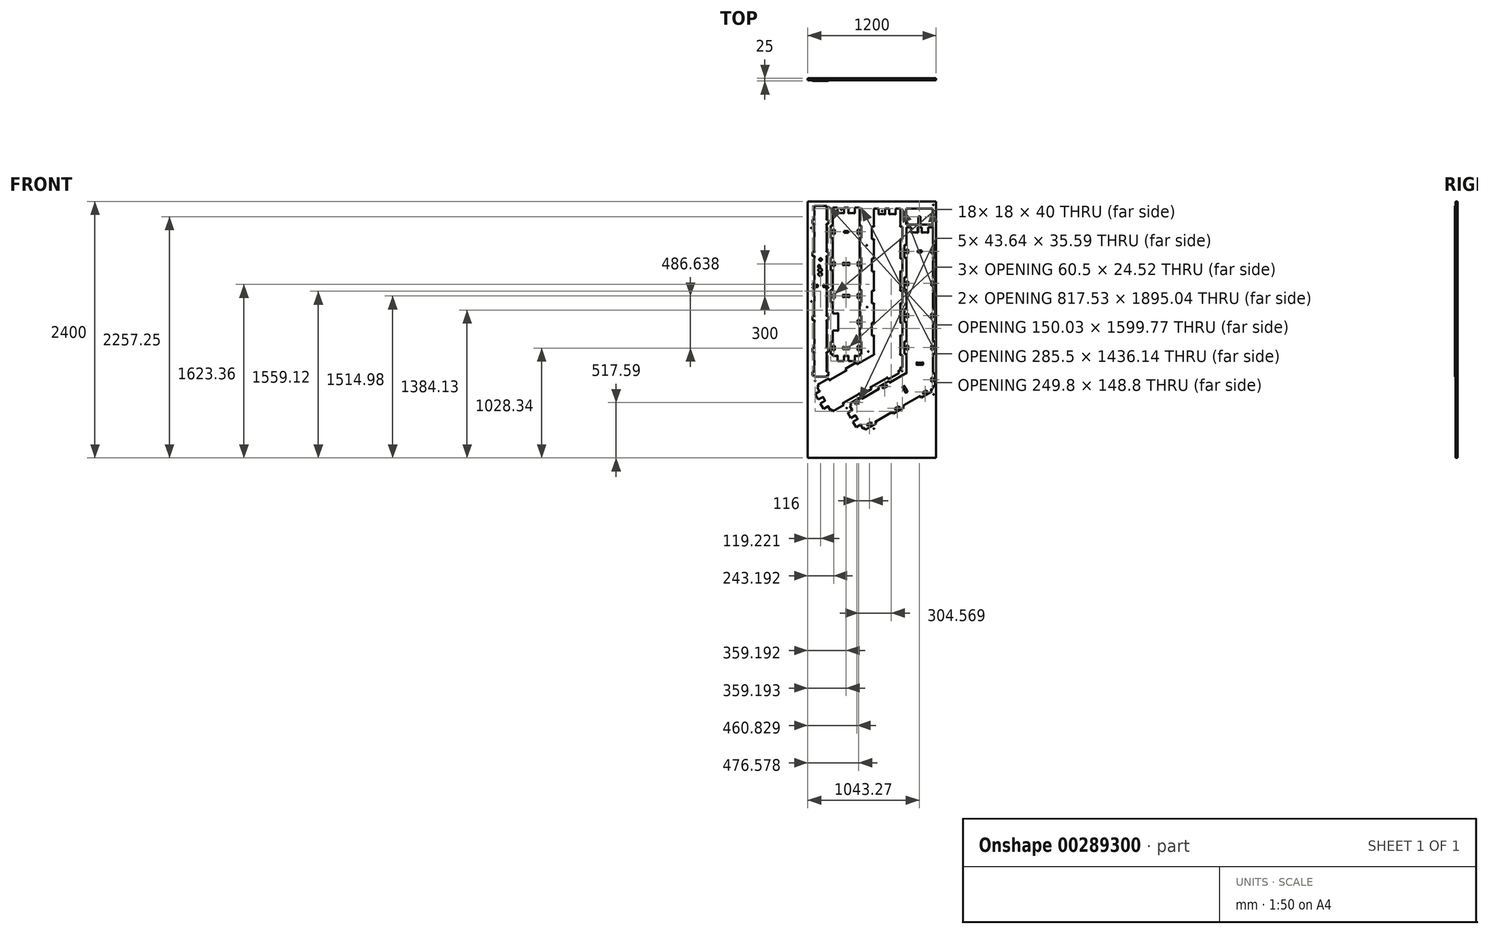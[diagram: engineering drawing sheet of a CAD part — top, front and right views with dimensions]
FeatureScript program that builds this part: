
annotation { "Feature Type Name" : "Feature", "Feature Type Description" : "" }
export const myFeature = defineFeature(function(context is Context, id is Id, definition is map)
    precondition{}
    {
        {
            var Q0;
            Q0=qCreatedBy(makeId("Front.planeOp"),FACE);
            var sketch = newSketch(context, id + "F0", { "sketchPlane" : qUnion([Q0])});
            skLineSegment(sketch, "E0", {"start": v(-600, -1200) * mm, "end": v(600, -1200) * mm});
            skLineSegment(sketch, "E1", {"start": v(600, -1200) * mm, "end": v(600, 1200) * mm});
            skLineSegment(sketch, "E2", {"start": v(600, 1200) * mm, "end": v(-600, 1200) * mm});
            skLineSegment(sketch, "E3", {"start": v(-600, 1200) * mm, "end": v(-600, -1200) * mm});
            skLineSegment(sketch, "E4", {"start": v(322.16, 191.97) * mm, "end": v(304.4, 191.97) * mm});
            skLineSegment(sketch, "E5", {"start": v(304.4, 191.97) * mm, "end": v(304.4, 72.47) * mm});
            skLineSegment(sketch, "E6", {"start": v(304.4, 72.47) * mm, "end": v(322.16, 72.47) * mm});
            skArc(sketch, "E7", {"start": v(322.16, 72.47) * mm, "mid": v(325.42, 69.33) * mm, "end": v(322.4, 65.95) * mm});
            skLineSegment(sketch, "E8", {"start": v(322.4, 65.95) * mm, "end": v(322.4, -101.5) * mm});
            skArc(sketch, "E9", {"start": v(322.4, -101.5) * mm, "mid": v(325.43, -104.89) * mm, "end": v(322.16, -108.03) * mm});
            skLineSegment(sketch, "E10", {"start": v(322.16, -108.03) * mm, "end": v(304.4, -108.03) * mm});
            skLineSegment(sketch, "E11", {"start": v(304.4, -108.03) * mm, "end": v(304.4, -227.53) * mm});
            skLineSegment(sketch, "E12", {"start": v(304.4, -227.53) * mm, "end": v(322.16, -227.53) * mm});
            skArc(sketch, "E13", {"start": v(322.16, -227.53) * mm, "mid": v(325.42, -230.67) * mm, "end": v(322.4, -234.05) * mm});
            skLineSegment(sketch, "E14", {"start": v(322.4, -234.05) * mm, "end": v(322.4, -405.6) * mm});
            skArc(sketch, "E15", {"start": v(322.4, -405.6) * mm, "mid": v(321.26, -409.95) * mm, "end": v(316.85, -409.02) * mm});
            skLineSegment(sketch, "E16", {"start": v(316.85, -409.02) * mm, "end": v(173.65, -491.7) * mm});
            skArc(sketch, "E17", {"start": v(173.65, -491.7) * mm, "mid": v(172.23, -496) * mm, "end": v(167.88, -494.74) * mm});
            skLineSegment(sketch, "E18", {"start": v(167.88, -494.74) * mm, "end": v(159, -479.37) * mm});
            skLineSegment(sketch, "E19", {"start": v(159, -479.37) * mm, "end": v(55.52, -539.12) * mm});
            skLineSegment(sketch, "E20", {"start": v(55.52, -539.12) * mm, "end": v(64.4, -554.5) * mm});
            skArc(sketch, "E21", {"start": v(64.4, -554.5) * mm, "mid": v(63.3, -558.88) * mm, "end": v(58.87, -557.97) * mm});
            skLineSegment(sketch, "E22", {"start": v(58.87, -557.97) * mm, "end": v(-86.15, -641.7) * mm});
            skArc(sketch, "E23", {"start": v(-86.15, -641.7) * mm, "mid": v(-87.57, -646) * mm, "end": v(-91.93, -644.74) * mm});
            skLineSegment(sketch, "E24", {"start": v(-91.93, -644.74) * mm, "end": v(-100.8, -629.37) * mm});
            skLineSegment(sketch, "E25", {"start": v(-100.8, -629.37) * mm, "end": v(-204.3, -689.12) * mm});
            skLineSegment(sketch, "E26", {"start": v(-204.3, -689.12) * mm, "end": v(-195.42, -704.5) * mm});
            skArc(sketch, "E27", {"start": v(-195.42, -704.5) * mm, "mid": v(-196.5, -708.88) * mm, "end": v(-200.94, -707.97) * mm});
            skLineSegment(sketch, "E28", {"start": v(-200.94, -707.97) * mm, "end": v(-206.82, -711.36) * mm});
            skLineSegment(sketch, "E29", {"start": v(-206.82, -711.36) * mm, "end": v(-187.57, -744.69) * mm});
            skArc(sketch, "E30", {"start": v(-187.57, -744.69) * mm, "mid": v(-183.27, -746.1) * mm, "end": v(-184.53, -750.46) * mm});
            skLineSegment(sketch, "E31", {"start": v(-184.53, -750.46) * mm, "end": v(-227.62, -775.33) * mm});
            skLineSegment(sketch, "E32", {"start": v(-227.62, -775.33) * mm, "end": v(-197.87, -826.86) * mm});
            skLineSegment(sketch, "E33", {"start": v(-197.87, -826.86) * mm, "end": v(-154.78, -801.99) * mm});
            skArc(sketch, "E34", {"start": v(-154.78, -801.99) * mm, "mid": v(-150.39, -803.08) * mm, "end": v(-151.3, -807.5) * mm});
            skLineSegment(sketch, "E35", {"start": v(-151.3, -807.5) * mm, "end": v(-137.58, -831.29) * mm});
            skArc(sketch, "E36", {"start": v(-137.58, -831.29) * mm, "mid": v(-133.27, -832.7) * mm, "end": v(-134.53, -837.06) * mm});
            skLineSegment(sketch, "E37", {"start": v(-134.53, -837.06) * mm, "end": v(-177.62, -861.93) * mm});
            skLineSegment(sketch, "E38", {"start": v(-177.62, -861.93) * mm, "end": v(-147.87, -913.46) * mm});
            skLineSegment(sketch, "E39", {"start": v(-147.87, -913.46) * mm, "end": v(-104.78, -888.59) * mm});
            skArc(sketch, "E40", {"start": v(-104.78, -888.59) * mm, "mid": v(-100.39, -889.68) * mm, "end": v(-101.3, -894.1) * mm});
            skLineSegment(sketch, "E41", {"start": v(-101.3, -894.1) * mm, "end": v(-82.06, -927.43) * mm});
            skLineSegment(sketch, "E42", {"start": v(-82.06, -927.43) * mm, "end": v(-76.19, -924.04) * mm});
            skArc(sketch, "E43", {"start": v(-76.19, -924.04) * mm, "mid": v(-74.77, -919.74) * mm, "end": v(-70.42, -921) * mm});
            skLineSegment(sketch, "E44", {"start": v(-70.42, -921) * mm, "end": v(-61.54, -936.37) * mm});
            skLineSegment(sketch, "E45", {"start": v(-61.54, -936.37) * mm, "end": v(41.95, -876.62) * mm});
            skLineSegment(sketch, "E46", {"start": v(41.95, -876.62) * mm, "end": v(33.07, -861.25) * mm});
            skArc(sketch, "E47", {"start": v(33.07, -861.25) * mm, "mid": v(34.16, -856.86) * mm, "end": v(38.6, -857.77) * mm});
            skLineSegment(sketch, "E48", {"start": v(38.6, -857.77) * mm, "end": v(183.62, -774.04) * mm});
            skArc(sketch, "E49", {"start": v(183.62, -774.04) * mm, "mid": v(185.04, -769.74) * mm, "end": v(189.4, -771) * mm});
            skLineSegment(sketch, "E50", {"start": v(189.4, -771) * mm, "end": v(198.27, -786.37) * mm});
            skLineSegment(sketch, "E51", {"start": v(198.27, -786.37) * mm, "end": v(301.76, -726.62) * mm});
            skLineSegment(sketch, "E52", {"start": v(301.76, -726.62) * mm, "end": v(292.88, -711.25) * mm});
            skArc(sketch, "E53", {"start": v(292.88, -711.25) * mm, "mid": v(293.97, -706.86) * mm, "end": v(298.4, -707.77) * mm});
            skLineSegment(sketch, "E54", {"start": v(298.4, -707.77) * mm, "end": v(443.43, -624.04) * mm});
            skArc(sketch, "E55", {"start": v(443.43, -624.04) * mm, "mid": v(444.85, -619.74) * mm, "end": v(449.2, -621) * mm});
            skLineSegment(sketch, "E56", {"start": v(449.2, -621) * mm, "end": v(458.07, -636.37) * mm});
            skLineSegment(sketch, "E57", {"start": v(458.07, -636.37) * mm, "end": v(561.56, -576.62) * mm});
            skLineSegment(sketch, "E58", {"start": v(561.56, -576.62) * mm, "end": v(552.69, -561.25) * mm});
            skArc(sketch, "E59", {"start": v(552.69, -561.25) * mm, "mid": v(553.78, -556.86) * mm, "end": v(558.21, -557.77) * mm});
            skLineSegment(sketch, "E60", {"start": v(558.21, -557.77) * mm, "end": v(571.91, -549.86) * mm});
            skLineSegment(sketch, "E61", {"start": v(571.91, -549.86) * mm, "end": v(571.91, -534.05) * mm});
            skArc(sketch, "E62", {"start": v(571.91, -534.05) * mm, "mid": v(568.9, -530.67) * mm, "end": v(572.16, -527.53) * mm});
            skLineSegment(sketch, "E63", {"start": v(572.16, -527.53) * mm, "end": v(589.91, -527.53) * mm});
            skLineSegment(sketch, "E64", {"start": v(589.91, -527.53) * mm, "end": v(589.91, -408.03) * mm});
            skLineSegment(sketch, "E65", {"start": v(589.91, -408.03) * mm, "end": v(572.16, -408.03) * mm});
            skArc(sketch, "E66", {"start": v(572.16, -408.03) * mm, "mid": v(568.9, -404.89) * mm, "end": v(571.91, -401.5) * mm});
            skLineSegment(sketch, "E67", {"start": v(571.91, -401.5) * mm, "end": v(571.91, -234.05) * mm});
            skArc(sketch, "E68", {"start": v(571.91, -234.05) * mm, "mid": v(568.9, -230.67) * mm, "end": v(572.16, -227.53) * mm});
            skLineSegment(sketch, "E69", {"start": v(572.16, -227.53) * mm, "end": v(589.91, -227.53) * mm});
            skLineSegment(sketch, "E70", {"start": v(589.91, -227.53) * mm, "end": v(589.91, -108.03) * mm});
            skLineSegment(sketch, "E71", {"start": v(589.91, -108.03) * mm, "end": v(572.16, -108.03) * mm});
            skArc(sketch, "E72", {"start": v(572.16, -108.03) * mm, "mid": v(568.9, -104.89) * mm, "end": v(571.91, -101.5) * mm});
            skLineSegment(sketch, "E73", {"start": v(571.91, -101.5) * mm, "end": v(571.91, 65.95) * mm});
            skArc(sketch, "E74", {"start": v(571.91, 65.95) * mm, "mid": v(568.9, 69.33) * mm, "end": v(572.16, 72.47) * mm});
            skLineSegment(sketch, "E75", {"start": v(572.16, 72.47) * mm, "end": v(589.91, 72.47) * mm});
            skLineSegment(sketch, "E76", {"start": v(589.91, 72.47) * mm, "end": v(589.91, 191.97) * mm});
            skLineSegment(sketch, "E77", {"start": v(589.91, 191.97) * mm, "end": v(572.16, 191.97) * mm});
            skArc(sketch, "E78", {"start": v(572.16, 191.97) * mm, "mid": v(568.9, 195.11) * mm, "end": v(571.91, 198.5) * mm});
            skLineSegment(sketch, "E79", {"start": v(571.91, 198.5) * mm, "end": v(571.91, 365.95) * mm});
            skArc(sketch, "E80", {"start": v(571.91, 365.95) * mm, "mid": v(568.9, 369.33) * mm, "end": v(572.16, 372.47) * mm});
            skLineSegment(sketch, "E81", {"start": v(572.16, 372.47) * mm, "end": v(589.91, 372.47) * mm});
            skLineSegment(sketch, "E82", {"start": v(589.91, 372.47) * mm, "end": v(589.91, 491.97) * mm});
            skLineSegment(sketch, "E83", {"start": v(589.91, 491.97) * mm, "end": v(572.16, 491.97) * mm});
            skArc(sketch, "E84", {"start": v(572.16, 491.97) * mm, "mid": v(568.9, 495.11) * mm, "end": v(571.91, 498.5) * mm});
            skLineSegment(sketch, "E85", {"start": v(571.91, 498.5) * mm, "end": v(571.91, 665.95) * mm});
            skArc(sketch, "E86", {"start": v(571.91, 665.95) * mm, "mid": v(568.9, 669.33) * mm, "end": v(572.16, 672.47) * mm});
            skLineSegment(sketch, "E87", {"start": v(572.16, 672.47) * mm, "end": v(589.91, 672.47) * mm});
            skLineSegment(sketch, "E88", {"start": v(589.91, 672.47) * mm, "end": v(589.91, 791.97) * mm});
            skLineSegment(sketch, "E89", {"start": v(589.91, 791.97) * mm, "end": v(572.16, 791.97) * mm});
            skArc(sketch, "E90", {"start": v(572.16, 791.97) * mm, "mid": v(568.9, 795.11) * mm, "end": v(571.91, 798.5) * mm});
            skLineSegment(sketch, "E91", {"start": v(571.91, 798.5) * mm, "end": v(571.91, 958.67) * mm});
            skLineSegment(sketch, "E92", {"start": v(571.91, 958.67) * mm, "end": v(527.41, 958.67) * mm});
            skLineSegment(sketch, "E93", {"start": v(527.41, 958.67) * mm, "end": v(527.41, 908.92) * mm});
            skArc(sketch, "E94", {"start": v(527.41, 908.92) * mm, "mid": v(524.27, 905.66) * mm, "end": v(520.9, 908.67) * mm});
            skLineSegment(sketch, "E95", {"start": v(520.9, 908.67) * mm, "end": v(473.43, 908.67) * mm});
            skArc(sketch, "E96", {"start": v(473.43, 908.67) * mm, "mid": v(470.05, 905.65) * mm, "end": v(466.91, 908.92) * mm});
            skLineSegment(sketch, "E97", {"start": v(466.91, 908.92) * mm, "end": v(466.91, 958.67) * mm});
            skLineSegment(sketch, "E98", {"start": v(466.91, 958.67) * mm, "end": v(427.41, 958.67) * mm});
            skLineSegment(sketch, "E99", {"start": v(427.41, 958.67) * mm, "end": v(427.41, 908.92) * mm});
            skArc(sketch, "E100", {"start": v(427.41, 908.92) * mm, "mid": v(424.27, 905.66) * mm, "end": v(420.9, 908.67) * mm});
            skLineSegment(sketch, "E101", {"start": v(420.9, 908.67) * mm, "end": v(373.43, 908.67) * mm});
            skArc(sketch, "E102", {"start": v(373.43, 908.67) * mm, "mid": v(370.05, 905.65) * mm, "end": v(366.9, 908.92) * mm});
            skLineSegment(sketch, "E103", {"start": v(366.9, 908.92) * mm, "end": v(366.9, 958.67) * mm});
            skLineSegment(sketch, "E104", {"start": v(366.9, 958.67) * mm, "end": v(322.4, 958.67) * mm});
            skLineSegment(sketch, "E105", {"start": v(322.4, 958.67) * mm, "end": v(322.4, 798.5) * mm});
            skArc(sketch, "E106", {"start": v(322.4, 798.5) * mm, "mid": v(325.43, 795.11) * mm, "end": v(322.16, 791.97) * mm});
            skLineSegment(sketch, "E107", {"start": v(322.16, 791.97) * mm, "end": v(304.4, 791.97) * mm});
            skLineSegment(sketch, "E108", {"start": v(304.4, 791.97) * mm, "end": v(304.4, 672.47) * mm});
            skLineSegment(sketch, "E109", {"start": v(304.4, 672.47) * mm, "end": v(322.16, 672.47) * mm});
            skArc(sketch, "E110", {"start": v(322.16, 672.47) * mm, "mid": v(325.42, 669.33) * mm, "end": v(322.4, 665.95) * mm});
            skLineSegment(sketch, "E111", {"start": v(322.4, 665.95) * mm, "end": v(322.4, 498.5) * mm});
            skArc(sketch, "E112", {"start": v(322.4, 498.5) * mm, "mid": v(325.43, 495.11) * mm, "end": v(322.16, 491.97) * mm});
            skLineSegment(sketch, "E113", {"start": v(322.16, 491.97) * mm, "end": v(304.4, 491.97) * mm});
            skLineSegment(sketch, "E114", {"start": v(304.4, 491.97) * mm, "end": v(304.4, 372.47) * mm});
            skLineSegment(sketch, "E115", {"start": v(304.4, 372.47) * mm, "end": v(322.16, 372.47) * mm});
            skArc(sketch, "E116", {"start": v(322.16, 372.47) * mm, "mid": v(325.42, 369.33) * mm, "end": v(322.4, 365.95) * mm});
            skLineSegment(sketch, "E117", {"start": v(322.4, 365.95) * mm, "end": v(322.4, 198.5) * mm});
            skArc(sketch, "E118", {"start": v(322.4, 198.5) * mm, "mid": v(325.43, 195.11) * mm, "end": v(322.16, 191.97) * mm});
            skArc(sketch, "E119", {"start": v(17.84, 71.47) * mm, "mid": v(20.86, 68.1) * mm, "end": v(17.6, 64.95) * mm});
            skLineSegment(sketch, "E120", {"start": v(17.6, 64.95) * mm, "end": v(-0.16, 64.95) * mm});
            skLineSegment(sketch, "E121", {"start": v(-0.16, 64.95) * mm, "end": v(-0.16, -54.55) * mm});
            skLineSegment(sketch, "E122", {"start": v(-0.16, -54.55) * mm, "end": v(17.6, -54.55) * mm});
            skArc(sketch, "E123", {"start": v(17.6, -54.55) * mm, "mid": v(20.85, -57.69) * mm, "end": v(17.84, -61.07) * mm});
            skLineSegment(sketch, "E124", {"start": v(17.84, -61.07) * mm, "end": v(17.84, -226.42) * mm});
            skArc(sketch, "E125", {"start": v(17.84, -226.42) * mm, "mid": v(20.86, -229.76) * mm, "end": v(17.66, -232.94) * mm});
            skLineSegment(sketch, "E126", {"start": v(17.66, -232.94) * mm, "end": v(-130.92, -318.72) * mm});
            skArc(sketch, "E127", {"start": v(-130.92, -318.72) * mm, "mid": v(-132.34, -323.02) * mm, "end": v(-136.69, -321.76) * mm});
            skLineSegment(sketch, "E128", {"start": v(-136.69, -321.76) * mm, "end": v(-145.56, -306.39) * mm});
            skLineSegment(sketch, "E129", {"start": v(-145.56, -306.39) * mm, "end": v(-249.05, -366.14) * mm});
            skLineSegment(sketch, "E130", {"start": v(-249.05, -366.14) * mm, "end": v(-240.18, -381.5) * mm});
            skArc(sketch, "E131", {"start": v(-240.18, -381.5) * mm, "mid": v(-241.27, -385.9) * mm, "end": v(-245.7, -384.99) * mm});
            skLineSegment(sketch, "E132", {"start": v(-245.7, -384.99) * mm, "end": v(-390.72, -468.72) * mm});
            skArc(sketch, "E133", {"start": v(-390.72, -468.72) * mm, "mid": v(-392.14, -473.02) * mm, "end": v(-396.5, -471.76) * mm});
            skLineSegment(sketch, "E134", {"start": v(-396.5, -471.76) * mm, "end": v(-405.37, -456.39) * mm});
            skLineSegment(sketch, "E135", {"start": v(-405.37, -456.39) * mm, "end": v(-508.86, -516.14) * mm});
            skLineSegment(sketch, "E136", {"start": v(-508.86, -516.14) * mm, "end": v(-499.99, -531.5) * mm});
            skArc(sketch, "E137", {"start": v(-499.99, -531.5) * mm, "mid": v(-501.08, -535.9) * mm, "end": v(-505.5, -534.99) * mm});
            skLineSegment(sketch, "E138", {"start": v(-505.5, -534.99) * mm, "end": v(-511.38, -538.38) * mm});
            skLineSegment(sketch, "E139", {"start": v(-511.38, -538.38) * mm, "end": v(-492.14, -571.7) * mm});
            skArc(sketch, "E140", {"start": v(-492.14, -571.7) * mm, "mid": v(-487.84, -573.12) * mm, "end": v(-489.1, -577.48) * mm});
            skLineSegment(sketch, "E141", {"start": v(-489.1, -577.48) * mm, "end": v(-532.19, -602.35) * mm});
            skLineSegment(sketch, "E142", {"start": v(-532.19, -602.35) * mm, "end": v(-502.44, -653.88) * mm});
            skLineSegment(sketch, "E143", {"start": v(-502.44, -653.88) * mm, "end": v(-459.35, -629) * mm});
            skArc(sketch, "E144", {"start": v(-459.35, -629) * mm, "mid": v(-454.96, -630.1) * mm, "end": v(-455.87, -634.53) * mm});
            skLineSegment(sketch, "E145", {"start": v(-455.87, -634.53) * mm, "end": v(-442.14, -658.3) * mm});
            skArc(sketch, "E146", {"start": v(-442.14, -658.3) * mm, "mid": v(-437.84, -659.72) * mm, "end": v(-439.1, -664.08) * mm});
            skLineSegment(sketch, "E147", {"start": v(-439.1, -664.08) * mm, "end": v(-482.19, -688.95) * mm});
            skLineSegment(sketch, "E148", {"start": v(-482.19, -688.95) * mm, "end": v(-452.44, -740.48) * mm});
            skLineSegment(sketch, "E149", {"start": v(-452.44, -740.48) * mm, "end": v(-409.35, -715.6) * mm});
            skArc(sketch, "E150", {"start": v(-409.35, -715.6) * mm, "mid": v(-404.96, -716.7) * mm, "end": v(-405.87, -721.13) * mm});
            skLineSegment(sketch, "E151", {"start": v(-405.87, -721.13) * mm, "end": v(-386.63, -754.45) * mm});
            skLineSegment(sketch, "E152", {"start": v(-386.63, -754.45) * mm, "end": v(-380.76, -751.06) * mm});
            skArc(sketch, "E153", {"start": v(-380.76, -751.06) * mm, "mid": v(-379.34, -746.76) * mm, "end": v(-374.99, -748.02) * mm});
            skLineSegment(sketch, "E154", {"start": v(-374.99, -748.02) * mm, "end": v(-366.11, -763.39) * mm});
            skLineSegment(sketch, "E155", {"start": v(-366.11, -763.39) * mm, "end": v(-262.62, -703.64) * mm});
            skLineSegment(sketch, "E156", {"start": v(-262.62, -703.64) * mm, "end": v(-271.5, -688.27) * mm});
            skArc(sketch, "E157", {"start": v(-271.5, -688.27) * mm, "mid": v(-270.4, -683.88) * mm, "end": v(-265.97, -684.79) * mm});
            skLineSegment(sketch, "E158", {"start": v(-265.97, -684.79) * mm, "end": v(-120.95, -601.06) * mm});
            skArc(sketch, "E159", {"start": v(-120.95, -601.06) * mm, "mid": v(-119.53, -596.76) * mm, "end": v(-115.18, -598.02) * mm});
            skLineSegment(sketch, "E160", {"start": v(-115.18, -598.02) * mm, "end": v(-106.3, -613.39) * mm});
            skLineSegment(sketch, "E161", {"start": v(-106.3, -613.39) * mm, "end": v(-2.81, -553.64) * mm});
            skLineSegment(sketch, "E162", {"start": v(-2.81, -553.64) * mm, "end": v(-11.69, -538.27) * mm});
            skArc(sketch, "E163", {"start": v(-11.69, -538.27) * mm, "mid": v(-10.6, -533.87) * mm, "end": v(-6.17, -534.79) * mm});
            skLineSegment(sketch, "E164", {"start": v(-6.17, -534.79) * mm, "end": v(138.86, -451.06) * mm});
            skArc(sketch, "E165", {"start": v(138.86, -451.06) * mm, "mid": v(140.28, -446.76) * mm, "end": v(144.63, -448.02) * mm});
            skLineSegment(sketch, "E166", {"start": v(144.63, -448.02) * mm, "end": v(153.5, -463.39) * mm});
            skLineSegment(sketch, "E167", {"start": v(153.5, -463.39) * mm, "end": v(257, -403.64) * mm});
            skLineSegment(sketch, "E168", {"start": v(257, -403.64) * mm, "end": v(248.12, -388.27) * mm});
            skArc(sketch, "E169", {"start": v(248.12, -388.27) * mm, "mid": v(249.21, -383.87) * mm, "end": v(253.64, -384.79) * mm});
            skLineSegment(sketch, "E170", {"start": v(253.64, -384.79) * mm, "end": v(267.34, -376.88) * mm});
            skLineSegment(sketch, "E171", {"start": v(267.34, -376.88) * mm, "end": v(267.34, -361.07) * mm});
            skArc(sketch, "E172", {"start": v(267.34, -361.07) * mm, "mid": v(264.32, -357.68) * mm, "end": v(267.6, -354.55) * mm});
            skLineSegment(sketch, "E173", {"start": v(267.6, -354.55) * mm, "end": v(285.34, -354.55) * mm});
            skLineSegment(sketch, "E174", {"start": v(285.34, -354.55) * mm, "end": v(285.34, -235.05) * mm});
            skLineSegment(sketch, "E175", {"start": v(285.34, -235.05) * mm, "end": v(267.6, -235.05) * mm});
            skArc(sketch, "E176", {"start": v(267.6, -235.05) * mm, "mid": v(264.33, -231.9) * mm, "end": v(267.34, -228.53) * mm});
            skLineSegment(sketch, "E177", {"start": v(267.34, -228.53) * mm, "end": v(267.34, -61.07) * mm});
            skArc(sketch, "E178", {"start": v(267.34, -61.07) * mm, "mid": v(264.32, -57.68) * mm, "end": v(267.6, -54.55) * mm});
            skLineSegment(sketch, "E179", {"start": v(267.6, -54.55) * mm, "end": v(285.34, -54.55) * mm});
            skLineSegment(sketch, "E180", {"start": v(285.34, -54.55) * mm, "end": v(285.34, 64.95) * mm});
            skLineSegment(sketch, "E181", {"start": v(285.34, 64.95) * mm, "end": v(267.6, 64.95) * mm});
            skArc(sketch, "E182", {"start": v(267.6, 64.95) * mm, "mid": v(264.33, 68.1) * mm, "end": v(267.34, 71.47) * mm});
            skLineSegment(sketch, "E183", {"start": v(267.34, 71.47) * mm, "end": v(267.34, 238.94) * mm});
            skArc(sketch, "E184", {"start": v(267.34, 238.94) * mm, "mid": v(264.32, 242.32) * mm, "end": v(267.6, 245.46) * mm});
            skLineSegment(sketch, "E185", {"start": v(267.6, 245.46) * mm, "end": v(285.34, 245.46) * mm});
            skLineSegment(sketch, "E186", {"start": v(285.34, 245.46) * mm, "end": v(285.34, 364.96) * mm});
            skLineSegment(sketch, "E187", {"start": v(285.34, 364.96) * mm, "end": v(267.6, 364.96) * mm});
            skArc(sketch, "E188", {"start": v(267.6, 364.96) * mm, "mid": v(264.33, 368.1) * mm, "end": v(267.34, 371.48) * mm});
            skLineSegment(sketch, "E189", {"start": v(267.34, 371.48) * mm, "end": v(267.34, 538.94) * mm});
            skArc(sketch, "E190", {"start": v(267.34, 538.94) * mm, "mid": v(264.32, 542.32) * mm, "end": v(267.6, 545.46) * mm});
            skLineSegment(sketch, "E191", {"start": v(267.6, 545.46) * mm, "end": v(285.34, 545.46) * mm});
            skLineSegment(sketch, "E192", {"start": v(285.34, 545.46) * mm, "end": v(285.34, 664.96) * mm});
            skLineSegment(sketch, "E193", {"start": v(285.34, 664.96) * mm, "end": v(267.6, 664.96) * mm});
            skArc(sketch, "E194", {"start": v(267.6, 664.96) * mm, "mid": v(264.33, 668.1) * mm, "end": v(267.34, 671.48) * mm});
            skLineSegment(sketch, "E195", {"start": v(267.34, 671.48) * mm, "end": v(267.34, 838.94) * mm});
            skArc(sketch, "E196", {"start": v(267.34, 838.94) * mm, "mid": v(264.32, 842.32) * mm, "end": v(267.6, 845.46) * mm});
            skLineSegment(sketch, "E197", {"start": v(267.6, 845.46) * mm, "end": v(285.34, 845.46) * mm});
            skLineSegment(sketch, "E198", {"start": v(285.34, 845.46) * mm, "end": v(285.34, 964.96) * mm});
            skLineSegment(sketch, "E199", {"start": v(285.34, 964.96) * mm, "end": v(267.6, 964.96) * mm});
            skArc(sketch, "E200", {"start": v(267.6, 964.96) * mm, "mid": v(264.33, 968.1) * mm, "end": v(267.34, 971.48) * mm});
            skLineSegment(sketch, "E201", {"start": v(267.34, 971.48) * mm, "end": v(267.34, 1131.65) * mm});
            skLineSegment(sketch, "E202", {"start": v(267.34, 1131.65) * mm, "end": v(222.84, 1131.65) * mm});
            skLineSegment(sketch, "E203", {"start": v(222.84, 1131.65) * mm, "end": v(222.84, 1081.9) * mm});
            skArc(sketch, "E204", {"start": v(222.84, 1081.9) * mm, "mid": v(219.7, 1078.64) * mm, "end": v(216.32, 1081.65) * mm});
            skLineSegment(sketch, "E205", {"start": v(216.32, 1081.65) * mm, "end": v(168.86, 1081.65) * mm});
            skArc(sketch, "E206", {"start": v(168.86, 1081.65) * mm, "mid": v(165.48, 1078.64) * mm, "end": v(162.34, 1081.9) * mm});
            skLineSegment(sketch, "E207", {"start": v(162.34, 1081.9) * mm, "end": v(162.34, 1131.65) * mm});
            skLineSegment(sketch, "E208", {"start": v(162.34, 1131.65) * mm, "end": v(122.84, 1131.65) * mm});
            skLineSegment(sketch, "E209", {"start": v(122.84, 1131.65) * mm, "end": v(122.84, 1081.9) * mm});
            skArc(sketch, "E210", {"start": v(122.84, 1081.9) * mm, "mid": v(119.7, 1078.64) * mm, "end": v(116.32, 1081.65) * mm});
            skLineSegment(sketch, "E211", {"start": v(116.32, 1081.65) * mm, "end": v(68.86, 1081.65) * mm});
            skArc(sketch, "E212", {"start": v(68.86, 1081.65) * mm, "mid": v(65.48, 1078.64) * mm, "end": v(62.34, 1081.9) * mm});
            skLineSegment(sketch, "E213", {"start": v(62.34, 1081.9) * mm, "end": v(62.34, 1131.65) * mm});
            skLineSegment(sketch, "E214", {"start": v(62.34, 1131.65) * mm, "end": v(17.84, 1131.65) * mm});
            skLineSegment(sketch, "E215", {"start": v(17.84, 1131.65) * mm, "end": v(17.84, 971.48) * mm});
            skArc(sketch, "E216", {"start": v(17.84, 971.48) * mm, "mid": v(20.86, 968.1) * mm, "end": v(17.6, 964.96) * mm});
            skLineSegment(sketch, "E217", {"start": v(17.6, 964.96) * mm, "end": v(-0.16, 964.96) * mm});
            skLineSegment(sketch, "E218", {"start": v(-0.16, 964.96) * mm, "end": v(-0.16, 845.46) * mm});
            skLineSegment(sketch, "E219", {"start": v(-0.16, 845.46) * mm, "end": v(17.6, 845.46) * mm});
            skArc(sketch, "E220", {"start": v(17.6, 845.46) * mm, "mid": v(20.85, 842.32) * mm, "end": v(17.84, 838.94) * mm});
            skLineSegment(sketch, "E221", {"start": v(17.84, 838.94) * mm, "end": v(17.84, 671.48) * mm});
            skArc(sketch, "E222", {"start": v(17.84, 671.48) * mm, "mid": v(20.86, 668.1) * mm, "end": v(17.6, 664.96) * mm});
            skLineSegment(sketch, "E223", {"start": v(17.6, 664.96) * mm, "end": v(-0.16, 664.96) * mm});
            skLineSegment(sketch, "E224", {"start": v(-0.16, 664.96) * mm, "end": v(-0.16, 545.46) * mm});
            skLineSegment(sketch, "E225", {"start": v(-0.16, 545.46) * mm, "end": v(17.6, 545.46) * mm});
            skArc(sketch, "E226", {"start": v(17.6, 545.46) * mm, "mid": v(20.85, 542.32) * mm, "end": v(17.84, 538.94) * mm});
            skLineSegment(sketch, "E227", {"start": v(17.84, 538.94) * mm, "end": v(17.84, 371.48) * mm});
            skArc(sketch, "E228", {"start": v(17.84, 371.48) * mm, "mid": v(20.86, 368.1) * mm, "end": v(17.6, 364.96) * mm});
            skLineSegment(sketch, "E229", {"start": v(17.6, 364.96) * mm, "end": v(-0.16, 364.96) * mm});
            skLineSegment(sketch, "E230", {"start": v(-0.16, 364.96) * mm, "end": v(-0.16, 245.46) * mm});
            skLineSegment(sketch, "E231", {"start": v(-0.16, 245.46) * mm, "end": v(17.6, 245.46) * mm});
            skArc(sketch, "E232", {"start": v(17.6, 245.46) * mm, "mid": v(20.85, 242.32) * mm, "end": v(17.84, 238.94) * mm});
            skLineSegment(sketch, "E233", {"start": v(17.84, 238.94) * mm, "end": v(17.84, 71.47) * mm});
            skLineSegment(sketch, "E234", {"start": v(-537.8, 1159) * mm, "end": v(-537.8, 1035.02) * mm});
            skArc(sketch, "E235", {"start": v(-537.8, 1035.02) * mm, "mid": v(-534.78, 1032) * mm, "end": v(-537.8, 1029) * mm});
            skLineSegment(sketch, "E236", {"start": v(-537.8, 1029) * mm, "end": v(-552.8, 1029) * mm});
            skLineSegment(sketch, "E237", {"start": v(-552.8, 1029) * mm, "end": v(-555.8, 1026) * mm});
            skLineSegment(sketch, "E238", {"start": v(-555.8, 1026) * mm, "end": v(-555.8, 992) * mm});
            skLineSegment(sketch, "E239", {"start": v(-555.8, 992) * mm, "end": v(-552.8, 989) * mm});
            skLineSegment(sketch, "E240", {"start": v(-552.8, 989) * mm, "end": v(-537.8, 989) * mm});
            skArc(sketch, "E241", {"start": v(-537.8, 989) * mm, "mid": v(-534.78, 985.99) * mm, "end": v(-537.8, 982.98) * mm});
            skLineSegment(sketch, "E242", {"start": v(-537.8, 982.98) * mm, "end": v(-537.79, 735.02) * mm});
            skArc(sketch, "E243", {"start": v(-537.79, 735.02) * mm, "mid": v(-534.78, 732) * mm, "end": v(-537.79, 729) * mm});
            skLineSegment(sketch, "E244", {"start": v(-537.79, 729) * mm, "end": v(-552.79, 729) * mm});
            skLineSegment(sketch, "E245", {"start": v(-552.79, 729) * mm, "end": v(-555.79, 726) * mm});
            skLineSegment(sketch, "E246", {"start": v(-555.79, 726) * mm, "end": v(-555.79, 692) * mm});
            skLineSegment(sketch, "E247", {"start": v(-555.79, 692) * mm, "end": v(-552.79, 689) * mm});
            skLineSegment(sketch, "E248", {"start": v(-552.79, 689) * mm, "end": v(-537.79, 689) * mm});
            skArc(sketch, "E249", {"start": v(-537.79, 689) * mm, "mid": v(-534.78, 685.99) * mm, "end": v(-537.79, 682.98) * mm});
            skLineSegment(sketch, "E250", {"start": v(-537.79, 682.98) * mm, "end": v(-537.78, 435.02) * mm});
            skArc(sketch, "E251", {"start": v(-537.78, 435.02) * mm, "mid": v(-534.77, 432) * mm, "end": v(-537.78, 429) * mm});
            skLineSegment(sketch, "E252", {"start": v(-537.78, 429) * mm, "end": v(-552.78, 429) * mm});
            skLineSegment(sketch, "E253", {"start": v(-552.78, 429) * mm, "end": v(-555.78, 426) * mm});
            skLineSegment(sketch, "E254", {"start": v(-555.78, 426) * mm, "end": v(-555.78, 418) * mm});
            skLineSegment(sketch, "E255", {"start": v(-555.78, 418) * mm, "end": v(-512.8, 418) * mm});
            skArc(sketch, "E256", {"start": v(-512.8, 418) * mm, "mid": v(-509.8, 421) * mm, "end": v(-506.78, 418) * mm});
            skLineSegment(sketch, "E257", {"start": v(-506.78, 418) * mm, "end": v(-506.78, 400) * mm});
            skArc(sketch, "E258", {"start": v(-506.78, 400) * mm, "mid": v(-509.8, 396.99) * mm, "end": v(-512.8, 400) * mm});
            skLineSegment(sketch, "E259", {"start": v(-512.8, 400) * mm, "end": v(-555.78, 400) * mm});
            skLineSegment(sketch, "E260", {"start": v(-555.78, 400) * mm, "end": v(-555.78, 392) * mm});
            skLineSegment(sketch, "E261", {"start": v(-555.78, 392) * mm, "end": v(-552.78, 389) * mm});
            skLineSegment(sketch, "E262", {"start": v(-552.78, 389) * mm, "end": v(-537.78, 389) * mm});
            skArc(sketch, "E263", {"start": v(-537.78, 389) * mm, "mid": v(-534.77, 385.99) * mm, "end": v(-537.78, 382.98) * mm});
            skLineSegment(sketch, "E264", {"start": v(-537.78, 382.98) * mm, "end": v(-537.78, 135.02) * mm});
            skArc(sketch, "E265", {"start": v(-537.78, 135.02) * mm, "mid": v(-534.77, 132) * mm, "end": v(-537.78, 129) * mm});
            skLineSegment(sketch, "E266", {"start": v(-537.78, 129) * mm, "end": v(-552.78, 129) * mm});
            skLineSegment(sketch, "E267", {"start": v(-552.78, 129) * mm, "end": v(-555.78, 126) * mm});
            skLineSegment(sketch, "E268", {"start": v(-555.78, 126) * mm, "end": v(-555.78, 92) * mm});
            skLineSegment(sketch, "E269", {"start": v(-555.78, 92) * mm, "end": v(-552.78, 89) * mm});
            skLineSegment(sketch, "E270", {"start": v(-552.78, 89) * mm, "end": v(-537.78, 89) * mm});
            skArc(sketch, "E271", {"start": v(-537.78, 89) * mm, "mid": v(-534.77, 85.99) * mm, "end": v(-537.78, 82.98) * mm});
            skLineSegment(sketch, "E272", {"start": v(-537.78, 82.98) * mm, "end": v(-537.77, -164.98) * mm});
            skArc(sketch, "E273", {"start": v(-537.77, -164.98) * mm, "mid": v(-534.76, -168) * mm, "end": v(-537.77, -171) * mm});
            skLineSegment(sketch, "E274", {"start": v(-537.77, -171) * mm, "end": v(-552.77, -171) * mm});
            skLineSegment(sketch, "E275", {"start": v(-552.77, -171) * mm, "end": v(-555.77, -174) * mm});
            skLineSegment(sketch, "E276", {"start": v(-555.77, -174) * mm, "end": v(-555.77, -208) * mm});
            skLineSegment(sketch, "E277", {"start": v(-555.77, -208) * mm, "end": v(-552.77, -211) * mm});
            skLineSegment(sketch, "E278", {"start": v(-552.77, -211) * mm, "end": v(-537.77, -211) * mm});
            skArc(sketch, "E279", {"start": v(-537.77, -211) * mm, "mid": v(-534.76, -214.01) * mm, "end": v(-537.77, -217.02) * mm});
            skLineSegment(sketch, "E280", {"start": v(-537.77, -217.02) * mm, "end": v(-537.77, -384.98) * mm});
            skArc(sketch, "E281", {"start": v(-537.77, -384.98) * mm, "mid": v(-534.76, -388) * mm, "end": v(-537.77, -391) * mm});
            skLineSegment(sketch, "E282", {"start": v(-537.77, -391) * mm, "end": v(-552.77, -391) * mm});
            skLineSegment(sketch, "E283", {"start": v(-552.77, -391) * mm, "end": v(-555.77, -394) * mm});
            skLineSegment(sketch, "E284", {"start": v(-555.77, -394) * mm, "end": v(-555.77, -428) * mm});
            skLineSegment(sketch, "E285", {"start": v(-555.77, -428) * mm, "end": v(-552.77, -431) * mm});
            skLineSegment(sketch, "E286", {"start": v(-552.77, -431) * mm, "end": v(-537.77, -431) * mm});
            skArc(sketch, "E287", {"start": v(-537.77, -431) * mm, "mid": v(-534.76, -434.01) * mm, "end": v(-537.77, -437.02) * mm});
            skLineSegment(sketch, "E288", {"start": v(-537.77, -437.02) * mm, "end": v(-537.77, -440.77) * mm});
            skLineSegment(sketch, "E289", {"start": v(-537.77, -440.77) * mm, "end": v(-423.77, -440.77) * mm});
            skLineSegment(sketch, "E290", {"start": v(-423.77, -440.77) * mm, "end": v(-423.77, -437.02) * mm});
            skArc(sketch, "E291", {"start": v(-423.77, -437.02) * mm, "mid": v(-426.78, -434.01) * mm, "end": v(-423.77, -431) * mm});
            skLineSegment(sketch, "E292", {"start": v(-423.77, -431) * mm, "end": v(-408.77, -431) * mm});
            skLineSegment(sketch, "E293", {"start": v(-408.77, -431) * mm, "end": v(-405.77, -428) * mm});
            skLineSegment(sketch, "E294", {"start": v(-405.77, -428) * mm, "end": v(-405.77, -394) * mm});
            skLineSegment(sketch, "E295", {"start": v(-405.77, -394) * mm, "end": v(-408.77, -391) * mm});
            skLineSegment(sketch, "E296", {"start": v(-408.77, -391) * mm, "end": v(-423.77, -391) * mm});
            skArc(sketch, "E297", {"start": v(-423.77, -391) * mm, "mid": v(-426.78, -388) * mm, "end": v(-423.77, -384.98) * mm});
            skLineSegment(sketch, "E298", {"start": v(-423.77, -384.98) * mm, "end": v(-423.77, -217.02) * mm});
            skArc(sketch, "E299", {"start": v(-423.77, -217.02) * mm, "mid": v(-426.78, -214.01) * mm, "end": v(-423.77, -211) * mm});
            skLineSegment(sketch, "E300", {"start": v(-423.77, -211) * mm, "end": v(-408.77, -211) * mm});
            skLineSegment(sketch, "E301", {"start": v(-408.77, -211) * mm, "end": v(-405.77, -208) * mm});
            skLineSegment(sketch, "E302", {"start": v(-405.77, -208) * mm, "end": v(-405.77, -174) * mm});
            skLineSegment(sketch, "E303", {"start": v(-405.77, -174) * mm, "end": v(-408.77, -171) * mm});
            skLineSegment(sketch, "E304", {"start": v(-408.77, -171) * mm, "end": v(-423.77, -171) * mm});
            skArc(sketch, "E305", {"start": v(-423.77, -171) * mm, "mid": v(-426.78, -168) * mm, "end": v(-423.77, -164.98) * mm});
            skLineSegment(sketch, "E306", {"start": v(-423.77, -164.98) * mm, "end": v(-423.78, 82.98) * mm});
            skArc(sketch, "E307", {"start": v(-423.78, 82.98) * mm, "mid": v(-426.79, 85.99) * mm, "end": v(-423.78, 89) * mm});
            skLineSegment(sketch, "E308", {"start": v(-423.78, 89) * mm, "end": v(-408.78, 89) * mm});
            skLineSegment(sketch, "E309", {"start": v(-408.78, 89) * mm, "end": v(-405.78, 92) * mm});
            skLineSegment(sketch, "E310", {"start": v(-405.78, 92) * mm, "end": v(-405.78, 126) * mm});
            skLineSegment(sketch, "E311", {"start": v(-405.78, 126) * mm, "end": v(-408.78, 129) * mm});
            skLineSegment(sketch, "E312", {"start": v(-408.78, 129) * mm, "end": v(-423.78, 129) * mm});
            skArc(sketch, "E313", {"start": v(-423.78, 129) * mm, "mid": v(-426.79, 132) * mm, "end": v(-423.78, 135.02) * mm});
            skLineSegment(sketch, "E314", {"start": v(-423.78, 135.02) * mm, "end": v(-423.78, 382.98) * mm});
            skArc(sketch, "E315", {"start": v(-423.78, 382.98) * mm, "mid": v(-426.8, 385.99) * mm, "end": v(-423.78, 389) * mm});
            skLineSegment(sketch, "E316", {"start": v(-423.78, 389) * mm, "end": v(-408.78, 389) * mm});
            skLineSegment(sketch, "E317", {"start": v(-408.78, 389) * mm, "end": v(-405.78, 392) * mm});
            skLineSegment(sketch, "E318", {"start": v(-405.78, 392) * mm, "end": v(-405.78, 400) * mm});
            skLineSegment(sketch, "E319", {"start": v(-405.78, 400) * mm, "end": v(-448.76, 400) * mm});
            skArc(sketch, "E320", {"start": v(-448.76, 400) * mm, "mid": v(-451.77, 396.99) * mm, "end": v(-454.78, 400) * mm});
            skLineSegment(sketch, "E321", {"start": v(-454.78, 400) * mm, "end": v(-454.78, 418) * mm});
            skArc(sketch, "E322", {"start": v(-454.78, 418) * mm, "mid": v(-451.77, 421) * mm, "end": v(-448.76, 418) * mm});
            skLineSegment(sketch, "E323", {"start": v(-448.76, 418) * mm, "end": v(-405.78, 418) * mm});
            skLineSegment(sketch, "E324", {"start": v(-405.78, 418) * mm, "end": v(-405.78, 426) * mm});
            skLineSegment(sketch, "E325", {"start": v(-405.78, 426) * mm, "end": v(-408.78, 429) * mm});
            skLineSegment(sketch, "E326", {"start": v(-408.78, 429) * mm, "end": v(-423.78, 429) * mm});
            skArc(sketch, "E327", {"start": v(-423.78, 429) * mm, "mid": v(-426.8, 432) * mm, "end": v(-423.78, 435.02) * mm});
            skLineSegment(sketch, "E328", {"start": v(-423.78, 435.02) * mm, "end": v(-423.79, 682.98) * mm});
            skArc(sketch, "E329", {"start": v(-423.79, 682.98) * mm, "mid": v(-426.8, 685.99) * mm, "end": v(-423.79, 689) * mm});
            skLineSegment(sketch, "E330", {"start": v(-423.79, 689) * mm, "end": v(-408.79, 689) * mm});
            skLineSegment(sketch, "E331", {"start": v(-408.79, 689) * mm, "end": v(-405.79, 692) * mm});
            skLineSegment(sketch, "E332", {"start": v(-405.79, 692) * mm, "end": v(-405.79, 726) * mm});
            skLineSegment(sketch, "E333", {"start": v(-405.79, 726) * mm, "end": v(-408.79, 729) * mm});
            skLineSegment(sketch, "E334", {"start": v(-408.79, 729) * mm, "end": v(-423.79, 729) * mm});
            skArc(sketch, "E335", {"start": v(-423.79, 729) * mm, "mid": v(-426.8, 732) * mm, "end": v(-423.79, 735.02) * mm});
            skLineSegment(sketch, "E336", {"start": v(-423.79, 735.02) * mm, "end": v(-423.8, 982.98) * mm});
            skArc(sketch, "E337", {"start": v(-423.8, 982.98) * mm, "mid": v(-426.8, 985.99) * mm, "end": v(-423.8, 989) * mm});
            skLineSegment(sketch, "E338", {"start": v(-423.8, 989) * mm, "end": v(-408.8, 989) * mm});
            skLineSegment(sketch, "E339", {"start": v(-408.8, 989) * mm, "end": v(-405.8, 992) * mm});
            skLineSegment(sketch, "E340", {"start": v(-405.8, 992) * mm, "end": v(-405.8, 1026) * mm});
            skLineSegment(sketch, "E341", {"start": v(-405.8, 1026) * mm, "end": v(-408.8, 1029) * mm});
            skLineSegment(sketch, "E342", {"start": v(-408.8, 1029) * mm, "end": v(-423.8, 1029) * mm});
            skArc(sketch, "E343", {"start": v(-423.8, 1029) * mm, "mid": v(-426.8, 1032) * mm, "end": v(-423.8, 1035.02) * mm});
            skLineSegment(sketch, "E344", {"start": v(-423.8, 1035.02) * mm, "end": v(-423.8, 1159) * mm});
            skLineSegment(sketch, "E345", {"start": v(-423.8, 1159) * mm, "end": v(-537.8, 1159) * mm});
            skLineSegment(sketch, "E346", {"start": v(-98.06, -111.9) * mm, "end": v(-116.06, -111.9) * mm});
            skArc(sketch, "E347", {"start": v(-116.06, -111.9) * mm, "mid": v(-119.07, -108.9) * mm, "end": v(-116.06, -105.89) * mm});
            skLineSegment(sketch, "E348", {"start": v(-116.06, -105.89) * mm, "end": v(-116.06, 5.89) * mm});
            skArc(sketch, "E349", {"start": v(-116.06, 5.89) * mm, "mid": v(-119.07, 8.9) * mm, "end": v(-116.06, 11.9) * mm});
            skLineSegment(sketch, "E350", {"start": v(-116.06, 11.9) * mm, "end": v(-98.06, 11.9) * mm});
            skLineSegment(sketch, "E351", {"start": v(-98.06, 11.9) * mm, "end": v(-98.06, 131.4) * mm});
            skLineSegment(sketch, "E352", {"start": v(-98.06, 131.4) * mm, "end": v(-116.06, 131.4) * mm});
            skArc(sketch, "E353", {"start": v(-116.06, 131.4) * mm, "mid": v(-119.07, 134.42) * mm, "end": v(-116.06, 137.43) * mm});
            skLineSegment(sketch, "E354", {"start": v(-116.06, 137.43) * mm, "end": v(-116.06, 249.2) * mm});
            skArc(sketch, "E355", {"start": v(-116.06, 249.2) * mm, "mid": v(-119.07, 252.22) * mm, "end": v(-116.06, 255.23) * mm});
            skLineSegment(sketch, "E356", {"start": v(-116.06, 255.23) * mm, "end": v(-98.06, 255.23) * mm});
            skLineSegment(sketch, "E357", {"start": v(-98.06, 255.23) * mm, "end": v(-98.06, 374.73) * mm});
            skLineSegment(sketch, "E358", {"start": v(-98.06, 374.73) * mm, "end": v(-116.06, 374.73) * mm});
            skArc(sketch, "E359", {"start": v(-116.06, 374.73) * mm, "mid": v(-119.07, 377.74) * mm, "end": v(-116.06, 380.75) * mm});
            skLineSegment(sketch, "E360", {"start": v(-116.06, 380.75) * mm, "end": v(-116.06, 549.2) * mm});
            skArc(sketch, "E361", {"start": v(-116.06, 549.2) * mm, "mid": v(-119.07, 552.22) * mm, "end": v(-116.06, 555.23) * mm});
            skLineSegment(sketch, "E362", {"start": v(-116.06, 555.23) * mm, "end": v(-98.06, 555.23) * mm});
            skLineSegment(sketch, "E363", {"start": v(-98.06, 555.23) * mm, "end": v(-98.06, 674.73) * mm});
            skLineSegment(sketch, "E364", {"start": v(-98.06, 674.73) * mm, "end": v(-116.06, 674.73) * mm});
            skArc(sketch, "E365", {"start": v(-116.06, 674.73) * mm, "mid": v(-119.07, 677.74) * mm, "end": v(-116.06, 680.75) * mm});
            skLineSegment(sketch, "E366", {"start": v(-116.06, 680.75) * mm, "end": v(-116.06, 849.2) * mm});
            skArc(sketch, "E367", {"start": v(-116.06, 849.2) * mm, "mid": v(-119.07, 852.22) * mm, "end": v(-116.06, 855.23) * mm});
            skLineSegment(sketch, "E368", {"start": v(-116.06, 855.23) * mm, "end": v(-98.06, 855.23) * mm});
            skLineSegment(sketch, "E369", {"start": v(-98.06, 855.23) * mm, "end": v(-98.06, 974.73) * mm});
            skLineSegment(sketch, "E370", {"start": v(-98.06, 974.73) * mm, "end": v(-116.06, 974.73) * mm});
            skArc(sketch, "E371", {"start": v(-116.06, 974.73) * mm, "mid": v(-119.07, 977.74) * mm, "end": v(-116.06, 980.75) * mm});
            skLineSegment(sketch, "E372", {"start": v(-116.06, 980.75) * mm, "end": v(-116.06, 1141.42) * mm});
            skLineSegment(sketch, "E373", {"start": v(-116.06, 1141.42) * mm, "end": v(-160.56, 1141.42) * mm});
            skLineSegment(sketch, "E374", {"start": v(-160.56, 1141.42) * mm, "end": v(-160.56, 1091.42) * mm});
            skArc(sketch, "E375", {"start": v(-160.56, 1091.42) * mm, "mid": v(-163.57, 1088.41) * mm, "end": v(-166.58, 1091.42) * mm});
            skLineSegment(sketch, "E376", {"start": v(-166.58, 1091.42) * mm, "end": v(-215.04, 1091.42) * mm});
            skArc(sketch, "E377", {"start": v(-215.04, 1091.42) * mm, "mid": v(-218.05, 1088.41) * mm, "end": v(-221.06, 1091.42) * mm});
            skLineSegment(sketch, "E378", {"start": v(-221.06, 1091.42) * mm, "end": v(-221.06, 1141.42) * mm});
            skLineSegment(sketch, "E379", {"start": v(-221.06, 1141.42) * mm, "end": v(-260.56, 1141.42) * mm});
            skLineSegment(sketch, "E380", {"start": v(-260.56, 1141.42) * mm, "end": v(-260.56, 1091.42) * mm});
            skArc(sketch, "E381", {"start": v(-260.56, 1091.42) * mm, "mid": v(-263.57, 1088.41) * mm, "end": v(-266.58, 1091.42) * mm});
            skLineSegment(sketch, "E382", {"start": v(-266.58, 1091.42) * mm, "end": v(-315.04, 1091.42) * mm});
            skArc(sketch, "E383", {"start": v(-315.04, 1091.42) * mm, "mid": v(-318.05, 1088.41) * mm, "end": v(-321.06, 1091.42) * mm});
            skLineSegment(sketch, "E384", {"start": v(-321.06, 1091.42) * mm, "end": v(-321.06, 1141.42) * mm});
            skLineSegment(sketch, "E385", {"start": v(-321.06, 1141.42) * mm, "end": v(-365.56, 1141.42) * mm});
            skLineSegment(sketch, "E386", {"start": v(-365.56, 1141.42) * mm, "end": v(-365.56, 980.75) * mm});
            skArc(sketch, "E387", {"start": v(-365.56, 980.75) * mm, "mid": v(-362.55, 977.74) * mm, "end": v(-365.56, 974.73) * mm});
            skLineSegment(sketch, "E388", {"start": v(-365.56, 974.73) * mm, "end": v(-383.56, 974.73) * mm});
            skLineSegment(sketch, "E389", {"start": v(-383.56, 974.73) * mm, "end": v(-383.56, 855.23) * mm});
            skLineSegment(sketch, "E390", {"start": v(-383.56, 855.23) * mm, "end": v(-365.56, 855.23) * mm});
            skArc(sketch, "E391", {"start": v(-365.56, 855.23) * mm, "mid": v(-362.55, 852.22) * mm, "end": v(-365.56, 849.2) * mm});
            skLineSegment(sketch, "E392", {"start": v(-365.56, 849.2) * mm, "end": v(-365.56, 680.75) * mm});
            skArc(sketch, "E393", {"start": v(-365.56, 680.75) * mm, "mid": v(-362.55, 677.74) * mm, "end": v(-365.56, 674.73) * mm});
            skLineSegment(sketch, "E394", {"start": v(-365.56, 674.73) * mm, "end": v(-383.56, 674.73) * mm});
            skLineSegment(sketch, "E395", {"start": v(-383.56, 674.73) * mm, "end": v(-383.56, 555.23) * mm});
            skLineSegment(sketch, "E396", {"start": v(-383.56, 555.23) * mm, "end": v(-365.56, 555.23) * mm});
            skArc(sketch, "E397", {"start": v(-365.56, 555.23) * mm, "mid": v(-362.55, 552.22) * mm, "end": v(-365.56, 549.2) * mm});
            skLineSegment(sketch, "E398", {"start": v(-365.56, 549.2) * mm, "end": v(-365.56, 380.75) * mm});
            skArc(sketch, "E399", {"start": v(-365.56, 380.75) * mm, "mid": v(-362.55, 377.74) * mm, "end": v(-365.56, 374.73) * mm});
            skLineSegment(sketch, "E400", {"start": v(-365.56, 374.73) * mm, "end": v(-383.56, 374.73) * mm});
            skLineSegment(sketch, "E401", {"start": v(-383.56, 374.73) * mm, "end": v(-383.56, 255.23) * mm});
            skLineSegment(sketch, "E402", {"start": v(-383.56, 255.23) * mm, "end": v(-365.56, 255.23) * mm});
            skArc(sketch, "E403", {"start": v(-365.56, 255.23) * mm, "mid": v(-362.55, 252.22) * mm, "end": v(-365.56, 249.2) * mm});
            skLineSegment(sketch, "E404", {"start": v(-365.56, 249.2) * mm, "end": v(-365.56, 151.91) * mm});
            skLineSegment(sketch, "E405", {"start": v(-365.56, 151.91) * mm, "end": v(-321.58, 151.91) * mm});
            skArc(sketch, "E406", {"start": v(-321.58, 151.91) * mm, "mid": v(-318.57, 154.92) * mm, "end": v(-315.56, 151.91) * mm});
            skLineSegment(sketch, "E407", {"start": v(-315.56, 151.91) * mm, "end": v(-315.56, -8.09) * mm});
            skArc(sketch, "E408", {"start": v(-315.56, -8.09) * mm, "mid": v(-318.37, -10.9) * mm, "end": v(-321.18, -8.09) * mm});
            skLineSegment(sketch, "E409", {"start": v(-321.18, -8.09) * mm, "end": v(-365.56, -8.09) * mm});
            skLineSegment(sketch, "E410", {"start": v(-365.56, -8.09) * mm, "end": v(-365.56, -105.89) * mm});
            skArc(sketch, "E411", {"start": v(-365.56, -105.89) * mm, "mid": v(-362.55, -108.9) * mm, "end": v(-365.56, -111.9) * mm});
            skLineSegment(sketch, "E412", {"start": v(-365.56, -111.9) * mm, "end": v(-383.56, -111.9) * mm});
            skLineSegment(sketch, "E413", {"start": v(-383.56, -111.9) * mm, "end": v(-383.56, -231.4) * mm});
            skLineSegment(sketch, "E414", {"start": v(-383.56, -231.4) * mm, "end": v(-371.58, -231.4) * mm});
            skArc(sketch, "E415", {"start": v(-371.58, -231.4) * mm, "mid": v(-368.57, -228.4) * mm, "end": v(-365.56, -231.4) * mm});
            skLineSegment(sketch, "E416", {"start": v(-365.56, -231.4) * mm, "end": v(-365.56, -244.71) * mm});
            skLineSegment(sketch, "E417", {"start": v(-365.56, -244.71) * mm, "end": v(-326.58, -244.71) * mm});
            skArc(sketch, "E418", {"start": v(-326.58, -244.71) * mm, "mid": v(-323.57, -241.7) * mm, "end": v(-320.56, -244.71) * mm});
            skLineSegment(sketch, "E419", {"start": v(-320.56, -244.71) * mm, "end": v(-320.56, -294.71) * mm});
            skLineSegment(sketch, "E420", {"start": v(-320.56, -294.71) * mm, "end": v(-261.06, -294.71) * mm});
            skLineSegment(sketch, "E421", {"start": v(-261.06, -294.71) * mm, "end": v(-261.06, -244.71) * mm});
            skArc(sketch, "E422", {"start": v(-261.06, -244.71) * mm, "mid": v(-258.05, -241.7) * mm, "end": v(-255.04, -244.71) * mm});
            skLineSegment(sketch, "E423", {"start": v(-255.04, -244.71) * mm, "end": v(-226.58, -244.71) * mm});
            skArc(sketch, "E424", {"start": v(-226.58, -244.71) * mm, "mid": v(-223.57, -241.7) * mm, "end": v(-220.56, -244.71) * mm});
            skLineSegment(sketch, "E425", {"start": v(-220.56, -244.71) * mm, "end": v(-220.56, -294.71) * mm});
            skLineSegment(sketch, "E426", {"start": v(-220.56, -294.71) * mm, "end": v(-161.06, -294.71) * mm});
            skLineSegment(sketch, "E427", {"start": v(-161.06, -294.71) * mm, "end": v(-161.06, -244.71) * mm});
            skArc(sketch, "E428", {"start": v(-161.06, -244.71) * mm, "mid": v(-158.05, -241.7) * mm, "end": v(-155.04, -244.71) * mm});
            skLineSegment(sketch, "E429", {"start": v(-155.04, -244.71) * mm, "end": v(-116.06, -244.71) * mm});
            skLineSegment(sketch, "E430", {"start": v(-116.06, -244.71) * mm, "end": v(-116.06, -237.43) * mm});
            skArc(sketch, "E431", {"start": v(-116.06, -237.43) * mm, "mid": v(-119.07, -234.42) * mm, "end": v(-116.06, -231.4) * mm});
            skLineSegment(sketch, "E432", {"start": v(-116.06, -231.4) * mm, "end": v(-98.06, -231.4) * mm});
            skLineSegment(sketch, "E433", {"start": v(-98.06, -231.4) * mm, "end": v(-98.06, -111.9) * mm});
            skLineSegment(sketch, "E434", {"start": v(434.37, 1055.75) * mm, "end": v(434.37, 982.85) * mm});
            skLineSegment(sketch, "E435", {"start": v(434.37, 982.85) * mm, "end": v(318.37, 982.85) * mm});
            skLineSegment(sketch, "E436", {"start": v(318.37, 982.85) * mm, "end": v(318.37, 1131.65) * mm});
            skLineSegment(sketch, "E437", {"start": v(318.37, 1131.65) * mm, "end": v(568.17, 1131.65) * mm});
            skLineSegment(sketch, "E438", {"start": v(568.17, 1131.65) * mm, "end": v(568.17, 982.85) * mm});
            skLineSegment(sketch, "E439", {"start": v(568.17, 982.85) * mm, "end": v(452.17, 982.85) * mm});
            skLineSegment(sketch, "E440", {"start": v(452.17, 982.85) * mm, "end": v(452.17, 1055.75) * mm});
            skArc(sketch, "E441", {"start": v(452.17, 1055.75) * mm, "mid": v(451.26, 1057.94) * mm, "end": v(449.07, 1058.85) * mm});
            skLineSegment(sketch, "E442", {"start": v(449.07, 1058.85) * mm, "end": v(437.47, 1058.85) * mm});
            skArc(sketch, "E443", {"start": v(437.47, 1058.85) * mm, "mid": v(435.28, 1057.94) * mm, "end": v(434.37, 1055.75) * mm});
            skLineSegment(sketch, "E444", {"start": v(-10.35, -865.53) * mm, "end": v(-1.35, -881.12) * mm});
            skLineSegment(sketch, "E445", {"start": v(-1.35, -881.12) * mm, "end": v(-36, -901.12) * mm});
            skLineSegment(sketch, "E446", {"start": v(-36, -901.12) * mm, "end": v(-45, -885.53) * mm});
            skLineSegment(sketch, "E447", {"start": v(-45, -885.53) * mm, "end": v(-10.35, -865.53) * mm});
            skLineSegment(sketch, "E448", {"start": v(-126.35, -664.62) * mm, "end": v(-117.35, -680.2) * mm});
            skLineSegment(sketch, "E449", {"start": v(-117.35, -680.2) * mm, "end": v(-152, -700.2) * mm});
            skLineSegment(sketch, "E450", {"start": v(-152, -700.2) * mm, "end": v(-161, -684.62) * mm});
            skLineSegment(sketch, "E451", {"start": v(-161, -684.62) * mm, "end": v(-126.35, -664.62) * mm});
            skLineSegment(sketch, "E452", {"start": v(249.46, -715.53) * mm, "end": v(258.46, -731.12) * mm});
            skLineSegment(sketch, "E453", {"start": v(258.46, -731.12) * mm, "end": v(223.82, -751.12) * mm});
            skLineSegment(sketch, "E454", {"start": v(223.82, -751.12) * mm, "end": v(214.82, -735.53) * mm});
            skLineSegment(sketch, "E455", {"start": v(214.82, -735.53) * mm, "end": v(249.46, -715.53) * mm});
            skLineSegment(sketch, "E456", {"start": v(133.46, -514.62) * mm, "end": v(142.46, -530.2) * mm});
            skLineSegment(sketch, "E457", {"start": v(142.46, -530.2) * mm, "end": v(107.82, -550.2) * mm});
            skLineSegment(sketch, "E458", {"start": v(107.82, -550.2) * mm, "end": v(98.82, -534.62) * mm});
            skLineSegment(sketch, "E459", {"start": v(98.82, -534.62) * mm, "end": v(133.46, -514.62) * mm});
            skLineSegment(sketch, "E460", {"start": v(509.27, -565.53) * mm, "end": v(518.27, -581.12) * mm});
            skLineSegment(sketch, "E461", {"start": v(518.27, -581.12) * mm, "end": v(483.62, -601.12) * mm});
            skLineSegment(sketch, "E462", {"start": v(483.62, -601.12) * mm, "end": v(474.62, -585.53) * mm});
            skLineSegment(sketch, "E463", {"start": v(474.62, -585.53) * mm, "end": v(509.27, -565.53) * mm});
            skLineSegment(sketch, "E464", {"start": v(554.16, -447.78) * mm, "end": v(572.16, -447.78) * mm});
            skLineSegment(sketch, "E465", {"start": v(572.16, -447.78) * mm, "end": v(572.16, -487.78) * mm});
            skLineSegment(sketch, "E466", {"start": v(572.16, -487.78) * mm, "end": v(554.16, -487.78) * mm});
            skLineSegment(sketch, "E467", {"start": v(554.16, -487.78) * mm, "end": v(554.16, -447.78) * mm});
            skLineSegment(sketch, "E468", {"start": v(340.16, 712.22) * mm, "end": v(322.16, 712.22) * mm});
            skLineSegment(sketch, "E469", {"start": v(322.16, 712.22) * mm, "end": v(322.16, 752.22) * mm});
            skLineSegment(sketch, "E470", {"start": v(322.16, 752.22) * mm, "end": v(340.16, 752.22) * mm});
            skLineSegment(sketch, "E471", {"start": v(340.16, 752.22) * mm, "end": v(340.16, 712.22) * mm});
            skLineSegment(sketch, "E472", {"start": v(427.16, 723.22) * mm, "end": v(427.16, 741.22) * mm});
            skLineSegment(sketch, "E473", {"start": v(427.16, 741.22) * mm, "end": v(467.16, 741.22) * mm});
            skLineSegment(sketch, "E474", {"start": v(467.16, 741.22) * mm, "end": v(467.16, 723.22) * mm});
            skLineSegment(sketch, "E475", {"start": v(467.16, 723.22) * mm, "end": v(427.16, 723.22) * mm});
            skLineSegment(sketch, "E476", {"start": v(554.16, 712.22) * mm, "end": v(554.16, 752.22) * mm});
            skLineSegment(sketch, "E477", {"start": v(554.16, 752.22) * mm, "end": v(572.16, 752.22) * mm});
            skLineSegment(sketch, "E478", {"start": v(572.16, 752.22) * mm, "end": v(572.16, 712.22) * mm});
            skLineSegment(sketch, "E479", {"start": v(572.16, 712.22) * mm, "end": v(554.16, 712.22) * mm});
            skLineSegment(sketch, "E480", {"start": v(340.16, -147.78) * mm, "end": v(340.16, -187.78) * mm});
            skLineSegment(sketch, "E481", {"start": v(340.16, -187.78) * mm, "end": v(322.16, -187.78) * mm});
            skLineSegment(sketch, "E482", {"start": v(322.16, -187.78) * mm, "end": v(322.16, -147.78) * mm});
            skLineSegment(sketch, "E483", {"start": v(322.16, -147.78) * mm, "end": v(340.16, -147.78) * mm});
            skLineSegment(sketch, "E484", {"start": v(554.16, -147.78) * mm, "end": v(572.16, -147.78) * mm});
            skLineSegment(sketch, "E485", {"start": v(572.16, -147.78) * mm, "end": v(572.16, -187.78) * mm});
            skLineSegment(sketch, "E486", {"start": v(572.16, -187.78) * mm, "end": v(554.16, -187.78) * mm});
            skLineSegment(sketch, "E487", {"start": v(554.16, -187.78) * mm, "end": v(554.16, -147.78) * mm});
            skLineSegment(sketch, "E488", {"start": v(340.16, 412.22) * mm, "end": v(322.16, 412.22) * mm});
            skLineSegment(sketch, "E489", {"start": v(322.16, 412.22) * mm, "end": v(322.16, 452.22) * mm});
            skLineSegment(sketch, "E490", {"start": v(322.16, 452.22) * mm, "end": v(340.16, 452.22) * mm});
            skLineSegment(sketch, "E491", {"start": v(340.16, 452.22) * mm, "end": v(340.16, 412.22) * mm});
            skLineSegment(sketch, "E492", {"start": v(554.16, 412.22) * mm, "end": v(554.16, 452.22) * mm});
            skLineSegment(sketch, "E493", {"start": v(554.16, 452.22) * mm, "end": v(572.16, 452.22) * mm});
            skLineSegment(sketch, "E494", {"start": v(572.16, 452.22) * mm, "end": v(572.16, 412.22) * mm});
            skLineSegment(sketch, "E495", {"start": v(572.16, 412.22) * mm, "end": v(554.16, 412.22) * mm});
            skLineSegment(sketch, "E496", {"start": v(340.16, 152.22) * mm, "end": v(340.16, 112.22) * mm});
            skLineSegment(sketch, "E497", {"start": v(340.16, 112.22) * mm, "end": v(322.16, 112.22) * mm});
            skLineSegment(sketch, "E498", {"start": v(322.16, 112.22) * mm, "end": v(322.16, 152.22) * mm});
            skLineSegment(sketch, "E499", {"start": v(322.16, 152.22) * mm, "end": v(340.16, 152.22) * mm});
            skLineSegment(sketch, "E500", {"start": v(554.16, 152.22) * mm, "end": v(572.16, 152.22) * mm});
            skLineSegment(sketch, "E501", {"start": v(572.16, 152.22) * mm, "end": v(572.16, 112.22) * mm});
            skLineSegment(sketch, "E502", {"start": v(572.16, 112.22) * mm, "end": v(554.16, 112.22) * mm});
            skLineSegment(sketch, "E503", {"start": v(554.16, 112.22) * mm, "end": v(554.16, 152.22) * mm});
            skArc(sketch, "E504", {"start": v(285.62, -536.17) * mm, "mid": v(284.36, -540.52) * mm, "end": v(288.66, -541.94) * mm});
            skLineSegment(sketch, "E505", {"start": v(288.66, -541.94) * mm, "end": v(312.4, -583.05) * mm});
            skArc(sketch, "E506", {"start": v(312.4, -583.05) * mm, "mid": v(311.48, -587.48) * mm, "end": v(315.87, -588.57) * mm});
            skLineSegment(sketch, "E507", {"start": v(315.87, -588.57) * mm, "end": v(331.46, -579.57) * mm});
            skArc(sketch, "E508", {"start": v(331.46, -579.57) * mm, "mid": v(332.72, -575.22) * mm, "end": v(328.42, -573.8) * mm});
            skLineSegment(sketch, "E509", {"start": v(328.42, -573.8) * mm, "end": v(304.69, -532.7) * mm});
            skArc(sketch, "E510", {"start": v(304.69, -532.7) * mm, "mid": v(305.6, -528.26) * mm, "end": v(301.2, -527.17) * mm});
            skLineSegment(sketch, "E511", {"start": v(301.2, -527.17) * mm, "end": v(285.62, -536.17) * mm});
            skArc(sketch, "E512", {"start": v(416.9, -326.77) * mm, "mid": v(420.05, -330.04) * mm, "end": v(423.43, -327.02) * mm});
            skLineSegment(sketch, "E513", {"start": v(423.43, -327.02) * mm, "end": v(470.9, -327.02) * mm});
            skArc(sketch, "E514", {"start": v(470.9, -327.02) * mm, "mid": v(474.27, -330.03) * mm, "end": v(477.41, -326.77) * mm});
            skLineSegment(sketch, "E515", {"start": v(477.41, -326.77) * mm, "end": v(477.41, -308.77) * mm});
            skArc(sketch, "E516", {"start": v(477.41, -308.77) * mm, "mid": v(474.27, -305.5) * mm, "end": v(470.9, -308.52) * mm});
            skLineSegment(sketch, "E517", {"start": v(470.9, -308.52) * mm, "end": v(423.43, -308.52) * mm});
            skArc(sketch, "E518", {"start": v(423.43, -308.52) * mm, "mid": v(420.05, -305.52) * mm, "end": v(416.9, -308.77) * mm});
            skLineSegment(sketch, "E519", {"start": v(416.9, -308.77) * mm, "end": v(416.9, -326.77) * mm});
            skLineSegment(sketch, "E520", {"start": v(-314.92, -692.55) * mm, "end": v(-305.92, -708.14) * mm});
            skLineSegment(sketch, "E521", {"start": v(-305.92, -708.14) * mm, "end": v(-340.56, -728.14) * mm});
            skLineSegment(sketch, "E522", {"start": v(-340.56, -728.14) * mm, "end": v(-349.56, -712.55) * mm});
            skLineSegment(sketch, "E523", {"start": v(-349.56, -712.55) * mm, "end": v(-314.92, -692.55) * mm});
            skLineSegment(sketch, "E524", {"start": v(-430.92, -491.63) * mm, "end": v(-421.92, -507.22) * mm});
            skLineSegment(sketch, "E525", {"start": v(-421.92, -507.22) * mm, "end": v(-456.56, -527.22) * mm});
            skLineSegment(sketch, "E526", {"start": v(-456.56, -527.22) * mm, "end": v(-465.56, -511.63) * mm});
            skLineSegment(sketch, "E527", {"start": v(-465.56, -511.63) * mm, "end": v(-430.92, -491.63) * mm});
            skLineSegment(sketch, "E528", {"start": v(35.6, 885.2) * mm, "end": v(17.6, 885.2) * mm});
            skLineSegment(sketch, "E529", {"start": v(17.6, 885.2) * mm, "end": v(17.6, 925.2) * mm});
            skLineSegment(sketch, "E530", {"start": v(17.6, 925.2) * mm, "end": v(35.6, 925.2) * mm});
            skLineSegment(sketch, "E531", {"start": v(35.6, 925.2) * mm, "end": v(35.6, 885.2) * mm});
            skLineSegment(sketch, "E532", {"start": v(162.6, 896.2) * mm, "end": v(122.6, 896.2) * mm});
            skLineSegment(sketch, "E533", {"start": v(122.6, 896.2) * mm, "end": v(122.6, 914.2) * mm});
            skLineSegment(sketch, "E534", {"start": v(122.6, 914.2) * mm, "end": v(162.6, 914.2) * mm});
            skLineSegment(sketch, "E535", {"start": v(162.6, 914.2) * mm, "end": v(162.6, 896.2) * mm});
            skLineSegment(sketch, "E536", {"start": v(249.6, 885.2) * mm, "end": v(249.6, 925.2) * mm});
            skLineSegment(sketch, "E537", {"start": v(249.6, 925.2) * mm, "end": v(267.6, 925.2) * mm});
            skLineSegment(sketch, "E538", {"start": v(267.6, 925.2) * mm, "end": v(267.6, 885.2) * mm});
            skLineSegment(sketch, "E539", {"start": v(267.6, 885.2) * mm, "end": v(249.6, 885.2) * mm});
            skLineSegment(sketch, "E540", {"start": v(-55.11, -542.55) * mm, "end": v(-46.11, -558.14) * mm});
            skLineSegment(sketch, "E541", {"start": v(-46.11, -558.14) * mm, "end": v(-80.75, -578.14) * mm});
            skLineSegment(sketch, "E542", {"start": v(-80.75, -578.14) * mm, "end": v(-89.75, -562.55) * mm});
            skLineSegment(sketch, "E543", {"start": v(-89.75, -562.55) * mm, "end": v(-55.11, -542.55) * mm});
            skLineSegment(sketch, "E544", {"start": v(-171.11, -341.63) * mm, "end": v(-162.11, -357.22) * mm});
            skLineSegment(sketch, "E545", {"start": v(-162.11, -357.22) * mm, "end": v(-196.75, -377.22) * mm});
            skLineSegment(sketch, "E546", {"start": v(-196.75, -377.22) * mm, "end": v(-205.75, -361.63) * mm});
            skLineSegment(sketch, "E547", {"start": v(-205.75, -361.63) * mm, "end": v(-171.11, -341.63) * mm});
            skLineSegment(sketch, "E548", {"start": v(204.7, -392.55) * mm, "end": v(213.7, -408.14) * mm});
            skLineSegment(sketch, "E549", {"start": v(213.7, -408.14) * mm, "end": v(179.05, -428.14) * mm});
            skLineSegment(sketch, "E550", {"start": v(179.05, -428.14) * mm, "end": v(170.05, -412.55) * mm});
            skLineSegment(sketch, "E551", {"start": v(170.05, -412.55) * mm, "end": v(204.7, -392.55) * mm});
            skLineSegment(sketch, "E552", {"start": v(35.6, 585.2) * mm, "end": v(17.6, 585.2) * mm});
            skLineSegment(sketch, "E553", {"start": v(17.6, 585.2) * mm, "end": v(17.6, 625.2) * mm});
            skLineSegment(sketch, "E554", {"start": v(17.6, 625.2) * mm, "end": v(35.6, 625.2) * mm});
            skLineSegment(sketch, "E555", {"start": v(35.6, 625.2) * mm, "end": v(35.6, 585.2) * mm});
            skLineSegment(sketch, "E556", {"start": v(249.6, 585.2) * mm, "end": v(249.6, 625.2) * mm});
            skLineSegment(sketch, "E557", {"start": v(249.6, 625.2) * mm, "end": v(267.6, 625.2) * mm});
            skLineSegment(sketch, "E558", {"start": v(267.6, 625.2) * mm, "end": v(267.6, 585.2) * mm});
            skLineSegment(sketch, "E559", {"start": v(267.6, 585.2) * mm, "end": v(249.6, 585.2) * mm});
            skLineSegment(sketch, "E560", {"start": v(249.6, -274.8) * mm, "end": v(267.6, -274.8) * mm});
            skLineSegment(sketch, "E561", {"start": v(267.6, -274.8) * mm, "end": v(267.6, -314.8) * mm});
            skLineSegment(sketch, "E562", {"start": v(267.6, -314.8) * mm, "end": v(249.6, -314.8) * mm});
            skLineSegment(sketch, "E563", {"start": v(249.6, -314.8) * mm, "end": v(249.6, -274.8) * mm});
            skLineSegment(sketch, "E564", {"start": v(35.6, 285.2) * mm, "end": v(17.6, 285.2) * mm});
            skLineSegment(sketch, "E565", {"start": v(17.6, 285.2) * mm, "end": v(17.6, 325.2) * mm});
            skLineSegment(sketch, "E566", {"start": v(17.6, 325.2) * mm, "end": v(35.6, 325.2) * mm});
            skLineSegment(sketch, "E567", {"start": v(35.6, 325.2) * mm, "end": v(35.6, 285.2) * mm});
            skLineSegment(sketch, "E568", {"start": v(249.6, 285.2) * mm, "end": v(249.6, 325.2) * mm});
            skLineSegment(sketch, "E569", {"start": v(249.6, 325.2) * mm, "end": v(267.6, 325.2) * mm});
            skLineSegment(sketch, "E570", {"start": v(267.6, 325.2) * mm, "end": v(267.6, 285.2) * mm});
            skLineSegment(sketch, "E571", {"start": v(267.6, 285.2) * mm, "end": v(249.6, 285.2) * mm});
            skLineSegment(sketch, "E572", {"start": v(35.6, 25.2) * mm, "end": v(35.6, -14.8) * mm});
            skLineSegment(sketch, "E573", {"start": v(35.6, -14.8) * mm, "end": v(17.6, -14.8) * mm});
            skLineSegment(sketch, "E574", {"start": v(17.6, -14.8) * mm, "end": v(17.6, 25.2) * mm});
            skLineSegment(sketch, "E575", {"start": v(17.6, 25.2) * mm, "end": v(35.6, 25.2) * mm});
            skLineSegment(sketch, "E576", {"start": v(249.6, 25.2) * mm, "end": v(267.6, 25.2) * mm});
            skLineSegment(sketch, "E577", {"start": v(267.6, 25.2) * mm, "end": v(267.6, -14.8) * mm});
            skLineSegment(sketch, "E578", {"start": v(267.6, -14.8) * mm, "end": v(249.6, -14.8) * mm});
            skLineSegment(sketch, "E579", {"start": v(249.6, -14.8) * mm, "end": v(249.6, 25.2) * mm});
            skArc(sketch, "E580", {"start": v(118.86, -135.54) * mm, "mid": v(115.48, -132.53) * mm, "end": v(112.34, -135.8) * mm});
            skLineSegment(sketch, "E581", {"start": v(112.34, -135.8) * mm, "end": v(112.34, -153.8) * mm});
            skArc(sketch, "E582", {"start": v(112.34, -153.8) * mm, "mid": v(115.48, -157.06) * mm, "end": v(118.86, -154.04) * mm});
            skLineSegment(sketch, "E583", {"start": v(118.86, -154.04) * mm, "end": v(166.32, -154.04) * mm});
            skArc(sketch, "E584", {"start": v(166.32, -154.04) * mm, "mid": v(169.7, -157.05) * mm, "end": v(172.84, -153.8) * mm});
            skLineSegment(sketch, "E585", {"start": v(172.84, -153.8) * mm, "end": v(172.84, -135.8) * mm});
            skArc(sketch, "E586", {"start": v(172.84, -135.8) * mm, "mid": v(169.7, -132.53) * mm, "end": v(166.32, -135.54) * mm});
            skLineSegment(sketch, "E587", {"start": v(166.32, -135.54) * mm, "end": v(118.86, -135.54) * mm});
            skArc(sketch, "E588", {"start": v(-18.95, -363.2) * mm, "mid": v(-20.2, -367.54) * mm, "end": v(-15.9, -368.96) * mm});
            skLineSegment(sketch, "E589", {"start": v(-15.9, -368.96) * mm, "end": v(7.82, -410.07) * mm});
            skArc(sketch, "E590", {"start": v(7.82, -410.07) * mm, "mid": v(6.9, -414.5) * mm, "end": v(11.3, -415.59) * mm});
            skLineSegment(sketch, "E591", {"start": v(11.3, -415.59) * mm, "end": v(26.9, -406.59) * mm});
            skArc(sketch, "E592", {"start": v(26.9, -406.59) * mm, "mid": v(28.15, -402.23) * mm, "end": v(23.85, -400.82) * mm});
            skLineSegment(sketch, "E593", {"start": v(23.85, -400.82) * mm, "end": v(0.12, -359.7) * mm});
            skArc(sketch, "E594", {"start": v(0.12, -359.7) * mm, "mid": v(1.03, -355.28) * mm, "end": v(-3.36, -354.2) * mm});
            skLineSegment(sketch, "E595", {"start": v(-3.36, -354.2) * mm, "end": v(-18.95, -363.2) * mm});
            skLineSegment(sketch, "E596", {"start": v(-216.58, 624.23) * mm, "end": v(-265.04, 624.23) * mm});
            skArc(sketch, "E597", {"start": v(-265.04, 624.23) * mm, "mid": v(-268.05, 627.24) * mm, "end": v(-271.06, 624.23) * mm});
            skLineSegment(sketch, "E598", {"start": v(-271.06, 624.23) * mm, "end": v(-271.06, 605.73) * mm});
            skArc(sketch, "E599", {"start": v(-271.06, 605.73) * mm, "mid": v(-268.05, 602.72) * mm, "end": v(-265.04, 605.73) * mm});
            skLineSegment(sketch, "E600", {"start": v(-265.04, 605.73) * mm, "end": v(-216.58, 605.73) * mm});
            skArc(sketch, "E601", {"start": v(-216.58, 605.73) * mm, "mid": v(-213.57, 602.72) * mm, "end": v(-210.56, 605.73) * mm});
            skLineSegment(sketch, "E602", {"start": v(-210.56, 605.73) * mm, "end": v(-210.56, 624.23) * mm});
            skArc(sketch, "E603", {"start": v(-210.56, 624.23) * mm, "mid": v(-213.57, 627.24) * mm, "end": v(-216.58, 624.23) * mm});
            skLineSegment(sketch, "E604", {"start": v(-216.58, -162.4) * mm, "end": v(-265.04, -162.4) * mm});
            skArc(sketch, "E605", {"start": v(-265.04, -162.4) * mm, "mid": v(-268.05, -159.4) * mm, "end": v(-271.06, -162.4) * mm});
            skLineSegment(sketch, "E606", {"start": v(-271.06, -162.4) * mm, "end": v(-271.06, -180.9) * mm});
            skArc(sketch, "E607", {"start": v(-271.06, -180.9) * mm, "mid": v(-268.05, -183.92) * mm, "end": v(-265.04, -180.9) * mm});
            skLineSegment(sketch, "E608", {"start": v(-265.04, -180.9) * mm, "end": v(-216.58, -180.9) * mm});
            skArc(sketch, "E609", {"start": v(-216.58, -180.9) * mm, "mid": v(-213.57, -183.92) * mm, "end": v(-210.56, -180.9) * mm});
            skLineSegment(sketch, "E610", {"start": v(-210.56, -180.9) * mm, "end": v(-210.56, -162.4) * mm});
            skArc(sketch, "E611", {"start": v(-210.56, -162.4) * mm, "mid": v(-213.57, -159.4) * mm, "end": v(-216.58, -162.4) * mm});
            skLineSegment(sketch, "E612", {"start": v(-216.58, 324.23) * mm, "end": v(-265.04, 324.23) * mm});
            skArc(sketch, "E613", {"start": v(-265.04, 324.23) * mm, "mid": v(-268.05, 327.24) * mm, "end": v(-271.06, 324.23) * mm});
            skLineSegment(sketch, "E614", {"start": v(-271.06, 324.23) * mm, "end": v(-271.06, 305.73) * mm});
            skArc(sketch, "E615", {"start": v(-271.06, 305.73) * mm, "mid": v(-268.05, 302.72) * mm, "end": v(-265.04, 305.73) * mm});
            skLineSegment(sketch, "E616", {"start": v(-265.04, 305.73) * mm, "end": v(-216.58, 305.73) * mm});
            skArc(sketch, "E617", {"start": v(-216.58, 305.73) * mm, "mid": v(-213.57, 302.72) * mm, "end": v(-210.56, 305.73) * mm});
            skLineSegment(sketch, "E618", {"start": v(-210.56, 305.73) * mm, "end": v(-210.56, 324.23) * mm});
            skArc(sketch, "E619", {"start": v(-210.56, 324.23) * mm, "mid": v(-213.57, 327.24) * mm, "end": v(-216.58, 324.23) * mm});
            skLineSegment(sketch, "E620", {"start": v(-220.8, 905.98) * mm, "end": v(-220.8, 923.98) * mm});
            skLineSegment(sketch, "E621", {"start": v(-220.8, 923.98) * mm, "end": v(-260.8, 923.98) * mm});
            skLineSegment(sketch, "E622", {"start": v(-260.8, 923.98) * mm, "end": v(-260.8, 905.98) * mm});
            skLineSegment(sketch, "E623", {"start": v(-260.8, 905.98) * mm, "end": v(-220.8, 905.98) * mm});
            skLineSegment(sketch, "E624", {"start": v(-347.8, 894.98) * mm, "end": v(-347.8, 934.98) * mm});
            skLineSegment(sketch, "E625", {"start": v(-347.8, 934.98) * mm, "end": v(-365.8, 934.98) * mm});
            skLineSegment(sketch, "E626", {"start": v(-365.8, 934.98) * mm, "end": v(-365.8, 894.98) * mm});
            skLineSegment(sketch, "E627", {"start": v(-365.8, 894.98) * mm, "end": v(-347.8, 894.98) * mm});
            skLineSegment(sketch, "E628", {"start": v(-133.8, 894.98) * mm, "end": v(-115.8, 894.98) * mm});
            skLineSegment(sketch, "E629", {"start": v(-115.8, 894.98) * mm, "end": v(-115.8, 934.98) * mm});
            skLineSegment(sketch, "E630", {"start": v(-115.8, 934.98) * mm, "end": v(-133.8, 934.98) * mm});
            skLineSegment(sketch, "E631", {"start": v(-133.8, 934.98) * mm, "end": v(-133.8, 894.98) * mm});
            skLineSegment(sketch, "E632", {"start": v(-347.8, 594.98) * mm, "end": v(-347.8, 634.98) * mm});
            skLineSegment(sketch, "E633", {"start": v(-347.8, 634.98) * mm, "end": v(-365.8, 634.98) * mm});
            skLineSegment(sketch, "E634", {"start": v(-365.8, 634.98) * mm, "end": v(-365.8, 594.98) * mm});
            skLineSegment(sketch, "E635", {"start": v(-365.8, 594.98) * mm, "end": v(-347.8, 594.98) * mm});
            skLineSegment(sketch, "E636", {"start": v(-133.8, 594.98) * mm, "end": v(-115.8, 594.98) * mm});
            skLineSegment(sketch, "E637", {"start": v(-115.8, 594.98) * mm, "end": v(-115.8, 634.98) * mm});
            skLineSegment(sketch, "E638", {"start": v(-115.8, 634.98) * mm, "end": v(-133.8, 634.98) * mm});
            skLineSegment(sketch, "E639", {"start": v(-133.8, 634.98) * mm, "end": v(-133.8, 594.98) * mm});
            skLineSegment(sketch, "E640", {"start": v(-347.8, -151.66) * mm, "end": v(-365.8, -151.66) * mm});
            skLineSegment(sketch, "E641", {"start": v(-365.8, -151.66) * mm, "end": v(-365.8, -191.66) * mm});
            skLineSegment(sketch, "E642", {"start": v(-365.8, -191.66) * mm, "end": v(-347.8, -191.66) * mm});
            skLineSegment(sketch, "E643", {"start": v(-347.8, -191.66) * mm, "end": v(-347.8, -151.66) * mm});
            skLineSegment(sketch, "E644", {"start": v(-133.8, -151.66) * mm, "end": v(-133.8, -191.66) * mm});
            skLineSegment(sketch, "E645", {"start": v(-133.8, -191.66) * mm, "end": v(-115.8, -191.66) * mm});
            skLineSegment(sketch, "E646", {"start": v(-115.8, -191.66) * mm, "end": v(-115.8, -151.66) * mm});
            skLineSegment(sketch, "E647", {"start": v(-115.8, -151.66) * mm, "end": v(-133.8, -151.66) * mm});
            skLineSegment(sketch, "E648", {"start": v(-347.8, 294.98) * mm, "end": v(-347.8, 334.98) * mm});
            skLineSegment(sketch, "E649", {"start": v(-347.8, 334.98) * mm, "end": v(-365.8, 334.98) * mm});
            skLineSegment(sketch, "E650", {"start": v(-365.8, 334.98) * mm, "end": v(-365.8, 294.98) * mm});
            skLineSegment(sketch, "E651", {"start": v(-365.8, 294.98) * mm, "end": v(-347.8, 294.98) * mm});
            skLineSegment(sketch, "E652", {"start": v(-133.8, 294.98) * mm, "end": v(-115.8, 294.98) * mm});
            skLineSegment(sketch, "E653", {"start": v(-115.8, 294.98) * mm, "end": v(-115.8, 334.98) * mm});
            skLineSegment(sketch, "E654", {"start": v(-115.8, 334.98) * mm, "end": v(-133.8, 334.98) * mm});
            skLineSegment(sketch, "E655", {"start": v(-133.8, 334.98) * mm, "end": v(-133.8, 294.98) * mm});
            skLineSegment(sketch, "E656", {"start": v(-133.8, 91.66) * mm, "end": v(-133.8, 51.66) * mm});
            skLineSegment(sketch, "E657", {"start": v(-133.8, 51.66) * mm, "end": v(-115.8, 51.66) * mm});
            skLineSegment(sketch, "E658", {"start": v(-115.8, 51.66) * mm, "end": v(-115.8, 91.66) * mm});
            skLineSegment(sketch, "E659", {"start": v(-115.8, 91.66) * mm, "end": v(-133.8, 91.66) * mm});
            skLineSegment(sketch, "E660", {"start": v(395.4, 38.5) * mm, "end": v(430.03, 58.5) * mm});
            skLineSegment(sketch, "E661", {"start": v(430.03, 58.5) * mm, "end": v(442.46, 36.96) * mm});
            skLineSegment(sketch, "E662", {"start": v(413.48, 48.94) * mm, "end": v(425.02, 28.96) * mm});
            skLineSegment(sketch, "E663", {"start": v(438.56, -36.23) * mm, "end": v(484.42, -35.7) * mm});
            skLineSegment(sketch, "E664", {"start": v(481.53, -85.78) * mm, "end": v(480.97, -86) * mm});
            skLineSegment(sketch, "E665", {"start": v(480.97, -86) * mm, "end": v(480.4, -86.2) * mm});
            skLineSegment(sketch, "E666", {"start": v(480.4, -86.2) * mm, "end": v(479.82, -86.38) * mm});
            skLineSegment(sketch, "E667", {"start": v(479.82, -86.38) * mm, "end": v(479.24, -86.53) * mm});
            skLineSegment(sketch, "E668", {"start": v(479.24, -86.53) * mm, "end": v(478.65, -86.66) * mm});
            skLineSegment(sketch, "E669", {"start": v(478.65, -86.66) * mm, "end": v(478.06, -86.76) * mm});
            skLineSegment(sketch, "E670", {"start": v(478.06, -86.76) * mm, "end": v(477.46, -86.84) * mm});
            skLineSegment(sketch, "E671", {"start": v(477.46, -86.84) * mm, "end": v(476.86, -86.9) * mm});
            skLineSegment(sketch, "E672", {"start": v(476.86, -86.9) * mm, "end": v(476.26, -86.93) * mm});
            skLineSegment(sketch, "E673", {"start": v(476.26, -86.93) * mm, "end": v(475.66, -86.94) * mm});
            skLineSegment(sketch, "E674", {"start": v(475.66, -86.94) * mm, "end": v(475.06, -86.92) * mm});
            skLineSegment(sketch, "E675", {"start": v(475.06, -86.92) * mm, "end": v(474.46, -86.88) * mm});
            skLineSegment(sketch, "E676", {"start": v(474.46, -86.88) * mm, "end": v(473.86, -86.82) * mm});
            skLineSegment(sketch, "E677", {"start": v(473.86, -86.82) * mm, "end": v(473.26, -86.73) * mm});
            skLineSegment(sketch, "E678", {"start": v(473.26, -86.73) * mm, "end": v(472.67, -86.62) * mm});
            skLineSegment(sketch, "E679", {"start": v(472.67, -86.62) * mm, "end": v(472.08, -86.48) * mm});
            skLineSegment(sketch, "E680", {"start": v(472.08, -86.48) * mm, "end": v(471.7, -86.37) * mm});
            skLineSegment(sketch, "E681", {"start": v(471.7, -86.37) * mm, "end": v(471.32, -86.25) * mm});
            skLineSegment(sketch, "E682", {"start": v(471.32, -86.25) * mm, "end": v(470.95, -86.12) * mm});
            skLineSegment(sketch, "E683", {"start": v(470.95, -86.12) * mm, "end": v(470.58, -85.98) * mm});
            skLineSegment(sketch, "E684", {"start": v(470.58, -85.98) * mm, "end": v(470.22, -85.83) * mm});
            skLineSegment(sketch, "E685", {"start": v(470.22, -85.83) * mm, "end": v(469.86, -85.68) * mm});
            skLineSegment(sketch, "E686", {"start": v(469.86, -85.68) * mm, "end": v(469.5, -85.51) * mm});
            skLineSegment(sketch, "E687", {"start": v(469.5, -85.51) * mm, "end": v(469.16, -85.34) * mm});
            skLineSegment(sketch, "E688", {"start": v(469.16, -85.34) * mm, "end": v(468.81, -85.16) * mm});
            skLineSegment(sketch, "E689", {"start": v(468.81, -85.16) * mm, "end": v(468.47, -84.97) * mm});
            skLineSegment(sketch, "E690", {"start": v(468.47, -84.97) * mm, "end": v(468.14, -84.77) * mm});
            skLineSegment(sketch, "E691", {"start": v(468.14, -84.77) * mm, "end": v(467.81, -84.56) * mm});
            skLineSegment(sketch, "E692", {"start": v(467.81, -84.56) * mm, "end": v(467.49, -84.35) * mm});
            skLineSegment(sketch, "E693", {"start": v(467.49, -84.35) * mm, "end": v(467.17, -84.13) * mm});
            skLineSegment(sketch, "E694", {"start": v(467.17, -84.13) * mm, "end": v(466.86, -83.9) * mm});
            skLineSegment(sketch, "E695", {"start": v(466.86, -83.9) * mm, "end": v(466.55, -83.66) * mm});
            skLineSegment(sketch, "E696", {"start": v(466.55, -83.66) * mm, "end": v(466.25, -83.41) * mm});
            skLineSegment(sketch, "E697", {"start": v(466.25, -83.41) * mm, "end": v(465.96, -83.16) * mm});
            skLineSegment(sketch, "E698", {"start": v(465.96, -83.16) * mm, "end": v(465.67, -82.9) * mm});
            skLineSegment(sketch, "E699", {"start": v(465.67, -82.9) * mm, "end": v(465.39, -82.63) * mm});
            skLineSegment(sketch, "E700", {"start": v(465.39, -82.63) * mm, "end": v(465.11, -82.35) * mm});
            skLineSegment(sketch, "E701", {"start": v(465.11, -82.35) * mm, "end": v(464.84, -82.07) * mm});
            skLineSegment(sketch, "E702", {"start": v(464.84, -82.07) * mm, "end": v(464.58, -81.78) * mm});
            skLineSegment(sketch, "E703", {"start": v(464.58, -81.78) * mm, "end": v(464.33, -81.49) * mm});
            skLineSegment(sketch, "E704", {"start": v(464.33, -81.49) * mm, "end": v(464.08, -81.18) * mm});
            skLineSegment(sketch, "E705", {"start": v(464.08, -81.18) * mm, "end": v(463.84, -80.88) * mm});
            skLineSegment(sketch, "E706", {"start": v(463.84, -80.88) * mm, "end": v(463.61, -80.56) * mm});
            skLineSegment(sketch, "E707", {"start": v(463.61, -80.56) * mm, "end": v(463.39, -80.24) * mm});
            skLineSegment(sketch, "E708", {"start": v(463.39, -80.24) * mm, "end": v(463.17, -79.91) * mm});
            skLineSegment(sketch, "E709", {"start": v(463.17, -79.91) * mm, "end": v(462.96, -79.58) * mm});
            skLineSegment(sketch, "E710", {"start": v(462.96, -79.58) * mm, "end": v(462.76, -79.24) * mm});
            skLineSegment(sketch, "E711", {"start": v(462.76, -79.24) * mm, "end": v(462.57, -78.9) * mm});
            skLineSegment(sketch, "E712", {"start": v(462.57, -78.9) * mm, "end": v(462.36, -78.54) * mm});
            skLineSegment(sketch, "E713", {"start": v(462.36, -78.54) * mm, "end": v(462.15, -78.18) * mm});
            skLineSegment(sketch, "E714", {"start": v(462.15, -78.18) * mm, "end": v(461.95, -77.82) * mm});
            skLineSegment(sketch, "E715", {"start": v(461.95, -77.82) * mm, "end": v(461.76, -77.45) * mm});
            skLineSegment(sketch, "E716", {"start": v(461.76, -77.45) * mm, "end": v(461.58, -77.08) * mm});
            skLineSegment(sketch, "E717", {"start": v(461.58, -77.08) * mm, "end": v(461.4, -76.7) * mm});
            skLineSegment(sketch, "E718", {"start": v(461.4, -76.7) * mm, "end": v(461.25, -76.33) * mm});
            skLineSegment(sketch, "E719", {"start": v(461.25, -76.33) * mm, "end": v(461.1, -75.95) * mm});
            skLineSegment(sketch, "E720", {"start": v(461.1, -75.95) * mm, "end": v(460.96, -75.56) * mm});
            skLineSegment(sketch, "E721", {"start": v(460.96, -75.56) * mm, "end": v(460.83, -75.17) * mm});
            skLineSegment(sketch, "E722", {"start": v(460.83, -75.17) * mm, "end": v(460.7, -74.78) * mm});
            skLineSegment(sketch, "E723", {"start": v(460.7, -74.78) * mm, "end": v(460.6, -74.39) * mm});
            skLineSegment(sketch, "E724", {"start": v(460.6, -74.39) * mm, "end": v(460.5, -73.99) * mm});
            skLineSegment(sketch, "E725", {"start": v(460.5, -73.99) * mm, "end": v(460.4, -73.59) * mm});
            skLineSegment(sketch, "E726", {"start": v(460.4, -73.59) * mm, "end": v(460.33, -73.19) * mm});
            skLineSegment(sketch, "E727", {"start": v(460.33, -73.19) * mm, "end": v(460.26, -72.79) * mm});
            skLineSegment(sketch, "E728", {"start": v(460.26, -72.79) * mm, "end": v(460.2, -72.38) * mm});
            skLineSegment(sketch, "E729", {"start": v(460.2, -72.38) * mm, "end": v(460.15, -71.98) * mm});
            skLineSegment(sketch, "E730", {"start": v(460.15, -71.98) * mm, "end": v(460.1, -71.57) * mm});
            skLineSegment(sketch, "E731", {"start": v(460.1, -71.57) * mm, "end": v(460.08, -71.16) * mm});
            skLineSegment(sketch, "E732", {"start": v(460.08, -71.16) * mm, "end": v(460.06, -70.75) * mm});
            skLineSegment(sketch, "E733", {"start": v(460.06, -70.75) * mm, "end": v(460.05, -70.34) * mm});
            skLineSegment(sketch, "E734", {"start": v(460.05, -70.34) * mm, "end": v(460.05, -69.93) * mm});
            skLineSegment(sketch, "E735", {"start": v(460.05, -69.93) * mm, "end": v(460.06, -69.52) * mm});
            skLineSegment(sketch, "E736", {"start": v(460.06, -69.52) * mm, "end": v(460.08, -69.11) * mm});
            skLineSegment(sketch, "E737", {"start": v(460.08, -69.11) * mm, "end": v(460.12, -68.7) * mm});
            skLineSegment(sketch, "E738", {"start": v(460.12, -68.7) * mm, "end": v(460.16, -68.3) * mm});
            skLineSegment(sketch, "E739", {"start": v(460.16, -68.3) * mm, "end": v(460.22, -67.88) * mm});
            skLineSegment(sketch, "E740", {"start": v(460.22, -67.88) * mm, "end": v(460.28, -67.47) * mm});
            skLineSegment(sketch, "E741", {"start": v(460.28, -67.47) * mm, "end": v(460.35, -67.07) * mm});
            skLineSegment(sketch, "E742", {"start": v(460.35, -67.07) * mm, "end": v(460.44, -66.66) * mm});
            skLineSegment(sketch, "E743", {"start": v(460.44, -66.66) * mm, "end": v(460.54, -66.26) * mm});
            skLineSegment(sketch, "E744", {"start": v(460.54, -66.26) * mm, "end": v(460.68, -65.76) * mm});
            skLineSegment(sketch, "E745", {"start": v(460.68, -65.76) * mm, "end": v(460.84, -65.26) * mm});
            skLineSegment(sketch, "E746", {"start": v(460.84, -65.26) * mm, "end": v(461.01, -64.77) * mm});
            skLineSegment(sketch, "E747", {"start": v(461.01, -64.77) * mm, "end": v(461.2, -64.3) * mm});
            skLineSegment(sketch, "E748", {"start": v(461.2, -64.3) * mm, "end": v(461.4, -63.81) * mm});
            skLineSegment(sketch, "E749", {"start": v(461.4, -63.81) * mm, "end": v(461.6, -63.34) * mm});
            skLineSegment(sketch, "E750", {"start": v(461.6, -63.34) * mm, "end": v(461.82, -62.88) * mm});
            skLineSegment(sketch, "E751", {"start": v(461.82, -62.88) * mm, "end": v(462.05, -62.42) * mm});
            skLineSegment(sketch, "E752", {"start": v(462.05, -62.42) * mm, "end": v(462.3, -61.96) * mm});
            skLineSegment(sketch, "E753", {"start": v(462.3, -61.96) * mm, "end": v(462.55, -61.52) * mm});
            skLineSegment(sketch, "E754", {"start": v(462.55, -61.52) * mm, "end": v(462.82, -61.08) * mm});
            skLineSegment(sketch, "E755", {"start": v(462.82, -61.08) * mm, "end": v(463.1, -60.65) * mm});
            skLineSegment(sketch, "E756", {"start": v(463.1, -60.65) * mm, "end": v(463.38, -60.22) * mm});
            skLineSegment(sketch, "E757", {"start": v(463.38, -60.22) * mm, "end": v(463.68, -59.8) * mm});
            skLineSegment(sketch, "E758", {"start": v(463.68, -59.8) * mm, "end": v(463.98, -59.4) * mm});
            skLineSegment(sketch, "E759", {"start": v(463.98, -59.4) * mm, "end": v(464.3, -59) * mm});
            skLineSegment(sketch, "E760", {"start": v(464.3, -59) * mm, "end": v(464.63, -58.6) * mm});
            skLineSegment(sketch, "E761", {"start": v(464.63, -58.6) * mm, "end": v(464.97, -58.21) * mm});
            skLineSegment(sketch, "E762", {"start": v(464.97, -58.21) * mm, "end": v(465.32, -57.84) * mm});
            skLineSegment(sketch, "E763", {"start": v(465.32, -57.84) * mm, "end": v(465.67, -57.47) * mm});
            skLineSegment(sketch, "E764", {"start": v(465.67, -57.47) * mm, "end": v(466.04, -57.11) * mm});
            skLineSegment(sketch, "E765", {"start": v(466.04, -57.11) * mm, "end": v(466.42, -56.76) * mm});
            skLineSegment(sketch, "E766", {"start": v(466.42, -56.76) * mm, "end": v(466.8, -56.42) * mm});
            skLineSegment(sketch, "E767", {"start": v(466.8, -56.42) * mm, "end": v(467.2, -56.1) * mm});
            skLineSegment(sketch, "E768", {"start": v(467.2, -56.1) * mm, "end": v(467.6, -55.77) * mm});
            skLineSegment(sketch, "E769", {"start": v(467.6, -55.77) * mm, "end": v(468, -55.46) * mm});
            skLineSegment(sketch, "E770", {"start": v(468, -55.46) * mm, "end": v(468.43, -55.16) * mm});
            skLineSegment(sketch, "E771", {"start": v(468.43, -55.16) * mm, "end": v(468.86, -54.87) * mm});
            skLineSegment(sketch, "E772", {"start": v(468.86, -54.87) * mm, "end": v(469.3, -54.6) * mm});
            skLineSegment(sketch, "E773", {"start": v(469.3, -54.6) * mm, "end": v(469.73, -54.33) * mm});
            skLineSegment(sketch, "E774", {"start": v(469.73, -54.33) * mm, "end": v(470.19, -54.07) * mm});
            skLineSegment(sketch, "E775", {"start": v(470.19, -54.07) * mm, "end": v(470.64, -53.82) * mm});
            skLineSegment(sketch, "E776", {"start": v(470.64, -53.82) * mm, "end": v(471.15, -53.5) * mm});
            skLineSegment(sketch, "E777", {"start": v(471.15, -53.5) * mm, "end": v(471.66, -53.21) * mm});
            skLineSegment(sketch, "E778", {"start": v(471.66, -53.21) * mm, "end": v(472.18, -52.92) * mm});
            skLineSegment(sketch, "E779", {"start": v(472.18, -52.92) * mm, "end": v(472.71, -52.65) * mm});
            skLineSegment(sketch, "E780", {"start": v(472.71, -52.65) * mm, "end": v(473.24, -52.4) * mm});
            skLineSegment(sketch, "E781", {"start": v(473.24, -52.4) * mm, "end": v(473.78, -52.15) * mm});
            skLineSegment(sketch, "E782", {"start": v(473.78, -52.15) * mm, "end": v(474.32, -51.92) * mm});
            skLineSegment(sketch, "E783", {"start": v(474.32, -51.92) * mm, "end": v(474.87, -51.7) * mm});
            skLineSegment(sketch, "E784", {"start": v(474.87, -51.7) * mm, "end": v(475.42, -51.5) * mm});
            skLineSegment(sketch, "E785", {"start": v(475.42, -51.5) * mm, "end": v(475.98, -51.32) * mm});
            skLineSegment(sketch, "E786", {"start": v(475.98, -51.32) * mm, "end": v(476.54, -51.15) * mm});
            skLineSegment(sketch, "E787", {"start": v(476.54, -51.15) * mm, "end": v(477.1, -50.99) * mm});
            skLineSegment(sketch, "E788", {"start": v(477.1, -50.99) * mm, "end": v(477.68, -50.84) * mm});
            skLineSegment(sketch, "E789", {"start": v(477.68, -50.84) * mm, "end": v(478.25, -50.71) * mm});
            skLineSegment(sketch, "E790", {"start": v(478.25, -50.71) * mm, "end": v(478.82, -50.6) * mm});
            skLineSegment(sketch, "E791", {"start": v(478.82, -50.6) * mm, "end": v(479.4, -50.5) * mm});
            skLineSegment(sketch, "E792", {"start": v(479.4, -50.5) * mm, "end": v(479.98, -50.4) * mm});
            skLineSegment(sketch, "E793", {"start": v(479.98, -50.4) * mm, "end": v(480.56, -50.34) * mm});
            skLineSegment(sketch, "E794", {"start": v(480.56, -50.34) * mm, "end": v(481.15, -50.28) * mm});
            skLineSegment(sketch, "E795", {"start": v(481.15, -50.28) * mm, "end": v(481.73, -50.24) * mm});
            skLineSegment(sketch, "E796", {"start": v(481.73, -50.24) * mm, "end": v(482.32, -50.2) * mm});
            skLineSegment(sketch, "E797", {"start": v(482.32, -50.2) * mm, "end": v(482.9, -50.2) * mm});
            skLineSegment(sketch, "E798", {"start": v(482.9, -50.2) * mm, "end": v(483.5, -50.2) * mm});
            skLineSegment(sketch, "E799", {"start": v(483.5, -50.2) * mm, "end": v(484.08, -50.21) * mm});
            skLineSegment(sketch, "E800", {"start": v(484.08, -50.21) * mm, "end": v(484.67, -50.24) * mm});
            skLineSegment(sketch, "E801", {"start": v(484.67, -50.24) * mm, "end": v(485.26, -50.3) * mm});
            skLineSegment(sketch, "E802", {"start": v(485.26, -50.3) * mm, "end": v(485.84, -50.35) * mm});
            skLineSegment(sketch, "E803", {"start": v(485.84, -50.35) * mm, "end": v(486.43, -50.43) * mm});
            skLineSegment(sketch, "E804", {"start": v(486.43, -50.43) * mm, "end": v(487.02, -50.52) * mm});
            skLineSegment(sketch, "E805", {"start": v(487.02, -50.52) * mm, "end": v(487.6, -50.63) * mm});
            skLineSegment(sketch, "E806", {"start": v(487.6, -50.63) * mm, "end": v(488.18, -50.75) * mm});
            skLineSegment(sketch, "E807", {"start": v(488.18, -50.75) * mm, "end": v(488.76, -50.89) * mm});
            skLineSegment(sketch, "E808", {"start": v(488.76, -50.89) * mm, "end": v(489.14, -51) * mm});
            skLineSegment(sketch, "E809", {"start": v(489.14, -51) * mm, "end": v(489.5, -51.11) * mm});
            skLineSegment(sketch, "E810", {"start": v(489.5, -51.11) * mm, "end": v(489.87, -51.24) * mm});
            skLineSegment(sketch, "E811", {"start": v(489.87, -51.24) * mm, "end": v(490.24, -51.38) * mm});
            skLineSegment(sketch, "E812", {"start": v(490.24, -51.38) * mm, "end": v(490.6, -51.52) * mm});
            skLineSegment(sketch, "E813", {"start": v(490.6, -51.52) * mm, "end": v(490.95, -51.68) * mm});
            skLineSegment(sketch, "E814", {"start": v(490.95, -51.68) * mm, "end": v(491.3, -51.84) * mm});
            skLineSegment(sketch, "E815", {"start": v(491.3, -51.84) * mm, "end": v(491.64, -52.02) * mm});
            skLineSegment(sketch, "E816", {"start": v(491.64, -52.02) * mm, "end": v(491.98, -52.2) * mm});
            skLineSegment(sketch, "E817", {"start": v(491.98, -52.2) * mm, "end": v(492.32, -52.39) * mm});
            skLineSegment(sketch, "E818", {"start": v(492.32, -52.39) * mm, "end": v(492.65, -52.58) * mm});
            skLineSegment(sketch, "E819", {"start": v(492.65, -52.58) * mm, "end": v(492.98, -52.79) * mm});
            skLineSegment(sketch, "E820", {"start": v(492.98, -52.79) * mm, "end": v(493.3, -53) * mm});
            skLineSegment(sketch, "E821", {"start": v(493.3, -53) * mm, "end": v(493.6, -53.22) * mm});
            skLineSegment(sketch, "E822", {"start": v(493.6, -53.22) * mm, "end": v(493.92, -53.45) * mm});
            skLineSegment(sketch, "E823", {"start": v(493.92, -53.45) * mm, "end": v(494.22, -53.7) * mm});
            skLineSegment(sketch, "E824", {"start": v(494.22, -53.7) * mm, "end": v(494.52, -53.94) * mm});
            skLineSegment(sketch, "E825", {"start": v(494.52, -53.94) * mm, "end": v(494.8, -54.19) * mm});
            skLineSegment(sketch, "E826", {"start": v(494.8, -54.19) * mm, "end": v(495.09, -54.45) * mm});
            skLineSegment(sketch, "E827", {"start": v(495.09, -54.45) * mm, "end": v(495.37, -54.71) * mm});
            skLineSegment(sketch, "E828", {"start": v(495.37, -54.71) * mm, "end": v(495.64, -54.99) * mm});
            skLineSegment(sketch, "E829", {"start": v(495.64, -54.99) * mm, "end": v(495.9, -55.27) * mm});
            skLineSegment(sketch, "E830", {"start": v(495.9, -55.27) * mm, "end": v(496.16, -55.55) * mm});
            skLineSegment(sketch, "E831", {"start": v(496.16, -55.55) * mm, "end": v(496.4, -55.85) * mm});
            skLineSegment(sketch, "E832", {"start": v(496.4, -55.85) * mm, "end": v(496.65, -56.15) * mm});
            skLineSegment(sketch, "E833", {"start": v(496.65, -56.15) * mm, "end": v(496.88, -56.46) * mm});
            skLineSegment(sketch, "E834", {"start": v(496.88, -56.46) * mm, "end": v(497.1, -56.77) * mm});
            skLineSegment(sketch, "E835", {"start": v(497.1, -56.77) * mm, "end": v(497.33, -57.09) * mm});
            skLineSegment(sketch, "E836", {"start": v(497.33, -57.09) * mm, "end": v(497.54, -57.41) * mm});
            skLineSegment(sketch, "E837", {"start": v(497.54, -57.41) * mm, "end": v(497.74, -57.74) * mm});
            skLineSegment(sketch, "E838", {"start": v(497.74, -57.74) * mm, "end": v(497.94, -58.08) * mm});
            skLineSegment(sketch, "E839", {"start": v(497.94, -58.08) * mm, "end": v(498.13, -58.42) * mm});
            skLineSegment(sketch, "E840", {"start": v(498.13, -58.42) * mm, "end": v(498.33, -58.76) * mm});
            skLineSegment(sketch, "E841", {"start": v(498.33, -58.76) * mm, "end": v(498.52, -59.1) * mm});
            skLineSegment(sketch, "E842", {"start": v(498.52, -59.1) * mm, "end": v(498.7, -59.43) * mm});
            skLineSegment(sketch, "E843", {"start": v(498.7, -59.43) * mm, "end": v(498.88, -59.78) * mm});
            skLineSegment(sketch, "E844", {"start": v(498.88, -59.78) * mm, "end": v(499.04, -60.13) * mm});
            skLineSegment(sketch, "E845", {"start": v(499.04, -60.13) * mm, "end": v(499.2, -60.48) * mm});
            skLineSegment(sketch, "E846", {"start": v(499.2, -60.48) * mm, "end": v(499.34, -60.83) * mm});
            skLineSegment(sketch, "E847", {"start": v(499.34, -60.83) * mm, "end": v(499.48, -61.2) * mm});
            skLineSegment(sketch, "E848", {"start": v(499.48, -61.2) * mm, "end": v(499.6, -61.55) * mm});
            skLineSegment(sketch, "E849", {"start": v(499.6, -61.55) * mm, "end": v(499.73, -61.92) * mm});
            skLineSegment(sketch, "E850", {"start": v(499.73, -61.92) * mm, "end": v(499.83, -62.28) * mm});
            skLineSegment(sketch, "E851", {"start": v(499.83, -62.28) * mm, "end": v(499.93, -62.65) * mm});
            skLineSegment(sketch, "E852", {"start": v(499.93, -62.65) * mm, "end": v(500.02, -63.03) * mm});
            skLineSegment(sketch, "E853", {"start": v(500.02, -63.03) * mm, "end": v(500.1, -63.4) * mm});
            skLineSegment(sketch, "E854", {"start": v(500.1, -63.4) * mm, "end": v(500.17, -63.77) * mm});
            skLineSegment(sketch, "E855", {"start": v(500.17, -63.77) * mm, "end": v(500.23, -64.15) * mm});
            skLineSegment(sketch, "E856", {"start": v(500.23, -64.15) * mm, "end": v(500.29, -64.53) * mm});
            skLineSegment(sketch, "E857", {"start": v(500.29, -64.53) * mm, "end": v(500.33, -64.91) * mm});
            skLineSegment(sketch, "E858", {"start": v(500.33, -64.91) * mm, "end": v(500.36, -65.3) * mm});
            skLineSegment(sketch, "E859", {"start": v(500.36, -65.3) * mm, "end": v(500.38, -65.67) * mm});
            skLineSegment(sketch, "E860", {"start": v(500.38, -65.67) * mm, "end": v(500.4, -66.05) * mm});
            skLineSegment(sketch, "E861", {"start": v(500.4, -66.05) * mm, "end": v(500.4, -66.44) * mm});
            skLineSegment(sketch, "E862", {"start": v(500.4, -66.44) * mm, "end": v(500.4, -66.82) * mm});
            skLineSegment(sketch, "E863", {"start": v(500.4, -66.82) * mm, "end": v(500.37, -67.2) * mm});
            skLineSegment(sketch, "E864", {"start": v(500.37, -67.2) * mm, "end": v(500.35, -67.59) * mm});
            skLineSegment(sketch, "E865", {"start": v(500.35, -67.59) * mm, "end": v(500.31, -67.97) * mm});
            skLineSegment(sketch, "E866", {"start": v(500.31, -67.97) * mm, "end": v(500.26, -68.35) * mm});
            skLineSegment(sketch, "E867", {"start": v(500.26, -68.35) * mm, "end": v(500.2, -68.73) * mm});
            skLineSegment(sketch, "E868", {"start": v(500.2, -68.73) * mm, "end": v(500.14, -69.11) * mm});
            skLineSegment(sketch, "E869", {"start": v(500.14, -69.11) * mm, "end": v(500.07, -69.5) * mm});
            skLineSegment(sketch, "E870", {"start": v(500.07, -69.5) * mm, "end": v(499.98, -69.87) * mm});
            skLineSegment(sketch, "E871", {"start": v(499.98, -69.87) * mm, "end": v(499.88, -70.25) * mm});
            skLineSegment(sketch, "E872", {"start": v(499.88, -70.25) * mm, "end": v(499.78, -70.68) * mm});
            skLineSegment(sketch, "E873", {"start": v(499.78, -70.68) * mm, "end": v(499.66, -71.12) * mm});
            skLineSegment(sketch, "E874", {"start": v(499.66, -71.12) * mm, "end": v(499.53, -71.54) * mm});
            skLineSegment(sketch, "E875", {"start": v(499.53, -71.54) * mm, "end": v(499.38, -71.96) * mm});
            skLineSegment(sketch, "E876", {"start": v(499.38, -71.96) * mm, "end": v(499.22, -72.38) * mm});
            skLineSegment(sketch, "E877", {"start": v(499.22, -72.38) * mm, "end": v(499.05, -72.8) * mm});
            skLineSegment(sketch, "E878", {"start": v(499.05, -72.8) * mm, "end": v(498.86, -73.2) * mm});
            skLineSegment(sketch, "E879", {"start": v(498.86, -73.2) * mm, "end": v(498.65, -73.6) * mm});
            skLineSegment(sketch, "E880", {"start": v(498.65, -73.6) * mm, "end": v(498.43, -73.98) * mm});
            skLineSegment(sketch, "E881", {"start": v(498.43, -73.98) * mm, "end": v(498.2, -74.36) * mm});
            skLineSegment(sketch, "E882", {"start": v(498.2, -74.36) * mm, "end": v(497.95, -74.74) * mm});
            skLineSegment(sketch, "E883", {"start": v(497.95, -74.74) * mm, "end": v(497.7, -75.1) * mm});
            skLineSegment(sketch, "E884", {"start": v(497.7, -75.1) * mm, "end": v(497.42, -75.46) * mm});
            skLineSegment(sketch, "E885", {"start": v(497.42, -75.46) * mm, "end": v(497.14, -75.8) * mm});
            skLineSegment(sketch, "E886", {"start": v(497.14, -75.8) * mm, "end": v(496.84, -76.14) * mm});
            skLineSegment(sketch, "E887", {"start": v(496.84, -76.14) * mm, "end": v(496.53, -76.46) * mm});
            skLineSegment(sketch, "E888", {"start": v(215.5, 186.42) * mm, "end": v(215.5, 146.43) * mm});
            skLineSegment(sketch, "E889", {"start": v(215.5, 146.43) * mm, "end": v(190.64, 146.43) * mm});
            skLineSegment(sketch, "E890", {"start": v(215.5, 165.54) * mm, "end": v(192.43, 165.54) * mm});
            skLineSegment(sketch, "E891", {"start": v(129.2, 186.4) * mm, "end": v(106.74, 146.43) * mm});
            skLineSegment(sketch, "E892", {"start": v(97.94, 186.4) * mm, "end": v(83.63, 146.4) * mm});
            skLineSegment(sketch, "E893", {"start": v(83.63, 146.4) * mm, "end": v(81.48, 146.4) * mm});
            skLineSegment(sketch, "E894", {"start": v(81.48, 146.4) * mm, "end": v(66.19, 186.4) * mm});
            skLineSegment(sketch, "E895", {"start": v(92.9, 172.41) * mm, "end": v(71.65, 172.41) * mm});
            skLineSegment(sketch, "E896", {"start": v(-467.05, 455.65) * mm, "end": v(-502.05, 455.65) * mm});
            skLineSegment(sketch, "E897", {"start": v(-502.05, 455.65) * mm, "end": v(-502.05, 477.4) * mm});
            skLineSegment(sketch, "E898", {"start": v(-485.33, 455.65) * mm, "end": v(-485.33, 475.83) * mm});
            skLineSegment(sketch, "E899", {"start": v(-467.08, 505.66) * mm, "end": v(-467.08, 485.1) * mm});
            skLineSegment(sketch, "E900", {"start": v(-467.08, 485.1) * mm, "end": v(-502.03, 485.1) * mm});
            skLineSegment(sketch, "E901", {"start": v(-466.59, 518.93) * mm, "end": v(-466.58, 518.56) * mm});
            skLineSegment(sketch, "E902", {"start": v(-466.58, 518.56) * mm, "end": v(-466.59, 518.2) * mm});
            skLineSegment(sketch, "E903", {"start": v(-466.59, 518.2) * mm, "end": v(-466.6, 517.83) * mm});
            skLineSegment(sketch, "E904", {"start": v(-466.6, 517.83) * mm, "end": v(-466.63, 517.46) * mm});
            skLineSegment(sketch, "E905", {"start": v(-466.63, 517.46) * mm, "end": v(-466.66, 517.1) * mm});
            skLineSegment(sketch, "E906", {"start": v(-466.66, 517.1) * mm, "end": v(-466.7, 516.74) * mm});
            skLineSegment(sketch, "E907", {"start": v(-466.7, 516.74) * mm, "end": v(-466.76, 516.38) * mm});
            skLineSegment(sketch, "E908", {"start": v(-466.76, 516.38) * mm, "end": v(-466.82, 516.02) * mm});
            skLineSegment(sketch, "E909", {"start": v(-466.82, 516.02) * mm, "end": v(-466.89, 515.66) * mm});
            skLineSegment(sketch, "E910", {"start": v(-466.89, 515.66) * mm, "end": v(-466.97, 515.3) * mm});
            skLineSegment(sketch, "E911", {"start": v(-466.97, 515.3) * mm, "end": v(-467.05, 514.96) * mm});
            skLineSegment(sketch, "E912", {"start": v(-467.05, 514.96) * mm, "end": v(-467.15, 514.6) * mm});
            skLineSegment(sketch, "E913", {"start": v(-467.15, 514.6) * mm, "end": v(-467.25, 514.26) * mm});
            skLineSegment(sketch, "E914", {"start": v(-467.25, 514.26) * mm, "end": v(-467.37, 513.92) * mm});
            skLineSegment(sketch, "E915", {"start": v(-467.37, 513.92) * mm, "end": v(-467.49, 513.58) * mm});
            skLineSegment(sketch, "E916", {"start": v(-467.49, 513.58) * mm, "end": v(-467.62, 513.24) * mm});
            skLineSegment(sketch, "E917", {"start": v(-467.62, 513.24) * mm, "end": v(-467.76, 512.9) * mm});
            skLineSegment(sketch, "E918", {"start": v(-467.76, 512.9) * mm, "end": v(-467.9, 512.57) * mm});
            skLineSegment(sketch, "E919", {"start": v(-467.9, 512.57) * mm, "end": v(-468.06, 512.25) * mm});
            skLineSegment(sketch, "E920", {"start": v(-468.06, 512.25) * mm, "end": v(-468.22, 511.92) * mm});
            skLineSegment(sketch, "E921", {"start": v(-468.22, 511.92) * mm, "end": v(-468.4, 511.6) * mm});
            skLineSegment(sketch, "E922", {"start": v(-468.4, 511.6) * mm, "end": v(-468.57, 511.29) * mm});
            skLineSegment(sketch, "E923", {"start": v(-468.57, 511.29) * mm, "end": v(-468.76, 510.98) * mm});
            skLineSegment(sketch, "E924", {"start": v(-468.76, 510.98) * mm, "end": v(-468.95, 510.67) * mm});
            skLineSegment(sketch, "E925", {"start": v(-468.95, 510.67) * mm, "end": v(-469.15, 510.37) * mm});
            skLineSegment(sketch, "E926", {"start": v(-469.15, 510.37) * mm, "end": v(-469.36, 510.07) * mm});
            skLineSegment(sketch, "E927", {"start": v(-469.36, 510.07) * mm, "end": v(-469.58, 509.78) * mm});
            skLineSegment(sketch, "E928", {"start": v(-469.58, 509.78) * mm, "end": v(-469.8, 509.5) * mm});
            skLineSegment(sketch, "E929", {"start": v(-469.8, 509.5) * mm, "end": v(-470.04, 509.2) * mm});
            skLineSegment(sketch, "E930", {"start": v(-470.04, 509.2) * mm, "end": v(-470.28, 508.93) * mm});
            skLineSegment(sketch, "E931", {"start": v(-470.28, 508.93) * mm, "end": v(-470.53, 508.66) * mm});
            skLineSegment(sketch, "E932", {"start": v(-470.53, 508.66) * mm, "end": v(-470.78, 508.4) * mm});
            skLineSegment(sketch, "E933", {"start": v(-470.78, 508.4) * mm, "end": v(-471.11, 508.1) * mm});
            skLineSegment(sketch, "E934", {"start": v(-471.11, 508.1) * mm, "end": v(-471.45, 507.8) * mm});
            skLineSegment(sketch, "E935", {"start": v(-471.45, 507.8) * mm, "end": v(-471.8, 507.5) * mm});
            skLineSegment(sketch, "E936", {"start": v(-471.8, 507.5) * mm, "end": v(-472.15, 507.23) * mm});
            skLineSegment(sketch, "E937", {"start": v(-472.15, 507.23) * mm, "end": v(-472.51, 506.96) * mm});
            skLineSegment(sketch, "E938", {"start": v(-472.51, 506.96) * mm, "end": v(-472.88, 506.7) * mm});
            skLineSegment(sketch, "E939", {"start": v(-472.88, 506.7) * mm, "end": v(-473.25, 506.45) * mm});
            skLineSegment(sketch, "E940", {"start": v(-473.25, 506.45) * mm, "end": v(-473.63, 506.2) * mm});
            skLineSegment(sketch, "E941", {"start": v(-473.63, 506.2) * mm, "end": v(-474, 505.97) * mm});
            skLineSegment(sketch, "E942", {"start": v(-474, 505.97) * mm, "end": v(-474.4, 505.75) * mm});
            skLineSegment(sketch, "E943", {"start": v(-474.4, 505.75) * mm, "end": v(-474.79, 505.54) * mm});
            skLineSegment(sketch, "E944", {"start": v(-474.79, 505.54) * mm, "end": v(-475.19, 505.34) * mm});
            skLineSegment(sketch, "E945", {"start": v(-475.19, 505.34) * mm, "end": v(-475.59, 505.15) * mm});
            skLineSegment(sketch, "E946", {"start": v(-475.59, 505.15) * mm, "end": v(-476, 504.96) * mm});
            skLineSegment(sketch, "E947", {"start": v(-476, 504.96) * mm, "end": v(-476.4, 504.8) * mm});
            skLineSegment(sketch, "E948", {"start": v(-476.4, 504.8) * mm, "end": v(-476.82, 504.63) * mm});
            skLineSegment(sketch, "E949", {"start": v(-476.82, 504.63) * mm, "end": v(-477.24, 504.48) * mm});
            skLineSegment(sketch, "E950", {"start": v(-477.24, 504.48) * mm, "end": v(-477.66, 504.34) * mm});
            skLineSegment(sketch, "E951", {"start": v(-477.66, 504.34) * mm, "end": v(-478.09, 504.2) * mm});
            skLineSegment(sketch, "E952", {"start": v(-478.09, 504.2) * mm, "end": v(-478.52, 504.08) * mm});
            skLineSegment(sketch, "E953", {"start": v(-478.52, 504.08) * mm, "end": v(-478.95, 503.97) * mm});
            skLineSegment(sketch, "E954", {"start": v(-478.95, 503.97) * mm, "end": v(-479.38, 503.87) * mm});
            skLineSegment(sketch, "E955", {"start": v(-479.38, 503.87) * mm, "end": v(-479.82, 503.78) * mm});
            skLineSegment(sketch, "E956", {"start": v(-479.82, 503.78) * mm, "end": v(-480.26, 503.7) * mm});
            skLineSegment(sketch, "E957", {"start": v(-480.26, 503.7) * mm, "end": v(-480.7, 503.64) * mm});
            skLineSegment(sketch, "E958", {"start": v(-480.7, 503.64) * mm, "end": v(-481.15, 503.58) * mm});
            skLineSegment(sketch, "E959", {"start": v(-481.15, 503.58) * mm, "end": v(-481.6, 503.54) * mm});
            skLineSegment(sketch, "E960", {"start": v(-481.6, 503.54) * mm, "end": v(-482.04, 503.5) * mm});
            skLineSegment(sketch, "E961", {"start": v(-482.04, 503.5) * mm, "end": v(-482.5, 503.48) * mm});
            skLineSegment(sketch, "E962", {"start": v(-482.5, 503.48) * mm, "end": v(-482.94, 503.46) * mm});
            skLineSegment(sketch, "E963", {"start": v(-482.94, 503.46) * mm, "end": v(-483.4, 503.46) * mm});
            skLineSegment(sketch, "E964", {"start": v(-483.4, 503.46) * mm, "end": v(-483.85, 503.47) * mm});
            skLineSegment(sketch, "E965", {"start": v(-483.85, 503.47) * mm, "end": v(-484.34, 503.46) * mm});
            skLineSegment(sketch, "E966", {"start": v(-484.34, 503.46) * mm, "end": v(-484.83, 503.46) * mm});
            skLineSegment(sketch, "E967", {"start": v(-484.83, 503.46) * mm, "end": v(-485.32, 503.47) * mm});
            skLineSegment(sketch, "E968", {"start": v(-485.32, 503.47) * mm, "end": v(-485.8, 503.5) * mm});
            skLineSegment(sketch, "E969", {"start": v(-485.8, 503.5) * mm, "end": v(-486.29, 503.53) * mm});
            skLineSegment(sketch, "E970", {"start": v(-486.29, 503.53) * mm, "end": v(-486.77, 503.58) * mm});
            skLineSegment(sketch, "E971", {"start": v(-486.77, 503.58) * mm, "end": v(-487.26, 503.64) * mm});
            skLineSegment(sketch, "E972", {"start": v(-487.26, 503.64) * mm, "end": v(-487.74, 503.7) * mm});
            skLineSegment(sketch, "E973", {"start": v(-487.74, 503.7) * mm, "end": v(-488.22, 503.8) * mm});
            skLineSegment(sketch, "E974", {"start": v(-488.22, 503.8) * mm, "end": v(-488.7, 503.89) * mm});
            skLineSegment(sketch, "E975", {"start": v(-488.7, 503.89) * mm, "end": v(-489.16, 504) * mm});
            skLineSegment(sketch, "E976", {"start": v(-489.16, 504) * mm, "end": v(-489.63, 504.11) * mm});
            skLineSegment(sketch, "E977", {"start": v(-489.63, 504.11) * mm, "end": v(-490.1, 504.24) * mm});
            skLineSegment(sketch, "E978", {"start": v(-490.1, 504.24) * mm, "end": v(-490.56, 504.38) * mm});
            skLineSegment(sketch, "E979", {"start": v(-490.56, 504.38) * mm, "end": v(-491.02, 504.54) * mm});
            skLineSegment(sketch, "E980", {"start": v(-491.02, 504.54) * mm, "end": v(-491.48, 504.7) * mm});
            skLineSegment(sketch, "E981", {"start": v(-491.48, 504.7) * mm, "end": v(-491.93, 504.88) * mm});
            skLineSegment(sketch, "E982", {"start": v(-491.93, 504.88) * mm, "end": v(-492.37, 505.07) * mm});
            skLineSegment(sketch, "E983", {"start": v(-492.37, 505.07) * mm, "end": v(-492.81, 505.26) * mm});
            skLineSegment(sketch, "E984", {"start": v(-492.81, 505.26) * mm, "end": v(-493.25, 505.47) * mm});
            skLineSegment(sketch, "E985", {"start": v(-493.25, 505.47) * mm, "end": v(-493.68, 505.7) * mm});
            skLineSegment(sketch, "E986", {"start": v(-493.68, 505.7) * mm, "end": v(-494.1, 505.92) * mm});
            skLineSegment(sketch, "E987", {"start": v(-494.1, 505.92) * mm, "end": v(-494.53, 506.16) * mm});
            skLineSegment(sketch, "E988", {"start": v(-494.53, 506.16) * mm, "end": v(-494.94, 506.42) * mm});
            skLineSegment(sketch, "E989", {"start": v(-494.94, 506.42) * mm, "end": v(-495.35, 506.68) * mm});
            skLineSegment(sketch, "E990", {"start": v(-495.35, 506.68) * mm, "end": v(-495.76, 506.95) * mm});
            skLineSegment(sketch, "E991", {"start": v(-495.76, 506.95) * mm, "end": v(-496.15, 507.23) * mm});
            skLineSegment(sketch, "E992", {"start": v(-496.15, 507.23) * mm, "end": v(-496.54, 507.53) * mm});
            skLineSegment(sketch, "E993", {"start": v(-496.54, 507.53) * mm, "end": v(-496.92, 507.83) * mm});
            skLineSegment(sketch, "E994", {"start": v(-496.92, 507.83) * mm, "end": v(-497.3, 508.15) * mm});
            skLineSegment(sketch, "E995", {"start": v(-497.3, 508.15) * mm, "end": v(-497.67, 508.47) * mm});
            skLineSegment(sketch, "E996", {"start": v(-497.67, 508.47) * mm, "end": v(-498.03, 508.8) * mm});
            skLineSegment(sketch, "E997", {"start": v(-498.03, 508.8) * mm, "end": v(-498.28, 509.05) * mm});
            skLineSegment(sketch, "E998", {"start": v(-498.28, 509.05) * mm, "end": v(-498.53, 509.3) * mm});
            skLineSegment(sketch, "E999", {"start": v(-498.53, 509.3) * mm, "end": v(-498.77, 509.57) * mm});
            skLineSegment(sketch, "E1000", {"start": v(-498.77, 509.57) * mm, "end": v(-499, 509.84) * mm});
            skLineSegment(sketch, "E1001", {"start": v(-499, 509.84) * mm, "end": v(-499.23, 510.11) * mm});
            skLineSegment(sketch, "E1002", {"start": v(-499.23, 510.11) * mm, "end": v(-499.44, 510.4) * mm});
            skLineSegment(sketch, "E1003", {"start": v(-499.44, 510.4) * mm, "end": v(-499.65, 510.67) * mm});
            skLineSegment(sketch, "E1004", {"start": v(-499.65, 510.67) * mm, "end": v(-499.86, 510.96) * mm});
            skLineSegment(sketch, "E1005", {"start": v(-499.86, 510.96) * mm, "end": v(-500.05, 511.26) * mm});
            skLineSegment(sketch, "E1006", {"start": v(-500.05, 511.26) * mm, "end": v(-500.24, 511.55) * mm});
            skLineSegment(sketch, "E1007", {"start": v(-500.24, 511.55) * mm, "end": v(-500.42, 511.86) * mm});
            skLineSegment(sketch, "E1008", {"start": v(-500.42, 511.86) * mm, "end": v(-500.59, 512.16) * mm});
            skLineSegment(sketch, "E1009", {"start": v(-500.59, 512.16) * mm, "end": v(-500.75, 512.47) * mm});
            skLineSegment(sketch, "E1010", {"start": v(-500.75, 512.47) * mm, "end": v(-500.9, 512.79) * mm});
            skLineSegment(sketch, "E1011", {"start": v(-500.9, 512.79) * mm, "end": v(-501.06, 513.1) * mm});
            skLineSegment(sketch, "E1012", {"start": v(-501.06, 513.1) * mm, "end": v(-501.2, 513.43) * mm});
            skLineSegment(sketch, "E1013", {"start": v(-501.2, 513.43) * mm, "end": v(-501.33, 513.76) * mm});
            skLineSegment(sketch, "E1014", {"start": v(-501.33, 513.76) * mm, "end": v(-501.45, 514.08) * mm});
            skLineSegment(sketch, "E1015", {"start": v(-501.45, 514.08) * mm, "end": v(-501.56, 514.42) * mm});
            skLineSegment(sketch, "E1016", {"start": v(-501.56, 514.42) * mm, "end": v(-501.67, 514.75) * mm});
            skLineSegment(sketch, "E1017", {"start": v(-501.67, 514.75) * mm, "end": v(-501.77, 515.09) * mm});
            skLineSegment(sketch, "E1018", {"start": v(-501.77, 515.09) * mm, "end": v(-501.85, 515.43) * mm});
            skLineSegment(sketch, "E1019", {"start": v(-501.85, 515.43) * mm, "end": v(-501.93, 515.77) * mm});
            skLineSegment(sketch, "E1020", {"start": v(-501.93, 515.77) * mm, "end": v(-502, 516.12) * mm});
            skLineSegment(sketch, "E1021", {"start": v(-502, 516.12) * mm, "end": v(-502.07, 516.46) * mm});
            skLineSegment(sketch, "E1022", {"start": v(-502.07, 516.46) * mm, "end": v(-502.12, 516.81) * mm});
            skLineSegment(sketch, "E1023", {"start": v(-502.12, 516.81) * mm, "end": v(-502.17, 517.16) * mm});
            skLineSegment(sketch, "E1024", {"start": v(-502.17, 517.16) * mm, "end": v(-502.2, 517.51) * mm});
            skLineSegment(sketch, "E1025", {"start": v(-502.2, 517.51) * mm, "end": v(-502.23, 517.87) * mm});
            skLineSegment(sketch, "E1026", {"start": v(-502.23, 517.87) * mm, "end": v(-502.24, 518.22) * mm});
            skLineSegment(sketch, "E1027", {"start": v(-502.24, 518.22) * mm, "end": v(-502.25, 518.58) * mm});
            skLineSegment(sketch, "E1028", {"start": v(-502.25, 518.58) * mm, "end": v(-502.25, 518.94) * mm});
            skLineSegment(sketch, "E1029", {"start": v(-502.25, 518.94) * mm, "end": v(-502.25, 519.3) * mm});
            skLineSegment(sketch, "E1030", {"start": v(-502.25, 519.3) * mm, "end": v(-502.23, 519.66) * mm});
            skLineSegment(sketch, "E1031", {"start": v(-502.23, 519.66) * mm, "end": v(-502.21, 520.02) * mm});
            skLineSegment(sketch, "E1032", {"start": v(-502.21, 520.02) * mm, "end": v(-502.18, 520.38) * mm});
            skLineSegment(sketch, "E1033", {"start": v(-502.18, 520.38) * mm, "end": v(-502.14, 520.74) * mm});
            skLineSegment(sketch, "E1034", {"start": v(-502.14, 520.74) * mm, "end": v(-502.1, 521.1) * mm});
            skLineSegment(sketch, "E1035", {"start": v(-502.1, 521.1) * mm, "end": v(-502.03, 521.45) * mm});
            skLineSegment(sketch, "E1036", {"start": v(-502.03, 521.45) * mm, "end": v(-501.96, 521.8) * mm});
            skLineSegment(sketch, "E1037", {"start": v(-501.96, 521.8) * mm, "end": v(-501.89, 522.15) * mm});
            skLineSegment(sketch, "E1038", {"start": v(-501.89, 522.15) * mm, "end": v(-501.8, 522.5) * mm});
            skLineSegment(sketch, "E1039", {"start": v(-501.8, 522.5) * mm, "end": v(-501.7, 522.84) * mm});
            skLineSegment(sketch, "E1040", {"start": v(-501.7, 522.84) * mm, "end": v(-501.6, 523.18) * mm});
            skLineSegment(sketch, "E1041", {"start": v(-501.6, 523.18) * mm, "end": v(-501.5, 523.52) * mm});
            skLineSegment(sketch, "E1042", {"start": v(-501.5, 523.52) * mm, "end": v(-501.37, 523.86) * mm});
            skLineSegment(sketch, "E1043", {"start": v(-501.37, 523.86) * mm, "end": v(-501.24, 524.19) * mm});
            skLineSegment(sketch, "E1044", {"start": v(-501.24, 524.19) * mm, "end": v(-501.1, 524.52) * mm});
            skLineSegment(sketch, "E1045", {"start": v(-501.1, 524.52) * mm, "end": v(-500.96, 524.84) * mm});
            skLineSegment(sketch, "E1046", {"start": v(-500.96, 524.84) * mm, "end": v(-500.8, 525.17) * mm});
            skLineSegment(sketch, "E1047", {"start": v(-500.8, 525.17) * mm, "end": v(-500.65, 525.48) * mm});
            skLineSegment(sketch, "E1048", {"start": v(-500.65, 525.48) * mm, "end": v(-500.48, 525.8) * mm});
            skLineSegment(sketch, "E1049", {"start": v(-500.48, 525.8) * mm, "end": v(-500.3, 526.1) * mm});
            skLineSegment(sketch, "E1050", {"start": v(-500.3, 526.1) * mm, "end": v(-500.11, 526.41) * mm});
            skLineSegment(sketch, "E1051", {"start": v(-500.11, 526.41) * mm, "end": v(-499.92, 526.71) * mm});
            skLineSegment(sketch, "E1052", {"start": v(-499.92, 526.71) * mm, "end": v(-499.72, 527) * mm});
            skLineSegment(sketch, "E1053", {"start": v(-499.72, 527) * mm, "end": v(-499.5, 527.3) * mm});
            skLineSegment(sketch, "E1054", {"start": v(-499.5, 527.3) * mm, "end": v(-499.3, 527.59) * mm});
            skLineSegment(sketch, "E1055", {"start": v(-499.3, 527.59) * mm, "end": v(-499.07, 527.87) * mm});
            skLineSegment(sketch, "E1056", {"start": v(-499.07, 527.87) * mm, "end": v(-498.83, 528.14) * mm});
            skLineSegment(sketch, "E1057", {"start": v(-498.83, 528.14) * mm, "end": v(-498.6, 528.4) * mm});
            skLineSegment(sketch, "E1058", {"start": v(-498.6, 528.4) * mm, "end": v(-498.35, 528.67) * mm});
            skLineSegment(sketch, "E1059", {"start": v(-498.35, 528.67) * mm, "end": v(-498.1, 528.93) * mm});
            skLineSegment(sketch, "E1060", {"start": v(-498.1, 528.93) * mm, "end": v(-497.83, 529.18) * mm});
            skLineSegment(sketch, "E1061", {"start": v(-497.83, 529.18) * mm, "end": v(-497.47, 529.5) * mm});
            skLineSegment(sketch, "E1062", {"start": v(-497.47, 529.5) * mm, "end": v(-497.1, 529.82) * mm});
            skLineSegment(sketch, "E1063", {"start": v(-497.1, 529.82) * mm, "end": v(-496.73, 530.12) * mm});
            skLineSegment(sketch, "E1064", {"start": v(-496.73, 530.12) * mm, "end": v(-496.35, 530.42) * mm});
            skLineSegment(sketch, "E1065", {"start": v(-496.35, 530.42) * mm, "end": v(-495.97, 530.7) * mm});
            skLineSegment(sketch, "E1066", {"start": v(-495.97, 530.7) * mm, "end": v(-495.58, 530.98) * mm});
            skLineSegment(sketch, "E1067", {"start": v(-495.58, 530.98) * mm, "end": v(-495.18, 531.24) * mm});
            skLineSegment(sketch, "E1068", {"start": v(-495.18, 531.24) * mm, "end": v(-494.77, 531.5) * mm});
            skLineSegment(sketch, "E1069", {"start": v(-494.77, 531.5) * mm, "end": v(-494.36, 531.74) * mm});
            skLineSegment(sketch, "E1070", {"start": v(-494.36, 531.74) * mm, "end": v(-493.94, 531.97) * mm});
            skLineSegment(sketch, "E1071", {"start": v(-493.94, 531.97) * mm, "end": v(-493.52, 532.2) * mm});
            skLineSegment(sketch, "E1072", {"start": v(-493.52, 532.2) * mm, "end": v(-493.1, 532.4) * mm});
            skLineSegment(sketch, "E1073", {"start": v(-493.1, 532.4) * mm, "end": v(-492.66, 532.6) * mm});
            skLineSegment(sketch, "E1074", {"start": v(-492.66, 532.6) * mm, "end": v(-492.23, 532.8) * mm});
            skLineSegment(sketch, "E1075", {"start": v(-492.23, 532.8) * mm, "end": v(-491.79, 532.97) * mm});
            skLineSegment(sketch, "E1076", {"start": v(-491.79, 532.97) * mm, "end": v(-491.34, 533.14) * mm});
            skLineSegment(sketch, "E1077", {"start": v(-491.34, 533.14) * mm, "end": v(-490.9, 533.3) * mm});
            skLineSegment(sketch, "E1078", {"start": v(-490.9, 533.3) * mm, "end": v(-490.44, 533.45) * mm});
            skLineSegment(sketch, "E1079", {"start": v(-490.44, 533.45) * mm, "end": v(-489.98, 533.58) * mm});
            skLineSegment(sketch, "E1080", {"start": v(-489.98, 533.58) * mm, "end": v(-489.52, 533.7) * mm});
            skLineSegment(sketch, "E1081", {"start": v(-489.52, 533.7) * mm, "end": v(-489.06, 533.82) * mm});
            skLineSegment(sketch, "E1082", {"start": v(-489.06, 533.82) * mm, "end": v(-488.6, 533.92) * mm});
            skLineSegment(sketch, "E1083", {"start": v(-488.6, 533.92) * mm, "end": v(-488.13, 534) * mm});
            skLineSegment(sketch, "E1084", {"start": v(-488.13, 534) * mm, "end": v(-487.65, 534.09) * mm});
            skLineSegment(sketch, "E1085", {"start": v(-487.65, 534.09) * mm, "end": v(-487.18, 534.15) * mm});
            skLineSegment(sketch, "E1086", {"start": v(-487.18, 534.15) * mm, "end": v(-486.7, 534.2) * mm});
            skLineSegment(sketch, "E1087", {"start": v(-486.7, 534.2) * mm, "end": v(-486.23, 534.25) * mm});
            skLineSegment(sketch, "E1088", {"start": v(-486.23, 534.25) * mm, "end": v(-485.75, 534.28) * mm});
            skLineSegment(sketch, "E1089", {"start": v(-485.75, 534.28) * mm, "end": v(-485.27, 534.3) * mm});
            skLineSegment(sketch, "E1090", {"start": v(-485.27, 534.3) * mm, "end": v(-484.79, 534.3) * mm});
            skLineSegment(sketch, "E1091", {"start": v(-484.79, 534.3) * mm, "end": v(-484.3, 534.3) * mm});
            skLineSegment(sketch, "E1092", {"start": v(-484.3, 534.3) * mm, "end": v(-483.82, 534.29) * mm});
            skLineSegment(sketch, "E1093", {"start": v(-483.82, 534.29) * mm, "end": v(-483.37, 534.3) * mm});
            skLineSegment(sketch, "E1094", {"start": v(-483.37, 534.3) * mm, "end": v(-482.92, 534.29) * mm});
            skLineSegment(sketch, "E1095", {"start": v(-482.92, 534.29) * mm, "end": v(-482.48, 534.27) * mm});
            skLineSegment(sketch, "E1096", {"start": v(-482.48, 534.27) * mm, "end": v(-482.03, 534.25) * mm});
            skLineSegment(sketch, "E1097", {"start": v(-482.03, 534.25) * mm, "end": v(-481.58, 534.2) * mm});
            skLineSegment(sketch, "E1098", {"start": v(-481.58, 534.2) * mm, "end": v(-481.14, 534.16) * mm});
            skLineSegment(sketch, "E1099", {"start": v(-481.14, 534.16) * mm, "end": v(-480.7, 534.1) * mm});
            skLineSegment(sketch, "E1100", {"start": v(-480.7, 534.1) * mm, "end": v(-480.26, 534.03) * mm});
            skLineSegment(sketch, "E1101", {"start": v(-480.26, 534.03) * mm, "end": v(-479.82, 533.95) * mm});
            skLineSegment(sketch, "E1102", {"start": v(-479.82, 533.95) * mm, "end": v(-479.38, 533.85) * mm});
            skLineSegment(sketch, "E1103", {"start": v(-479.38, 533.85) * mm, "end": v(-478.95, 533.75) * mm});
            skLineSegment(sketch, "E1104", {"start": v(-478.95, 533.75) * mm, "end": v(-478.52, 533.64) * mm});
            skLineSegment(sketch, "E1105", {"start": v(-478.52, 533.64) * mm, "end": v(-478.1, 533.51) * mm});
            skLineSegment(sketch, "E1106", {"start": v(-478.1, 533.51) * mm, "end": v(-477.67, 533.38) * mm});
            skLineSegment(sketch, "E1107", {"start": v(-477.67, 533.38) * mm, "end": v(-477.25, 533.23) * mm});
            skLineSegment(sketch, "E1108", {"start": v(-477.25, 533.23) * mm, "end": v(-476.84, 533.08) * mm});
            skLineSegment(sketch, "E1109", {"start": v(-476.84, 533.08) * mm, "end": v(-476.43, 532.9) * mm});
            skLineSegment(sketch, "E1110", {"start": v(-476.43, 532.9) * mm, "end": v(-476.02, 532.73) * mm});
            skLineSegment(sketch, "E1111", {"start": v(-476.02, 532.73) * mm, "end": v(-475.62, 532.55) * mm});
            skLineSegment(sketch, "E1112", {"start": v(-475.62, 532.55) * mm, "end": v(-475.22, 532.35) * mm});
            skLineSegment(sketch, "E1113", {"start": v(-475.22, 532.35) * mm, "end": v(-474.82, 532.14) * mm});
            skLineSegment(sketch, "E1114", {"start": v(-474.82, 532.14) * mm, "end": v(-474.44, 531.93) * mm});
            skLineSegment(sketch, "E1115", {"start": v(-474.44, 531.93) * mm, "end": v(-474.05, 531.7) * mm});
            skLineSegment(sketch, "E1116", {"start": v(-474.05, 531.7) * mm, "end": v(-473.67, 531.47) * mm});
            skLineSegment(sketch, "E1117", {"start": v(-473.67, 531.47) * mm, "end": v(-473.3, 531.22) * mm});
            skLineSegment(sketch, "E1118", {"start": v(-473.3, 531.22) * mm, "end": v(-472.94, 530.97) * mm});
            skLineSegment(sketch, "E1119", {"start": v(-472.94, 530.97) * mm, "end": v(-472.58, 530.7) * mm});
            skLineSegment(sketch, "E1120", {"start": v(-472.58, 530.7) * mm, "end": v(-472.22, 530.43) * mm});
            skLineSegment(sketch, "E1121", {"start": v(-472.22, 530.43) * mm, "end": v(-471.87, 530.15) * mm});
            skLineSegment(sketch, "E1122", {"start": v(-471.87, 530.15) * mm, "end": v(-471.53, 529.85) * mm});
            skLineSegment(sketch, "E1123", {"start": v(-471.53, 529.85) * mm, "end": v(-471.2, 529.55) * mm});
            skLineSegment(sketch, "E1124", {"start": v(-471.2, 529.55) * mm, "end": v(-470.87, 529.24) * mm});
            skLineSegment(sketch, "E1125", {"start": v(-470.87, 529.24) * mm, "end": v(-470.62, 528.99) * mm});
            skLineSegment(sketch, "E1126", {"start": v(-470.62, 528.99) * mm, "end": v(-470.37, 528.72) * mm});
            skLineSegment(sketch, "E1127", {"start": v(-470.37, 528.72) * mm, "end": v(-470.13, 528.45) * mm});
            skLineSegment(sketch, "E1128", {"start": v(-470.13, 528.45) * mm, "end": v(-469.9, 528.18) * mm});
            skLineSegment(sketch, "E1129", {"start": v(-469.9, 528.18) * mm, "end": v(-469.67, 527.9) * mm});
            skLineSegment(sketch, "E1130", {"start": v(-469.67, 527.9) * mm, "end": v(-469.45, 527.62) * mm});
            skLineSegment(sketch, "E1131", {"start": v(-469.45, 527.62) * mm, "end": v(-469.24, 527.33) * mm});
            skLineSegment(sketch, "E1132", {"start": v(-469.24, 527.33) * mm, "end": v(-469.04, 527.03) * mm});
            skLineSegment(sketch, "E1133", {"start": v(-469.04, 527.03) * mm, "end": v(-468.84, 526.73) * mm});
            skLineSegment(sketch, "E1134", {"start": v(-468.84, 526.73) * mm, "end": v(-468.65, 526.43) * mm});
            skLineSegment(sketch, "E1135", {"start": v(-468.65, 526.43) * mm, "end": v(-468.47, 526.12) * mm});
            skLineSegment(sketch, "E1136", {"start": v(-468.47, 526.12) * mm, "end": v(-468.3, 525.8) * mm});
            skLineSegment(sketch, "E1137", {"start": v(-468.3, 525.8) * mm, "end": v(-468.13, 525.5) * mm});
            skLineSegment(sketch, "E1138", {"start": v(-468.13, 525.5) * mm, "end": v(-467.98, 525.17) * mm});
            skLineSegment(sketch, "E1139", {"start": v(-467.98, 525.17) * mm, "end": v(-467.83, 524.85) * mm});
            skLineSegment(sketch, "E1140", {"start": v(-467.83, 524.85) * mm, "end": v(-467.69, 524.52) * mm});
            skLineSegment(sketch, "E1141", {"start": v(-467.69, 524.52) * mm, "end": v(-467.55, 524.19) * mm});
            skLineSegment(sketch, "E1142", {"start": v(-467.55, 524.19) * mm, "end": v(-467.43, 523.85) * mm});
            skLineSegment(sketch, "E1143", {"start": v(-467.43, 523.85) * mm, "end": v(-467.31, 523.52) * mm});
            skLineSegment(sketch, "E1144", {"start": v(-467.31, 523.52) * mm, "end": v(-467.2, 523.18) * mm});
            skLineSegment(sketch, "E1145", {"start": v(-467.2, 523.18) * mm, "end": v(-467.1, 522.83) * mm});
            skLineSegment(sketch, "E1146", {"start": v(-467.1, 522.83) * mm, "end": v(-467.01, 522.49) * mm});
            skLineSegment(sketch, "E1147", {"start": v(-467.01, 522.49) * mm, "end": v(-466.93, 522.14) * mm});
            skLineSegment(sketch, "E1148", {"start": v(-466.93, 522.14) * mm, "end": v(-466.86, 521.79) * mm});
            skLineSegment(sketch, "E1149", {"start": v(-466.86, 521.79) * mm, "end": v(-466.8, 521.44) * mm});
            skLineSegment(sketch, "E1150", {"start": v(-466.8, 521.44) * mm, "end": v(-466.74, 521.08) * mm});
            skLineSegment(sketch, "E1151", {"start": v(-466.74, 521.08) * mm, "end": v(-466.69, 520.73) * mm});
            skLineSegment(sketch, "E1152", {"start": v(-466.69, 520.73) * mm, "end": v(-466.65, 520.37) * mm});
            skLineSegment(sketch, "E1153", {"start": v(-466.65, 520.37) * mm, "end": v(-466.62, 520.01) * mm});
            skLineSegment(sketch, "E1154", {"start": v(-466.62, 520.01) * mm, "end": v(-466.6, 519.65) * mm});
            skLineSegment(sketch, "E1155", {"start": v(-466.6, 519.65) * mm, "end": v(-466.59, 519.3) * mm});
            skLineSegment(sketch, "E1156", {"start": v(-466.59, 519.3) * mm, "end": v(-466.59, 518.93) * mm});
            skLineSegment(sketch, "E1157", {"start": v(-466.59, 557.64) * mm, "end": v(-466.58, 557.28) * mm});
            skLineSegment(sketch, "E1158", {"start": v(-466.58, 557.28) * mm, "end": v(-466.59, 556.9) * mm});
            skLineSegment(sketch, "E1159", {"start": v(-466.59, 556.9) * mm, "end": v(-466.6, 556.54) * mm});
            skLineSegment(sketch, "E1160", {"start": v(-466.6, 556.54) * mm, "end": v(-466.63, 556.18) * mm});
            skLineSegment(sketch, "E1161", {"start": v(-466.63, 556.18) * mm, "end": v(-466.66, 555.82) * mm});
            skLineSegment(sketch, "E1162", {"start": v(-466.66, 555.82) * mm, "end": v(-466.7, 555.45) * mm});
            skLineSegment(sketch, "E1163", {"start": v(-466.7, 555.45) * mm, "end": v(-466.76, 555.1) * mm});
            skLineSegment(sketch, "E1164", {"start": v(-466.76, 555.1) * mm, "end": v(-466.82, 554.74) * mm});
            skLineSegment(sketch, "E1165", {"start": v(-466.82, 554.74) * mm, "end": v(-466.89, 554.38) * mm});
            skLineSegment(sketch, "E1166", {"start": v(-466.89, 554.38) * mm, "end": v(-466.97, 554.02) * mm});
            skLineSegment(sketch, "E1167", {"start": v(-466.97, 554.02) * mm, "end": v(-467.05, 553.67) * mm});
            skLineSegment(sketch, "E1168", {"start": v(-467.05, 553.67) * mm, "end": v(-467.15, 553.32) * mm});
            skLineSegment(sketch, "E1169", {"start": v(-467.15, 553.32) * mm, "end": v(-467.25, 552.98) * mm});
            skLineSegment(sketch, "E1170", {"start": v(-467.25, 552.98) * mm, "end": v(-467.37, 552.63) * mm});
            skLineSegment(sketch, "E1171", {"start": v(-467.37, 552.63) * mm, "end": v(-467.49, 552.3) * mm});
            skLineSegment(sketch, "E1172", {"start": v(-467.49, 552.3) * mm, "end": v(-467.62, 551.95) * mm});
            skLineSegment(sketch, "E1173", {"start": v(-467.62, 551.95) * mm, "end": v(-467.76, 551.62) * mm});
            skLineSegment(sketch, "E1174", {"start": v(-467.76, 551.62) * mm, "end": v(-467.9, 551.29) * mm});
            skLineSegment(sketch, "E1175", {"start": v(-467.9, 551.29) * mm, "end": v(-468.06, 550.96) * mm});
            skLineSegment(sketch, "E1176", {"start": v(-468.06, 550.96) * mm, "end": v(-468.22, 550.64) * mm});
            skLineSegment(sketch, "E1177", {"start": v(-468.22, 550.64) * mm, "end": v(-468.4, 550.32) * mm});
            skLineSegment(sketch, "E1178", {"start": v(-468.4, 550.32) * mm, "end": v(-468.57, 550) * mm});
            skLineSegment(sketch, "E1179", {"start": v(-468.57, 550) * mm, "end": v(-468.76, 549.7) * mm});
            skLineSegment(sketch, "E1180", {"start": v(-468.76, 549.7) * mm, "end": v(-468.95, 549.38) * mm});
            skLineSegment(sketch, "E1181", {"start": v(-468.95, 549.38) * mm, "end": v(-469.15, 549.08) * mm});
            skLineSegment(sketch, "E1182", {"start": v(-469.15, 549.08) * mm, "end": v(-469.36, 548.78) * mm});
            skLineSegment(sketch, "E1183", {"start": v(-469.36, 548.78) * mm, "end": v(-469.58, 548.5) * mm});
            skLineSegment(sketch, "E1184", {"start": v(-469.58, 548.5) * mm, "end": v(-469.8, 548.2) * mm});
            skLineSegment(sketch, "E1185", {"start": v(-469.8, 548.2) * mm, "end": v(-470.04, 547.92) * mm});
            skLineSegment(sketch, "E1186", {"start": v(-470.04, 547.92) * mm, "end": v(-470.28, 547.65) * mm});
            skLineSegment(sketch, "E1187", {"start": v(-470.28, 547.65) * mm, "end": v(-470.53, 547.38) * mm});
            skLineSegment(sketch, "E1188", {"start": v(-470.53, 547.38) * mm, "end": v(-470.78, 547.11) * mm});
            skLineSegment(sketch, "E1189", {"start": v(-470.78, 547.11) * mm, "end": v(-471.11, 546.8) * mm});
            skLineSegment(sketch, "E1190", {"start": v(-471.11, 546.8) * mm, "end": v(-471.45, 546.5) * mm});
            skLineSegment(sketch, "E1191", {"start": v(-471.45, 546.5) * mm, "end": v(-471.8, 546.22) * mm});
            skLineSegment(sketch, "E1192", {"start": v(-471.8, 546.22) * mm, "end": v(-472.15, 545.94) * mm});
            skLineSegment(sketch, "E1193", {"start": v(-472.15, 545.94) * mm, "end": v(-472.51, 545.67) * mm});
            skLineSegment(sketch, "E1194", {"start": v(-472.51, 545.67) * mm, "end": v(-472.88, 545.41) * mm});
            skLineSegment(sketch, "E1195", {"start": v(-472.88, 545.41) * mm, "end": v(-473.25, 545.16) * mm});
            skLineSegment(sketch, "E1196", {"start": v(-473.25, 545.16) * mm, "end": v(-473.63, 544.92) * mm});
            skLineSegment(sketch, "E1197", {"start": v(-473.63, 544.92) * mm, "end": v(-474, 544.69) * mm});
            skLineSegment(sketch, "E1198", {"start": v(-474, 544.69) * mm, "end": v(-474.4, 544.47) * mm});
            skLineSegment(sketch, "E1199", {"start": v(-474.4, 544.47) * mm, "end": v(-474.79, 544.26) * mm});
            skLineSegment(sketch, "E1200", {"start": v(-474.79, 544.26) * mm, "end": v(-475.19, 544.05) * mm});
            skLineSegment(sketch, "E1201", {"start": v(-475.19, 544.05) * mm, "end": v(-475.59, 543.86) * mm});
            skLineSegment(sketch, "E1202", {"start": v(-475.59, 543.86) * mm, "end": v(-476, 543.68) * mm});
            skLineSegment(sketch, "E1203", {"start": v(-476, 543.68) * mm, "end": v(-476.4, 543.5) * mm});
            skLineSegment(sketch, "E1204", {"start": v(-476.4, 543.5) * mm, "end": v(-476.82, 543.34) * mm});
            skLineSegment(sketch, "E1205", {"start": v(-476.82, 543.34) * mm, "end": v(-477.24, 543.2) * mm});
            skLineSegment(sketch, "E1206", {"start": v(-477.24, 543.2) * mm, "end": v(-477.66, 543.05) * mm});
            skLineSegment(sketch, "E1207", {"start": v(-477.66, 543.05) * mm, "end": v(-478.09, 542.92) * mm});
            skLineSegment(sketch, "E1208", {"start": v(-478.09, 542.92) * mm, "end": v(-478.52, 542.8) * mm});
            skLineSegment(sketch, "E1209", {"start": v(-478.52, 542.8) * mm, "end": v(-478.95, 542.69) * mm});
            skLineSegment(sketch, "E1210", {"start": v(-478.95, 542.69) * mm, "end": v(-479.38, 542.59) * mm});
            skLineSegment(sketch, "E1211", {"start": v(-479.38, 542.59) * mm, "end": v(-479.82, 542.5) * mm});
            skLineSegment(sketch, "E1212", {"start": v(-479.82, 542.5) * mm, "end": v(-480.26, 542.42) * mm});
            skLineSegment(sketch, "E1213", {"start": v(-480.26, 542.42) * mm, "end": v(-480.7, 542.35) * mm});
            skLineSegment(sketch, "E1214", {"start": v(-480.7, 542.35) * mm, "end": v(-481.15, 542.3) * mm});
            skLineSegment(sketch, "E1215", {"start": v(-481.15, 542.3) * mm, "end": v(-481.6, 542.25) * mm});
            skLineSegment(sketch, "E1216", {"start": v(-481.6, 542.25) * mm, "end": v(-482.04, 542.22) * mm});
            skLineSegment(sketch, "E1217", {"start": v(-482.04, 542.22) * mm, "end": v(-482.5, 542.2) * mm});
            skLineSegment(sketch, "E1218", {"start": v(-482.5, 542.2) * mm, "end": v(-482.94, 542.18) * mm});
            skLineSegment(sketch, "E1219", {"start": v(-482.94, 542.18) * mm, "end": v(-483.4, 542.18) * mm});
            skLineSegment(sketch, "E1220", {"start": v(-483.4, 542.18) * mm, "end": v(-483.85, 542.19) * mm});
            skLineSegment(sketch, "E1221", {"start": v(-483.85, 542.19) * mm, "end": v(-484.34, 542.18) * mm});
            skLineSegment(sketch, "E1222", {"start": v(-484.34, 542.18) * mm, "end": v(-484.83, 542.17) * mm});
            skLineSegment(sketch, "E1223", {"start": v(-484.83, 542.17) * mm, "end": v(-485.32, 542.18) * mm});
            skLineSegment(sketch, "E1224", {"start": v(-485.32, 542.18) * mm, "end": v(-485.8, 542.2) * mm});
            skLineSegment(sketch, "E1225", {"start": v(-485.8, 542.2) * mm, "end": v(-486.29, 542.24) * mm});
            skLineSegment(sketch, "E1226", {"start": v(-486.29, 542.24) * mm, "end": v(-486.77, 542.3) * mm});
            skLineSegment(sketch, "E1227", {"start": v(-486.77, 542.3) * mm, "end": v(-487.26, 542.35) * mm});
            skLineSegment(sketch, "E1228", {"start": v(-487.26, 542.35) * mm, "end": v(-487.74, 542.42) * mm});
            skLineSegment(sketch, "E1229", {"start": v(-487.74, 542.42) * mm, "end": v(-488.22, 542.5) * mm});
            skLineSegment(sketch, "E1230", {"start": v(-488.22, 542.5) * mm, "end": v(-488.7, 542.6) * mm});
            skLineSegment(sketch, "E1231", {"start": v(-488.7, 542.6) * mm, "end": v(-489.16, 542.7) * mm});
            skLineSegment(sketch, "E1232", {"start": v(-489.16, 542.7) * mm, "end": v(-489.63, 542.83) * mm});
            skLineSegment(sketch, "E1233", {"start": v(-489.63, 542.83) * mm, "end": v(-490.1, 542.96) * mm});
            skLineSegment(sketch, "E1234", {"start": v(-490.1, 542.96) * mm, "end": v(-490.56, 543.1) * mm});
            skLineSegment(sketch, "E1235", {"start": v(-490.56, 543.1) * mm, "end": v(-491.02, 543.25) * mm});
            skLineSegment(sketch, "E1236", {"start": v(-491.02, 543.25) * mm, "end": v(-491.48, 543.42) * mm});
            skLineSegment(sketch, "E1237", {"start": v(-491.48, 543.42) * mm, "end": v(-491.93, 543.6) * mm});
            skLineSegment(sketch, "E1238", {"start": v(-491.93, 543.6) * mm, "end": v(-492.37, 543.78) * mm});
            skLineSegment(sketch, "E1239", {"start": v(-492.37, 543.78) * mm, "end": v(-492.81, 543.98) * mm});
            skLineSegment(sketch, "E1240", {"start": v(-492.81, 543.98) * mm, "end": v(-493.25, 544.19) * mm});
            skLineSegment(sketch, "E1241", {"start": v(-493.25, 544.19) * mm, "end": v(-493.68, 544.4) * mm});
            skLineSegment(sketch, "E1242", {"start": v(-493.68, 544.4) * mm, "end": v(-494.1, 544.64) * mm});
            skLineSegment(sketch, "E1243", {"start": v(-494.1, 544.64) * mm, "end": v(-494.53, 544.88) * mm});
            skLineSegment(sketch, "E1244", {"start": v(-494.53, 544.88) * mm, "end": v(-494.94, 545.13) * mm});
            skLineSegment(sketch, "E1245", {"start": v(-494.94, 545.13) * mm, "end": v(-495.35, 545.4) * mm});
            skLineSegment(sketch, "E1246", {"start": v(-495.35, 545.4) * mm, "end": v(-495.76, 545.67) * mm});
            skLineSegment(sketch, "E1247", {"start": v(-495.76, 545.67) * mm, "end": v(-496.15, 545.95) * mm});
            skLineSegment(sketch, "E1248", {"start": v(-496.15, 545.95) * mm, "end": v(-496.54, 546.24) * mm});
            skLineSegment(sketch, "E1249", {"start": v(-496.54, 546.24) * mm, "end": v(-496.92, 546.55) * mm});
            skLineSegment(sketch, "E1250", {"start": v(-496.92, 546.55) * mm, "end": v(-497.3, 546.86) * mm});
            skLineSegment(sketch, "E1251", {"start": v(-497.3, 546.86) * mm, "end": v(-497.67, 547.18) * mm});
            skLineSegment(sketch, "E1252", {"start": v(-497.67, 547.18) * mm, "end": v(-498.03, 547.52) * mm});
            skLineSegment(sketch, "E1253", {"start": v(-498.03, 547.52) * mm, "end": v(-498.28, 547.77) * mm});
            skLineSegment(sketch, "E1254", {"start": v(-498.28, 547.77) * mm, "end": v(-498.53, 548.02) * mm});
            skLineSegment(sketch, "E1255", {"start": v(-498.53, 548.02) * mm, "end": v(-498.77, 548.29) * mm});
            skLineSegment(sketch, "E1256", {"start": v(-498.77, 548.29) * mm, "end": v(-499, 548.55) * mm});
            skLineSegment(sketch, "E1257", {"start": v(-499, 548.55) * mm, "end": v(-499.23, 548.83) * mm});
            skLineSegment(sketch, "E1258", {"start": v(-499.23, 548.83) * mm, "end": v(-499.44, 549.1) * mm});
            skLineSegment(sketch, "E1259", {"start": v(-499.44, 549.1) * mm, "end": v(-499.65, 549.39) * mm});
            skLineSegment(sketch, "E1260", {"start": v(-499.65, 549.39) * mm, "end": v(-499.86, 549.68) * mm});
            skLineSegment(sketch, "E1261", {"start": v(-499.86, 549.68) * mm, "end": v(-500.05, 549.97) * mm});
            skLineSegment(sketch, "E1262", {"start": v(-500.05, 549.97) * mm, "end": v(-500.24, 550.27) * mm});
            skLineSegment(sketch, "E1263", {"start": v(-500.24, 550.27) * mm, "end": v(-500.42, 550.57) * mm});
            skLineSegment(sketch, "E1264", {"start": v(-500.42, 550.57) * mm, "end": v(-500.59, 550.88) * mm});
            skLineSegment(sketch, "E1265", {"start": v(-500.59, 550.88) * mm, "end": v(-500.75, 551.19) * mm});
            skLineSegment(sketch, "E1266", {"start": v(-500.75, 551.19) * mm, "end": v(-500.9, 551.5) * mm});
            skLineSegment(sketch, "E1267", {"start": v(-500.9, 551.5) * mm, "end": v(-501.06, 551.82) * mm});
            skLineSegment(sketch, "E1268", {"start": v(-501.06, 551.82) * mm, "end": v(-501.2, 552.14) * mm});
            skLineSegment(sketch, "E1269", {"start": v(-501.2, 552.14) * mm, "end": v(-501.33, 552.47) * mm});
            skLineSegment(sketch, "E1270", {"start": v(-501.33, 552.47) * mm, "end": v(-501.45, 552.8) * mm});
            skLineSegment(sketch, "E1271", {"start": v(-501.45, 552.8) * mm, "end": v(-501.56, 553.13) * mm});
            skLineSegment(sketch, "E1272", {"start": v(-501.56, 553.13) * mm, "end": v(-501.67, 553.47) * mm});
            skLineSegment(sketch, "E1273", {"start": v(-501.67, 553.47) * mm, "end": v(-501.77, 553.8) * mm});
            skLineSegment(sketch, "E1274", {"start": v(-501.77, 553.8) * mm, "end": v(-501.85, 554.14) * mm});
            skLineSegment(sketch, "E1275", {"start": v(-501.85, 554.14) * mm, "end": v(-501.93, 554.49) * mm});
            skLineSegment(sketch, "E1276", {"start": v(-501.93, 554.49) * mm, "end": v(-502, 554.83) * mm});
            skLineSegment(sketch, "E1277", {"start": v(-502, 554.83) * mm, "end": v(-502.07, 555.18) * mm});
            skLineSegment(sketch, "E1278", {"start": v(-502.07, 555.18) * mm, "end": v(-502.12, 555.53) * mm});
            skLineSegment(sketch, "E1279", {"start": v(-502.12, 555.53) * mm, "end": v(-502.17, 555.88) * mm});
            skLineSegment(sketch, "E1280", {"start": v(-502.17, 555.88) * mm, "end": v(-502.2, 556.23) * mm});
            skLineSegment(sketch, "E1281", {"start": v(-502.2, 556.23) * mm, "end": v(-502.23, 556.58) * mm});
            skLineSegment(sketch, "E1282", {"start": v(-502.23, 556.58) * mm, "end": v(-502.24, 556.94) * mm});
            skLineSegment(sketch, "E1283", {"start": v(-502.24, 556.94) * mm, "end": v(-502.25, 557.3) * mm});
            skLineSegment(sketch, "E1284", {"start": v(-502.25, 557.3) * mm, "end": v(-502.25, 557.65) * mm});
            skLineSegment(sketch, "E1285", {"start": v(-502.25, 557.65) * mm, "end": v(-502.25, 558.01) * mm});
            skLineSegment(sketch, "E1286", {"start": v(-502.25, 558.01) * mm, "end": v(-502.23, 558.37) * mm});
            skLineSegment(sketch, "E1287", {"start": v(-502.23, 558.37) * mm, "end": v(-502.21, 558.73) * mm});
            skLineSegment(sketch, "E1288", {"start": v(-502.21, 558.73) * mm, "end": v(-502.18, 559.1) * mm});
            skLineSegment(sketch, "E1289", {"start": v(-502.18, 559.1) * mm, "end": v(-502.14, 559.45) * mm});
            skLineSegment(sketch, "E1290", {"start": v(-502.14, 559.45) * mm, "end": v(-502.1, 559.8) * mm});
            skLineSegment(sketch, "E1291", {"start": v(-502.1, 559.8) * mm, "end": v(-502.03, 560.16) * mm});
            skLineSegment(sketch, "E1292", {"start": v(-502.03, 560.16) * mm, "end": v(-501.96, 560.51) * mm});
            skLineSegment(sketch, "E1293", {"start": v(-501.96, 560.51) * mm, "end": v(-501.89, 560.86) * mm});
            skLineSegment(sketch, "E1294", {"start": v(-501.89, 560.86) * mm, "end": v(-501.8, 561.2) * mm});
            skLineSegment(sketch, "E1295", {"start": v(-501.8, 561.2) * mm, "end": v(-501.7, 561.55) * mm});
            skLineSegment(sketch, "E1296", {"start": v(-501.7, 561.55) * mm, "end": v(-501.6, 561.9) * mm});
            skLineSegment(sketch, "E1297", {"start": v(-501.6, 561.9) * mm, "end": v(-501.5, 562.23) * mm});
            skLineSegment(sketch, "E1298", {"start": v(-501.5, 562.23) * mm, "end": v(-501.37, 562.57) * mm});
            skLineSegment(sketch, "E1299", {"start": v(-501.37, 562.57) * mm, "end": v(-501.24, 562.9) * mm});
            skLineSegment(sketch, "E1300", {"start": v(-501.24, 562.9) * mm, "end": v(-501.1, 563.23) * mm});
            skLineSegment(sketch, "E1301", {"start": v(-501.1, 563.23) * mm, "end": v(-500.96, 563.56) * mm});
            skLineSegment(sketch, "E1302", {"start": v(-500.96, 563.56) * mm, "end": v(-500.8, 563.88) * mm});
            skLineSegment(sketch, "E1303", {"start": v(-500.8, 563.88) * mm, "end": v(-500.65, 564.2) * mm});
            skLineSegment(sketch, "E1304", {"start": v(-500.65, 564.2) * mm, "end": v(-500.48, 564.51) * mm});
            skLineSegment(sketch, "E1305", {"start": v(-500.48, 564.51) * mm, "end": v(-500.3, 564.82) * mm});
            skLineSegment(sketch, "E1306", {"start": v(-500.3, 564.82) * mm, "end": v(-500.11, 565.13) * mm});
            skLineSegment(sketch, "E1307", {"start": v(-500.11, 565.13) * mm, "end": v(-499.92, 565.43) * mm});
            skLineSegment(sketch, "E1308", {"start": v(-499.92, 565.43) * mm, "end": v(-499.72, 565.72) * mm});
            skLineSegment(sketch, "E1309", {"start": v(-499.72, 565.72) * mm, "end": v(-499.5, 566.01) * mm});
            skLineSegment(sketch, "E1310", {"start": v(-499.5, 566.01) * mm, "end": v(-499.3, 566.3) * mm});
            skLineSegment(sketch, "E1311", {"start": v(-499.3, 566.3) * mm, "end": v(-499.07, 566.58) * mm});
            skLineSegment(sketch, "E1312", {"start": v(-499.07, 566.58) * mm, "end": v(-498.83, 566.86) * mm});
            skLineSegment(sketch, "E1313", {"start": v(-498.83, 566.86) * mm, "end": v(-498.6, 567.12) * mm});
            skLineSegment(sketch, "E1314", {"start": v(-498.6, 567.12) * mm, "end": v(-498.35, 567.39) * mm});
            skLineSegment(sketch, "E1315", {"start": v(-498.35, 567.39) * mm, "end": v(-498.1, 567.64) * mm});
            skLineSegment(sketch, "E1316", {"start": v(-498.1, 567.64) * mm, "end": v(-497.83, 567.9) * mm});
            skLineSegment(sketch, "E1317", {"start": v(-497.83, 567.9) * mm, "end": v(-497.47, 568.22) * mm});
            skLineSegment(sketch, "E1318", {"start": v(-497.47, 568.22) * mm, "end": v(-497.1, 568.53) * mm});
            skLineSegment(sketch, "E1319", {"start": v(-497.1, 568.53) * mm, "end": v(-496.73, 568.84) * mm});
            skLineSegment(sketch, "E1320", {"start": v(-496.73, 568.84) * mm, "end": v(-496.35, 569.13) * mm});
            skLineSegment(sketch, "E1321", {"start": v(-496.35, 569.13) * mm, "end": v(-495.97, 569.42) * mm});
            skLineSegment(sketch, "E1322", {"start": v(-495.97, 569.42) * mm, "end": v(-495.58, 569.7) * mm});
            skLineSegment(sketch, "E1323", {"start": v(-495.58, 569.7) * mm, "end": v(-495.18, 569.95) * mm});
            skLineSegment(sketch, "E1324", {"start": v(-495.18, 569.95) * mm, "end": v(-494.77, 570.2) * mm});
            skLineSegment(sketch, "E1325", {"start": v(-494.77, 570.2) * mm, "end": v(-494.36, 570.45) * mm});
            skLineSegment(sketch, "E1326", {"start": v(-494.36, 570.45) * mm, "end": v(-493.94, 570.68) * mm});
            skLineSegment(sketch, "E1327", {"start": v(-493.94, 570.68) * mm, "end": v(-493.52, 570.9) * mm});
            skLineSegment(sketch, "E1328", {"start": v(-493.52, 570.9) * mm, "end": v(-493.1, 571.12) * mm});
            skLineSegment(sketch, "E1329", {"start": v(-493.1, 571.12) * mm, "end": v(-492.66, 571.32) * mm});
            skLineSegment(sketch, "E1330", {"start": v(-492.66, 571.32) * mm, "end": v(-492.23, 571.5) * mm});
            skLineSegment(sketch, "E1331", {"start": v(-492.23, 571.5) * mm, "end": v(-491.79, 571.69) * mm});
            skLineSegment(sketch, "E1332", {"start": v(-491.79, 571.69) * mm, "end": v(-491.34, 571.86) * mm});
            skLineSegment(sketch, "E1333", {"start": v(-491.34, 571.86) * mm, "end": v(-490.9, 572.01) * mm});
            skLineSegment(sketch, "E1334", {"start": v(-490.9, 572.01) * mm, "end": v(-490.44, 572.16) * mm});
            skLineSegment(sketch, "E1335", {"start": v(-490.44, 572.16) * mm, "end": v(-489.98, 572.3) * mm});
            skLineSegment(sketch, "E1336", {"start": v(-489.98, 572.3) * mm, "end": v(-489.52, 572.42) * mm});
            skLineSegment(sketch, "E1337", {"start": v(-489.52, 572.42) * mm, "end": v(-489.06, 572.53) * mm});
            skLineSegment(sketch, "E1338", {"start": v(-489.06, 572.53) * mm, "end": v(-488.6, 572.63) * mm});
            skLineSegment(sketch, "E1339", {"start": v(-488.6, 572.63) * mm, "end": v(-488.13, 572.72) * mm});
            skLineSegment(sketch, "E1340", {"start": v(-488.13, 572.72) * mm, "end": v(-487.65, 572.8) * mm});
            skLineSegment(sketch, "E1341", {"start": v(-487.65, 572.8) * mm, "end": v(-487.18, 572.87) * mm});
            skLineSegment(sketch, "E1342", {"start": v(-487.18, 572.87) * mm, "end": v(-486.7, 572.92) * mm});
            skLineSegment(sketch, "E1343", {"start": v(-486.7, 572.92) * mm, "end": v(-486.23, 572.97) * mm});
            skLineSegment(sketch, "E1344", {"start": v(-486.23, 572.97) * mm, "end": v(-485.75, 573) * mm});
            skLineSegment(sketch, "E1345", {"start": v(-485.75, 573) * mm, "end": v(-485.27, 573.02) * mm});
            skLineSegment(sketch, "E1346", {"start": v(-485.27, 573.02) * mm, "end": v(-484.79, 573.02) * mm});
            skLineSegment(sketch, "E1347", {"start": v(-484.79, 573.02) * mm, "end": v(-484.3, 573.02) * mm});
            skLineSegment(sketch, "E1348", {"start": v(-484.3, 573.02) * mm, "end": v(-483.82, 573) * mm});
            skLineSegment(sketch, "E1349", {"start": v(-483.82, 573) * mm, "end": v(-483.37, 573) * mm});
            skLineSegment(sketch, "E1350", {"start": v(-483.37, 573) * mm, "end": v(-482.92, 573) * mm});
            skLineSegment(sketch, "E1351", {"start": v(-482.92, 573) * mm, "end": v(-482.48, 572.99) * mm});
            skLineSegment(sketch, "E1352", {"start": v(-482.48, 572.99) * mm, "end": v(-482.03, 572.96) * mm});
            skLineSegment(sketch, "E1353", {"start": v(-482.03, 572.96) * mm, "end": v(-481.58, 572.92) * mm});
            skLineSegment(sketch, "E1354", {"start": v(-481.58, 572.92) * mm, "end": v(-481.14, 572.88) * mm});
            skLineSegment(sketch, "E1355", {"start": v(-481.14, 572.88) * mm, "end": v(-480.7, 572.81) * mm});
            skLineSegment(sketch, "E1356", {"start": v(-480.7, 572.81) * mm, "end": v(-480.26, 572.74) * mm});
            skLineSegment(sketch, "E1357", {"start": v(-480.26, 572.74) * mm, "end": v(-479.82, 572.66) * mm});
            skLineSegment(sketch, "E1358", {"start": v(-479.82, 572.66) * mm, "end": v(-479.38, 572.57) * mm});
            skLineSegment(sketch, "E1359", {"start": v(-479.38, 572.57) * mm, "end": v(-478.95, 572.47) * mm});
            skLineSegment(sketch, "E1360", {"start": v(-478.95, 572.47) * mm, "end": v(-478.52, 572.35) * mm});
            skLineSegment(sketch, "E1361", {"start": v(-478.52, 572.35) * mm, "end": v(-478.1, 572.23) * mm});
            skLineSegment(sketch, "E1362", {"start": v(-478.1, 572.23) * mm, "end": v(-477.67, 572.1) * mm});
            skLineSegment(sketch, "E1363", {"start": v(-477.67, 572.1) * mm, "end": v(-477.25, 571.95) * mm});
            skLineSegment(sketch, "E1364", {"start": v(-477.25, 571.95) * mm, "end": v(-476.84, 571.8) * mm});
            skLineSegment(sketch, "E1365", {"start": v(-476.84, 571.8) * mm, "end": v(-476.43, 571.62) * mm});
            skLineSegment(sketch, "E1366", {"start": v(-476.43, 571.62) * mm, "end": v(-476.02, 571.45) * mm});
            skLineSegment(sketch, "E1367", {"start": v(-476.02, 571.45) * mm, "end": v(-475.62, 571.26) * mm});
            skLineSegment(sketch, "E1368", {"start": v(-475.62, 571.26) * mm, "end": v(-475.22, 571.07) * mm});
            skLineSegment(sketch, "E1369", {"start": v(-475.22, 571.07) * mm, "end": v(-474.82, 570.86) * mm});
            skLineSegment(sketch, "E1370", {"start": v(-474.82, 570.86) * mm, "end": v(-474.44, 570.64) * mm});
            skLineSegment(sketch, "E1371", {"start": v(-474.44, 570.64) * mm, "end": v(-474.05, 570.42) * mm});
            skLineSegment(sketch, "E1372", {"start": v(-474.05, 570.42) * mm, "end": v(-473.67, 570.18) * mm});
            skLineSegment(sketch, "E1373", {"start": v(-473.67, 570.18) * mm, "end": v(-473.3, 569.94) * mm});
            skLineSegment(sketch, "E1374", {"start": v(-473.3, 569.94) * mm, "end": v(-472.94, 569.68) * mm});
            skLineSegment(sketch, "E1375", {"start": v(-472.94, 569.68) * mm, "end": v(-472.58, 569.42) * mm});
            skLineSegment(sketch, "E1376", {"start": v(-472.58, 569.42) * mm, "end": v(-472.22, 569.14) * mm});
            skLineSegment(sketch, "E1377", {"start": v(-472.22, 569.14) * mm, "end": v(-471.87, 568.86) * mm});
            skLineSegment(sketch, "E1378", {"start": v(-471.87, 568.86) * mm, "end": v(-471.53, 568.57) * mm});
            skLineSegment(sketch, "E1379", {"start": v(-471.53, 568.57) * mm, "end": v(-471.2, 568.27) * mm});
            skLineSegment(sketch, "E1380", {"start": v(-471.2, 568.27) * mm, "end": v(-470.87, 567.96) * mm});
            skLineSegment(sketch, "E1381", {"start": v(-470.87, 567.96) * mm, "end": v(-470.62, 567.7) * mm});
            skLineSegment(sketch, "E1382", {"start": v(-470.62, 567.7) * mm, "end": v(-470.37, 567.44) * mm});
            skLineSegment(sketch, "E1383", {"start": v(-470.37, 567.44) * mm, "end": v(-470.13, 567.17) * mm});
            skLineSegment(sketch, "E1384", {"start": v(-470.13, 567.17) * mm, "end": v(-469.9, 566.9) * mm});
            skLineSegment(sketch, "E1385", {"start": v(-469.9, 566.9) * mm, "end": v(-469.67, 566.62) * mm});
            skLineSegment(sketch, "E1386", {"start": v(-469.67, 566.62) * mm, "end": v(-469.45, 566.33) * mm});
            skLineSegment(sketch, "E1387", {"start": v(-469.45, 566.33) * mm, "end": v(-469.24, 566.04) * mm});
            skLineSegment(sketch, "E1388", {"start": v(-469.24, 566.04) * mm, "end": v(-469.04, 565.75) * mm});
            skLineSegment(sketch, "E1389", {"start": v(-469.04, 565.75) * mm, "end": v(-468.84, 565.45) * mm});
            skLineSegment(sketch, "E1390", {"start": v(-468.84, 565.45) * mm, "end": v(-468.65, 565.14) * mm});
            skLineSegment(sketch, "E1391", {"start": v(-468.65, 565.14) * mm, "end": v(-468.47, 564.84) * mm});
            skLineSegment(sketch, "E1392", {"start": v(-468.47, 564.84) * mm, "end": v(-468.3, 564.52) * mm});
            skLineSegment(sketch, "E1393", {"start": v(-468.3, 564.52) * mm, "end": v(-468.13, 564.2) * mm});
            skLineSegment(sketch, "E1394", {"start": v(-468.13, 564.2) * mm, "end": v(-467.98, 563.89) * mm});
            skLineSegment(sketch, "E1395", {"start": v(-467.98, 563.89) * mm, "end": v(-467.83, 563.56) * mm});
            skLineSegment(sketch, "E1396", {"start": v(-467.83, 563.56) * mm, "end": v(-467.69, 563.23) * mm});
            skLineSegment(sketch, "E1397", {"start": v(-467.69, 563.23) * mm, "end": v(-467.55, 562.9) * mm});
            skLineSegment(sketch, "E1398", {"start": v(-467.55, 562.9) * mm, "end": v(-467.43, 562.57) * mm});
            skLineSegment(sketch, "E1399", {"start": v(-467.43, 562.57) * mm, "end": v(-467.31, 562.23) * mm});
            skLineSegment(sketch, "E1400", {"start": v(-467.31, 562.23) * mm, "end": v(-467.2, 561.9) * mm});
            skLineSegment(sketch, "E1401", {"start": v(-467.2, 561.9) * mm, "end": v(-467.1, 561.55) * mm});
            skLineSegment(sketch, "E1402", {"start": v(-467.1, 561.55) * mm, "end": v(-467.01, 561.2) * mm});
            skLineSegment(sketch, "E1403", {"start": v(-467.01, 561.2) * mm, "end": v(-466.93, 560.85) * mm});
            skLineSegment(sketch, "E1404", {"start": v(-466.93, 560.85) * mm, "end": v(-466.86, 560.5) * mm});
            skLineSegment(sketch, "E1405", {"start": v(-466.86, 560.5) * mm, "end": v(-466.8, 560.15) * mm});
            skLineSegment(sketch, "E1406", {"start": v(-466.8, 560.15) * mm, "end": v(-466.74, 559.8) * mm});
            skLineSegment(sketch, "E1407", {"start": v(-466.74, 559.8) * mm, "end": v(-466.69, 559.44) * mm});
            skLineSegment(sketch, "E1408", {"start": v(-466.69, 559.44) * mm, "end": v(-466.65, 559.08) * mm});
            skLineSegment(sketch, "E1409", {"start": v(-466.65, 559.08) * mm, "end": v(-466.62, 558.73) * mm});
            skLineSegment(sketch, "E1410", {"start": v(-466.62, 558.73) * mm, "end": v(-466.6, 558.37) * mm});
            skLineSegment(sketch, "E1411", {"start": v(-466.6, 558.37) * mm, "end": v(-466.59, 558) * mm});
            skLineSegment(sketch, "E1412", {"start": v(-466.59, 558) * mm, "end": v(-466.59, 557.64) * mm});
            skLineSegment(sketch, "E1413", {"start": v(-467.08, 580.9) * mm, "end": v(-502.04, 580.9) * mm});
            skLineSegment(sketch, "E1414", {"start": v(-502.04, 580.9) * mm, "end": v(-502.04, 596.26) * mm});
            skLineSegment(sketch, "E1415", {"start": v(-502.04, 596.26) * mm, "end": v(-502.04, 596.7) * mm});
            skLineSegment(sketch, "E1416", {"start": v(-502.04, 596.7) * mm, "end": v(-502.01, 597.12) * mm});
            skLineSegment(sketch, "E1417", {"start": v(-502.01, 597.12) * mm, "end": v(-501.96, 597.55) * mm});
            skLineSegment(sketch, "E1418", {"start": v(-501.96, 597.55) * mm, "end": v(-501.9, 597.97) * mm});
            skLineSegment(sketch, "E1419", {"start": v(-501.9, 597.97) * mm, "end": v(-501.8, 598.39) * mm});
            skLineSegment(sketch, "E1420", {"start": v(-501.8, 598.39) * mm, "end": v(-501.7, 598.8) * mm});
            skLineSegment(sketch, "E1421", {"start": v(-501.7, 598.8) * mm, "end": v(-501.56, 599.2) * mm});
            skLineSegment(sketch, "E1422", {"start": v(-501.56, 599.2) * mm, "end": v(-501.4, 599.6) * mm});
            skLineSegment(sketch, "E1423", {"start": v(-501.4, 599.6) * mm, "end": v(-501.24, 600) * mm});
            skLineSegment(sketch, "E1424", {"start": v(-501.24, 600) * mm, "end": v(-501.05, 600.37) * mm});
            skLineSegment(sketch, "E1425", {"start": v(-501.05, 600.37) * mm, "end": v(-500.83, 600.74) * mm});
            skLineSegment(sketch, "E1426", {"start": v(-500.83, 600.74) * mm, "end": v(-500.6, 601.1) * mm});
            skLineSegment(sketch, "E1427", {"start": v(-500.6, 601.1) * mm, "end": v(-500.36, 601.45) * mm});
            skLineSegment(sketch, "E1428", {"start": v(-500.36, 601.45) * mm, "end": v(-500.09, 601.79) * mm});
            skLineSegment(sketch, "E1429", {"start": v(-500.09, 601.79) * mm, "end": v(-499.8, 602.11) * mm});
            skLineSegment(sketch, "E1430", {"start": v(-499.8, 602.11) * mm, "end": v(-499.5, 602.42) * mm});
            skLineSegment(sketch, "E1431", {"start": v(-499.5, 602.42) * mm, "end": v(-499.2, 602.72) * mm});
            skLineSegment(sketch, "E1432", {"start": v(-499.2, 602.72) * mm, "end": v(-498.87, 603) * mm});
            skLineSegment(sketch, "E1433", {"start": v(-498.87, 603) * mm, "end": v(-498.54, 603.26) * mm});
            skLineSegment(sketch, "E1434", {"start": v(-498.54, 603.26) * mm, "end": v(-498.2, 603.51) * mm});
            skLineSegment(sketch, "E1435", {"start": v(-498.2, 603.51) * mm, "end": v(-497.84, 603.74) * mm});
            skLineSegment(sketch, "E1436", {"start": v(-497.84, 603.74) * mm, "end": v(-497.47, 603.95) * mm});
            skLineSegment(sketch, "E1437", {"start": v(-497.47, 603.95) * mm, "end": v(-497.1, 604.14) * mm});
            skLineSegment(sketch, "E1438", {"start": v(-497.1, 604.14) * mm, "end": v(-496.7, 604.31) * mm});
            skLineSegment(sketch, "E1439", {"start": v(-496.7, 604.31) * mm, "end": v(-496.31, 604.47) * mm});
            skLineSegment(sketch, "E1440", {"start": v(-496.31, 604.47) * mm, "end": v(-495.91, 604.6) * mm});
            skLineSegment(sketch, "E1441", {"start": v(-495.91, 604.6) * mm, "end": v(-495.5, 604.71) * mm});
            skLineSegment(sketch, "E1442", {"start": v(-495.5, 604.71) * mm, "end": v(-495.1, 604.8) * mm});
            skLineSegment(sketch, "E1443", {"start": v(-495.1, 604.8) * mm, "end": v(-494.67, 604.88) * mm});
            skLineSegment(sketch, "E1444", {"start": v(-494.67, 604.88) * mm, "end": v(-494.25, 604.93) * mm});
            skLineSegment(sketch, "E1445", {"start": v(-494.25, 604.93) * mm, "end": v(-493.83, 604.96) * mm});
            skLineSegment(sketch, "E1446", {"start": v(-493.83, 604.96) * mm, "end": v(-493.4, 604.97) * mm});
            skLineSegment(sketch, "E1447", {"start": v(-493.4, 604.97) * mm, "end": v(-492.96, 604.98) * mm});
            skLineSegment(sketch, "E1448", {"start": v(-492.96, 604.98) * mm, "end": v(-492.52, 604.96) * mm});
            skLineSegment(sketch, "E1449", {"start": v(-492.52, 604.96) * mm, "end": v(-492.09, 604.91) * mm});
            skLineSegment(sketch, "E1450", {"start": v(-492.09, 604.91) * mm, "end": v(-491.66, 604.85) * mm});
            skLineSegment(sketch, "E1451", {"start": v(-491.66, 604.85) * mm, "end": v(-491.23, 604.77) * mm});
            skLineSegment(sketch, "E1452", {"start": v(-491.23, 604.77) * mm, "end": v(-490.81, 604.66) * mm});
            skLineSegment(sketch, "E1453", {"start": v(-490.81, 604.66) * mm, "end": v(-490.4, 604.53) * mm});
            skLineSegment(sketch, "E1454", {"start": v(-490.4, 604.53) * mm, "end": v(-490, 604.38) * mm});
            skLineSegment(sketch, "E1455", {"start": v(-490, 604.38) * mm, "end": v(-489.6, 604.21) * mm});
            skLineSegment(sketch, "E1456", {"start": v(-489.6, 604.21) * mm, "end": v(-489.2, 604.02) * mm});
            skLineSegment(sketch, "E1457", {"start": v(-489.2, 604.02) * mm, "end": v(-488.83, 603.82) * mm});
            skLineSegment(sketch, "E1458", {"start": v(-488.83, 603.82) * mm, "end": v(-488.46, 603.59) * mm});
            skLineSegment(sketch, "E1459", {"start": v(-488.46, 603.59) * mm, "end": v(-488.1, 603.34) * mm});
            skLineSegment(sketch, "E1460", {"start": v(-488.1, 603.34) * mm, "end": v(-487.75, 603.08) * mm});
            skLineSegment(sketch, "E1461", {"start": v(-487.75, 603.08) * mm, "end": v(-487.42, 602.8) * mm});
            skLineSegment(sketch, "E1462", {"start": v(-487.42, 602.8) * mm, "end": v(-487.1, 602.5) * mm});
            skLineSegment(sketch, "E1463", {"start": v(-487.1, 602.5) * mm, "end": v(-486.8, 602.18) * mm});
            skLineSegment(sketch, "E1464", {"start": v(-486.8, 602.18) * mm, "end": v(-486.52, 601.85) * mm});
            skLineSegment(sketch, "E1465", {"start": v(-486.52, 601.85) * mm, "end": v(-486.25, 601.5) * mm});
            skLineSegment(sketch, "E1466", {"start": v(-486.25, 601.5) * mm, "end": v(-486, 601.15) * mm});
            skLineSegment(sketch, "E1467", {"start": v(-486, 601.15) * mm, "end": v(-485.78, 600.79) * mm});
            skLineSegment(sketch, "E1468", {"start": v(-485.78, 600.79) * mm, "end": v(-485.56, 600.41) * mm});
            skLineSegment(sketch, "E1469", {"start": v(-485.56, 600.41) * mm, "end": v(-485.37, 600.03) * mm});
            skLineSegment(sketch, "E1470", {"start": v(-485.37, 600.03) * mm, "end": v(-485.2, 599.63) * mm});
            skLineSegment(sketch, "E1471", {"start": v(-485.2, 599.63) * mm, "end": v(-485.05, 599.23) * mm});
            skLineSegment(sketch, "E1472", {"start": v(-485.05, 599.23) * mm, "end": v(-484.92, 598.82) * mm});
            skLineSegment(sketch, "E1473", {"start": v(-484.92, 598.82) * mm, "end": v(-484.8, 598.4) * mm});
            skLineSegment(sketch, "E1474", {"start": v(-484.8, 598.4) * mm, "end": v(-484.72, 597.98) * mm});
            skLineSegment(sketch, "E1475", {"start": v(-484.72, 597.98) * mm, "end": v(-484.65, 597.56) * mm});
            skLineSegment(sketch, "E1476", {"start": v(-484.65, 597.56) * mm, "end": v(-484.6, 597.13) * mm});
            skLineSegment(sketch, "E1477", {"start": v(-484.6, 597.13) * mm, "end": v(-484.57, 596.7) * mm});
            skLineSegment(sketch, "E1478", {"start": v(-484.57, 596.7) * mm, "end": v(-484.57, 596.26) * mm});
            skLineSegment(sketch, "E1479", {"start": v(-484.57, 596.26) * mm, "end": v(-484.57, 580.9) * mm});
            skLineSegment(sketch, "E1480", {"start": v(-484.57, 596.26) * mm, "end": v(-484.56, 596.62) * mm});
            skLineSegment(sketch, "E1481", {"start": v(-484.56, 596.62) * mm, "end": v(-484.54, 596.97) * mm});
            skLineSegment(sketch, "E1482", {"start": v(-484.54, 596.97) * mm, "end": v(-484.5, 597.33) * mm});
            skLineSegment(sketch, "E1483", {"start": v(-484.5, 597.33) * mm, "end": v(-484.45, 597.68) * mm});
            skLineSegment(sketch, "E1484", {"start": v(-484.45, 597.68) * mm, "end": v(-484.38, 598.03) * mm});
            skLineSegment(sketch, "E1485", {"start": v(-484.38, 598.03) * mm, "end": v(-484.29, 598.37) * mm});
            skLineSegment(sketch, "E1486", {"start": v(-484.29, 598.37) * mm, "end": v(-484.18, 598.7) * mm});
            skLineSegment(sketch, "E1487", {"start": v(-484.18, 598.7) * mm, "end": v(-484.05, 599.03) * mm});
            skLineSegment(sketch, "E1488", {"start": v(-484.05, 599.03) * mm, "end": v(-483.91, 599.36) * mm});
            skLineSegment(sketch, "E1489", {"start": v(-483.91, 599.36) * mm, "end": v(-483.75, 599.67) * mm});
            skLineSegment(sketch, "E1490", {"start": v(-483.75, 599.67) * mm, "end": v(-483.58, 599.98) * mm});
            skLineSegment(sketch, "E1491", {"start": v(-483.58, 599.98) * mm, "end": v(-483.39, 600.28) * mm});
            skLineSegment(sketch, "E1492", {"start": v(-483.39, 600.28) * mm, "end": v(-483.18, 600.57) * mm});
            skLineSegment(sketch, "E1493", {"start": v(-483.18, 600.57) * mm, "end": v(-482.96, 600.85) * mm});
            skLineSegment(sketch, "E1494", {"start": v(-482.96, 600.85) * mm, "end": v(-482.73, 601.12) * mm});
            skLineSegment(sketch, "E1495", {"start": v(-482.73, 601.12) * mm, "end": v(-482.48, 601.38) * mm});
            skLineSegment(sketch, "E1496", {"start": v(-482.48, 601.38) * mm, "end": v(-482.04, 601.68) * mm});
            skLineSegment(sketch, "E1497", {"start": v(-482.04, 601.68) * mm, "end": v(-481.6, 601.96) * mm});
            skLineSegment(sketch, "E1498", {"start": v(-481.6, 601.96) * mm, "end": v(-481.13, 602.21) * mm});
            skLineSegment(sketch, "E1499", {"start": v(-481.13, 602.21) * mm, "end": v(-480.66, 602.45) * mm});
            skLineSegment(sketch, "E1500", {"start": v(-480.66, 602.45) * mm, "end": v(-480.19, 602.66) * mm});
            skLineSegment(sketch, "E1501", {"start": v(-480.19, 602.66) * mm, "end": v(-479.7, 602.85) * mm});
            skLineSegment(sketch, "E1502", {"start": v(-479.7, 602.85) * mm, "end": v(-479.2, 603.02) * mm});
            skLineSegment(sketch, "E1503", {"start": v(-479.2, 603.02) * mm, "end": v(-478.7, 603.17) * mm});
            skLineSegment(sketch, "E1504", {"start": v(-478.7, 603.17) * mm, "end": v(-478.2, 603.3) * mm});
            skLineSegment(sketch, "E1505", {"start": v(-478.2, 603.3) * mm, "end": v(-477.68, 603.4) * mm});
            skLineSegment(sketch, "E1506", {"start": v(-477.68, 603.4) * mm, "end": v(-477.16, 603.48) * mm});
            skLineSegment(sketch, "E1507", {"start": v(-477.16, 603.48) * mm, "end": v(-476.64, 603.54) * mm});
            skLineSegment(sketch, "E1508", {"start": v(-476.64, 603.54) * mm, "end": v(-476.11, 603.57) * mm});
            skLineSegment(sketch, "E1509", {"start": v(-476.11, 603.57) * mm, "end": v(-475.59, 603.58) * mm});
            skLineSegment(sketch, "E1510", {"start": v(-475.59, 603.58) * mm, "end": v(-475.06, 603.57) * mm});
            skLineSegment(sketch, "E1511", {"start": v(-475.06, 603.57) * mm, "end": v(-474.53, 603.53) * mm});
            skLineSegment(sketch, "E1512", {"start": v(-474.53, 603.53) * mm, "end": v(-474.06, 603.53) * mm});
            skLineSegment(sketch, "E1513", {"start": v(-474.06, 603.53) * mm, "end": v(-473.59, 603.53) * mm});
            skLineSegment(sketch, "E1514", {"start": v(-473.59, 603.53) * mm, "end": v(-473.12, 603.54) * mm});
            skLineSegment(sketch, "E1515", {"start": v(-473.12, 603.54) * mm, "end": v(-472.65, 603.56) * mm});
            skLineSegment(sketch, "E1516", {"start": v(-472.65, 603.56) * mm, "end": v(-472.18, 603.58) * mm});
            skLineSegment(sketch, "E1517", {"start": v(-472.18, 603.58) * mm, "end": v(-471.7, 603.62) * mm});
            skLineSegment(sketch, "E1518", {"start": v(-471.7, 603.62) * mm, "end": v(-471.24, 603.66) * mm});
            skLineSegment(sketch, "E1519", {"start": v(-471.24, 603.66) * mm, "end": v(-470.77, 603.71) * mm});
            skLineSegment(sketch, "E1520", {"start": v(-470.77, 603.71) * mm, "end": v(-470.3, 603.78) * mm});
            skLineSegment(sketch, "E1521", {"start": v(-470.3, 603.78) * mm, "end": v(-469.84, 603.84) * mm});
            skLineSegment(sketch, "E1522", {"start": v(-469.84, 603.84) * mm, "end": v(-469.37, 603.92) * mm});
            skLineSegment(sketch, "E1523", {"start": v(-469.37, 603.92) * mm, "end": v(-468.9, 604) * mm});
            skLineSegment(sketch, "E1524", {"start": v(-468.9, 604) * mm, "end": v(-468.45, 604.1) * mm});
            skLineSegment(sketch, "E1525", {"start": v(-468.45, 604.1) * mm, "end": v(-467.99, 604.2) * mm});
            skLineSegment(sketch, "E1526", {"start": v(-467.99, 604.2) * mm, "end": v(-467.53, 604.32) * mm});
            skLineSegment(sketch, "E1527", {"start": v(-467.53, 604.32) * mm, "end": v(-467.08, 604.44) * mm});
            skLineSegment(sketch, "E1528", {"start": v(-480.14, 612.67) * mm, "end": v(-480.14, 636.8) * mm});
            skLineSegment(sketch, "E1529", {"start": v(-466.64, 656.07) * mm, "end": v(-466.64, 655.55) * mm});
            skLineSegment(sketch, "E1530", {"start": v(-466.64, 655.55) * mm, "end": v(-466.67, 655.04) * mm});
            skLineSegment(sketch, "E1531", {"start": v(-466.67, 655.04) * mm, "end": v(-466.72, 654.53) * mm});
            skLineSegment(sketch, "E1532", {"start": v(-466.72, 654.53) * mm, "end": v(-466.8, 654.03) * mm});
            skLineSegment(sketch, "E1533", {"start": v(-466.8, 654.03) * mm, "end": v(-466.9, 653.53) * mm});
            skLineSegment(sketch, "E1534", {"start": v(-466.9, 653.53) * mm, "end": v(-467.03, 653.04) * mm});
            skLineSegment(sketch, "E1535", {"start": v(-467.03, 653.04) * mm, "end": v(-467.18, 652.55) * mm});
            skLineSegment(sketch, "E1536", {"start": v(-467.18, 652.55) * mm, "end": v(-467.36, 652.08) * mm});
            skLineSegment(sketch, "E1537", {"start": v(-467.36, 652.08) * mm, "end": v(-467.56, 651.61) * mm});
            skLineSegment(sketch, "E1538", {"start": v(-467.56, 651.61) * mm, "end": v(-467.78, 651.15) * mm});
            skLineSegment(sketch, "E1539", {"start": v(-467.78, 651.15) * mm, "end": v(-468.03, 650.71) * mm});
            skLineSegment(sketch, "E1540", {"start": v(-468.03, 650.71) * mm, "end": v(-468.3, 650.28) * mm});
            skLineSegment(sketch, "E1541", {"start": v(-468.3, 650.28) * mm, "end": v(-468.59, 649.86) * mm});
            skLineSegment(sketch, "E1542", {"start": v(-468.59, 649.86) * mm, "end": v(-468.9, 649.46) * mm});
            skLineSegment(sketch, "E1543", {"start": v(-468.9, 649.46) * mm, "end": v(-469.24, 649.07) * mm});
            skLineSegment(sketch, "E1544", {"start": v(-469.24, 649.07) * mm, "end": v(-469.6, 648.7) * mm});
            skLineSegment(sketch, "E1545", {"start": v(-469.6, 648.7) * mm, "end": v(-469.85, 648.44) * mm});
            skLineSegment(sketch, "E1546", {"start": v(-469.85, 648.44) * mm, "end": v(-470.11, 648.19) * mm});
            skLineSegment(sketch, "E1547", {"start": v(-470.11, 648.19) * mm, "end": v(-470.38, 647.94) * mm});
            skLineSegment(sketch, "E1548", {"start": v(-470.38, 647.94) * mm, "end": v(-470.65, 647.7) * mm});
            skLineSegment(sketch, "E1549", {"start": v(-470.65, 647.7) * mm, "end": v(-470.93, 647.48) * mm});
            skLineSegment(sketch, "E1550", {"start": v(-470.93, 647.48) * mm, "end": v(-471.22, 647.26) * mm});
            skLineSegment(sketch, "E1551", {"start": v(-471.22, 647.26) * mm, "end": v(-471.5, 647.05) * mm});
            skLineSegment(sketch, "E1552", {"start": v(-471.5, 647.05) * mm, "end": v(-471.8, 646.84) * mm});
            skLineSegment(sketch, "E1553", {"start": v(-471.8, 646.84) * mm, "end": v(-472.1, 646.65) * mm});
            skLineSegment(sketch, "E1554", {"start": v(-472.1, 646.65) * mm, "end": v(-472.41, 646.46) * mm});
            skLineSegment(sketch, "E1555", {"start": v(-472.41, 646.46) * mm, "end": v(-472.72, 646.28) * mm});
            skLineSegment(sketch, "E1556", {"start": v(-472.72, 646.28) * mm, "end": v(-473.03, 646.1) * mm});
            skLineSegment(sketch, "E1557", {"start": v(-473.03, 646.1) * mm, "end": v(-473.35, 645.94) * mm});
            skLineSegment(sketch, "E1558", {"start": v(-473.35, 645.94) * mm, "end": v(-473.68, 645.79) * mm});
            skLineSegment(sketch, "E1559", {"start": v(-473.68, 645.79) * mm, "end": v(-474, 645.64) * mm});
            skLineSegment(sketch, "E1560", {"start": v(-474, 645.64) * mm, "end": v(-474.33, 645.5) * mm});
            skLineSegment(sketch, "E1561", {"start": v(-474.33, 645.5) * mm, "end": v(-474.66, 645.37) * mm});
            skLineSegment(sketch, "E1562", {"start": v(-474.66, 645.37) * mm, "end": v(-475, 645.25) * mm});
            skLineSegment(sketch, "E1563", {"start": v(-475, 645.25) * mm, "end": v(-475.34, 645.14) * mm});
            skLineSegment(sketch, "E1564", {"start": v(-475.34, 645.14) * mm, "end": v(-475.68, 645.04) * mm});
            skLineSegment(sketch, "E1565", {"start": v(-475.68, 645.04) * mm, "end": v(-476.03, 644.94) * mm});
            skLineSegment(sketch, "E1566", {"start": v(-476.03, 644.94) * mm, "end": v(-476.38, 644.85) * mm});
            skLineSegment(sketch, "E1567", {"start": v(-476.38, 644.85) * mm, "end": v(-476.73, 644.78) * mm});
            skLineSegment(sketch, "E1568", {"start": v(-476.73, 644.78) * mm, "end": v(-477.08, 644.7) * mm});
            skLineSegment(sketch, "E1569", {"start": v(-477.08, 644.7) * mm, "end": v(-477.43, 644.65) * mm});
            skLineSegment(sketch, "E1570", {"start": v(-477.43, 644.65) * mm, "end": v(-477.79, 644.6) * mm});
            skLineSegment(sketch, "E1571", {"start": v(-477.79, 644.6) * mm, "end": v(-478.15, 644.56) * mm});
            skLineSegment(sketch, "E1572", {"start": v(-478.15, 644.56) * mm, "end": v(-478.5, 644.53) * mm});
            skLineSegment(sketch, "E1573", {"start": v(-478.5, 644.53) * mm, "end": v(-478.87, 644.5) * mm});
            skLineSegment(sketch, "E1574", {"start": v(-478.87, 644.5) * mm, "end": v(-479.23, 644.5) * mm});
            skLineSegment(sketch, "E1575", {"start": v(-479.23, 644.5) * mm, "end": v(-479.6, 644.5) * mm});
            skLineSegment(sketch, "E1576", {"start": v(-479.6, 644.5) * mm, "end": v(-479.96, 644.5) * mm});
            skLineSegment(sketch, "E1577", {"start": v(-479.96, 644.5) * mm, "end": v(-480.32, 644.49) * mm});
            skLineSegment(sketch, "E1578", {"start": v(-480.32, 644.49) * mm, "end": v(-480.68, 644.48) * mm});
            skLineSegment(sketch, "E1579", {"start": v(-480.68, 644.48) * mm, "end": v(-481.04, 644.49) * mm});
            skLineSegment(sketch, "E1580", {"start": v(-481.04, 644.49) * mm, "end": v(-481.4, 644.5) * mm});
            skLineSegment(sketch, "E1581", {"start": v(-481.4, 644.5) * mm, "end": v(-481.76, 644.52) * mm});
            skLineSegment(sketch, "E1582", {"start": v(-481.76, 644.52) * mm, "end": v(-482.12, 644.55) * mm});
            skLineSegment(sketch, "E1583", {"start": v(-482.12, 644.55) * mm, "end": v(-482.47, 644.6) * mm});
            skLineSegment(sketch, "E1584", {"start": v(-482.47, 644.6) * mm, "end": v(-482.83, 644.64) * mm});
            skLineSegment(sketch, "E1585", {"start": v(-482.83, 644.64) * mm, "end": v(-483.18, 644.7) * mm});
            skLineSegment(sketch, "E1586", {"start": v(-483.18, 644.7) * mm, "end": v(-483.54, 644.76) * mm});
            skLineSegment(sketch, "E1587", {"start": v(-483.54, 644.76) * mm, "end": v(-483.89, 644.83) * mm});
            skLineSegment(sketch, "E1588", {"start": v(-483.89, 644.83) * mm, "end": v(-484.23, 644.92) * mm});
            skLineSegment(sketch, "E1589", {"start": v(-484.23, 644.92) * mm, "end": v(-484.58, 645) * mm});
            skLineSegment(sketch, "E1590", {"start": v(-484.58, 645) * mm, "end": v(-484.92, 645.1) * mm});
            skLineSegment(sketch, "E1591", {"start": v(-484.92, 645.1) * mm, "end": v(-485.26, 645.21) * mm});
            skLineSegment(sketch, "E1592", {"start": v(-485.26, 645.21) * mm, "end": v(-485.6, 645.33) * mm});
            skLineSegment(sketch, "E1593", {"start": v(-485.6, 645.33) * mm, "end": v(-485.94, 645.45) * mm});
            skLineSegment(sketch, "E1594", {"start": v(-485.94, 645.45) * mm, "end": v(-486.27, 645.58) * mm});
            skLineSegment(sketch, "E1595", {"start": v(-486.27, 645.58) * mm, "end": v(-486.6, 645.72) * mm});
            skLineSegment(sketch, "E1596", {"start": v(-486.6, 645.72) * mm, "end": v(-486.92, 645.87) * mm});
            skLineSegment(sketch, "E1597", {"start": v(-486.92, 645.87) * mm, "end": v(-487.24, 646.03) * mm});
            skLineSegment(sketch, "E1598", {"start": v(-487.24, 646.03) * mm, "end": v(-487.56, 646.2) * mm});
            skLineSegment(sketch, "E1599", {"start": v(-487.56, 646.2) * mm, "end": v(-487.88, 646.36) * mm});
            skLineSegment(sketch, "E1600", {"start": v(-487.88, 646.36) * mm, "end": v(-488.19, 646.54) * mm});
            skLineSegment(sketch, "E1601", {"start": v(-488.19, 646.54) * mm, "end": v(-488.5, 646.73) * mm});
            skLineSegment(sketch, "E1602", {"start": v(-488.5, 646.73) * mm, "end": v(-488.8, 646.92) * mm});
            skLineSegment(sketch, "E1603", {"start": v(-488.8, 646.92) * mm, "end": v(-489.1, 647.13) * mm});
            skLineSegment(sketch, "E1604", {"start": v(-489.1, 647.13) * mm, "end": v(-489.38, 647.34) * mm});
            skLineSegment(sketch, "E1605", {"start": v(-489.38, 647.34) * mm, "end": v(-489.67, 647.55) * mm});
            skLineSegment(sketch, "E1606", {"start": v(-489.67, 647.55) * mm, "end": v(-489.95, 647.78) * mm});
            skLineSegment(sketch, "E1607", {"start": v(-489.95, 647.78) * mm, "end": v(-490.23, 648) * mm});
            skLineSegment(sketch, "E1608", {"start": v(-490.23, 648) * mm, "end": v(-490.5, 648.25) * mm});
            skLineSegment(sketch, "E1609", {"start": v(-490.5, 648.25) * mm, "end": v(-490.87, 648.65) * mm});
            skLineSegment(sketch, "E1610", {"start": v(-490.87, 648.65) * mm, "end": v(-491.2, 649.07) * mm});
            skLineSegment(sketch, "E1611", {"start": v(-491.2, 649.07) * mm, "end": v(-491.53, 649.5) * mm});
            skLineSegment(sketch, "E1612", {"start": v(-491.53, 649.5) * mm, "end": v(-491.83, 649.95) * mm});
            skLineSegment(sketch, "E1613", {"start": v(-491.83, 649.95) * mm, "end": v(-492.11, 650.4) * mm});
            skLineSegment(sketch, "E1614", {"start": v(-492.11, 650.4) * mm, "end": v(-492.37, 650.88) * mm});
            skLineSegment(sketch, "E1615", {"start": v(-492.37, 650.88) * mm, "end": v(-492.6, 651.37) * mm});
            skLineSegment(sketch, "E1616", {"start": v(-492.6, 651.37) * mm, "end": v(-492.8, 651.86) * mm});
            skLineSegment(sketch, "E1617", {"start": v(-492.8, 651.86) * mm, "end": v(-493, 652.36) * mm});
            skLineSegment(sketch, "E1618", {"start": v(-493, 652.36) * mm, "end": v(-493.16, 652.87) * mm});
            skLineSegment(sketch, "E1619", {"start": v(-493.16, 652.87) * mm, "end": v(-493.3, 653.4) * mm});
            skLineSegment(sketch, "E1620", {"start": v(-493.3, 653.4) * mm, "end": v(-493.41, 653.92) * mm});
            skLineSegment(sketch, "E1621", {"start": v(-493.41, 653.92) * mm, "end": v(-493.5, 654.45) * mm});
            skLineSegment(sketch, "E1622", {"start": v(-493.5, 654.45) * mm, "end": v(-493.56, 654.98) * mm});
            skLineSegment(sketch, "E1623", {"start": v(-493.56, 654.98) * mm, "end": v(-493.6, 655.52) * mm});
            skLineSegment(sketch, "E1624", {"start": v(-493.6, 655.52) * mm, "end": v(-493.61, 656.07) * mm});
            skLineSegment(sketch, "E1625", {"start": v(-493.61, 656.07) * mm, "end": v(-493.59, 656.6) * mm});
            skLineSegment(sketch, "E1626", {"start": v(-493.59, 656.6) * mm, "end": v(-493.54, 657.11) * mm});
            skLineSegment(sketch, "E1627", {"start": v(-493.54, 657.11) * mm, "end": v(-493.46, 657.63) * mm});
            skLineSegment(sketch, "E1628", {"start": v(-493.46, 657.63) * mm, "end": v(-493.35, 658.14) * mm});
            skLineSegment(sketch, "E1629", {"start": v(-493.35, 658.14) * mm, "end": v(-493.22, 658.64) * mm});
            skLineSegment(sketch, "E1630", {"start": v(-493.22, 658.64) * mm, "end": v(-493.06, 659.14) * mm});
            skLineSegment(sketch, "E1631", {"start": v(-493.06, 659.14) * mm, "end": v(-492.87, 659.62) * mm});
            skLineSegment(sketch, "E1632", {"start": v(-492.87, 659.62) * mm, "end": v(-492.66, 660.1) * mm});
            skLineSegment(sketch, "E1633", {"start": v(-492.66, 660.1) * mm, "end": v(-492.43, 660.56) * mm});
            skLineSegment(sketch, "E1634", {"start": v(-492.43, 660.56) * mm, "end": v(-492.17, 661) * mm});
            skLineSegment(sketch, "E1635", {"start": v(-492.17, 661) * mm, "end": v(-491.9, 661.45) * mm});
            skLineSegment(sketch, "E1636", {"start": v(-491.9, 661.45) * mm, "end": v(-491.59, 661.87) * mm});
            skLineSegment(sketch, "E1637", {"start": v(-491.59, 661.87) * mm, "end": v(-491.26, 662.27) * mm});
            skLineSegment(sketch, "E1638", {"start": v(-491.26, 662.27) * mm, "end": v(-490.91, 662.66) * mm});
            skLineSegment(sketch, "E1639", {"start": v(-490.91, 662.66) * mm, "end": v(-490.54, 663.04) * mm});
            skLineSegment(sketch, "E1640", {"start": v(-490.54, 663.04) * mm, "end": v(-490.15, 663.39) * mm});
            skLineSegment(sketch, "E1641", {"start": v(-490.15, 663.39) * mm, "end": v(-489.9, 663.63) * mm});
            skLineSegment(sketch, "E1642", {"start": v(-489.9, 663.63) * mm, "end": v(-489.63, 663.86) * mm});
            skLineSegment(sketch, "E1643", {"start": v(-489.63, 663.86) * mm, "end": v(-489.36, 664.09) * mm});
            skLineSegment(sketch, "E1644", {"start": v(-489.36, 664.09) * mm, "end": v(-489.09, 664.3) * mm});
            skLineSegment(sketch, "E1645", {"start": v(-489.09, 664.3) * mm, "end": v(-488.8, 664.52) * mm});
            skLineSegment(sketch, "E1646", {"start": v(-488.8, 664.52) * mm, "end": v(-488.52, 664.72) * mm});
            skLineSegment(sketch, "E1647", {"start": v(-488.52, 664.72) * mm, "end": v(-488.23, 664.91) * mm});
            skLineSegment(sketch, "E1648", {"start": v(-488.23, 664.91) * mm, "end": v(-487.94, 665.1) * mm});
            skLineSegment(sketch, "E1649", {"start": v(-487.94, 665.1) * mm, "end": v(-487.64, 665.28) * mm});
            skLineSegment(sketch, "E1650", {"start": v(-487.64, 665.28) * mm, "end": v(-487.34, 665.45) * mm});
            skLineSegment(sketch, "E1651", {"start": v(-487.34, 665.45) * mm, "end": v(-487.03, 665.62) * mm});
            skLineSegment(sketch, "E1652", {"start": v(-487.03, 665.62) * mm, "end": v(-486.72, 665.77) * mm});
            skLineSegment(sketch, "E1653", {"start": v(-486.72, 665.77) * mm, "end": v(-486.4, 665.92) * mm});
            skLineSegment(sketch, "E1654", {"start": v(-486.4, 665.92) * mm, "end": v(-486.09, 666.06) * mm});
            skLineSegment(sketch, "E1655", {"start": v(-486.09, 666.06) * mm, "end": v(-485.77, 666.19) * mm});
            skLineSegment(sketch, "E1656", {"start": v(-485.77, 666.19) * mm, "end": v(-485.44, 666.31) * mm});
            skLineSegment(sketch, "E1657", {"start": v(-485.44, 666.31) * mm, "end": v(-485.11, 666.43) * mm});
            skLineSegment(sketch, "E1658", {"start": v(-485.11, 666.43) * mm, "end": v(-484.78, 666.53) * mm});
            skLineSegment(sketch, "E1659", {"start": v(-484.78, 666.53) * mm, "end": v(-484.45, 666.63) * mm});
            skLineSegment(sketch, "E1660", {"start": v(-484.45, 666.63) * mm, "end": v(-484.12, 666.72) * mm});
            skLineSegment(sketch, "E1661", {"start": v(-484.12, 666.72) * mm, "end": v(-483.78, 666.8) * mm});
            skLineSegment(sketch, "E1662", {"start": v(-483.78, 666.8) * mm, "end": v(-483.44, 666.87) * mm});
            skLineSegment(sketch, "E1663", {"start": v(-483.44, 666.87) * mm, "end": v(-483.1, 666.94) * mm});
            skLineSegment(sketch, "E1664", {"start": v(-483.1, 666.94) * mm, "end": v(-482.75, 667) * mm});
            skLineSegment(sketch, "E1665", {"start": v(-482.75, 667) * mm, "end": v(-482.4, 667.04) * mm});
            skLineSegment(sketch, "E1666", {"start": v(-482.4, 667.04) * mm, "end": v(-482.06, 667.07) * mm});
            skLineSegment(sketch, "E1667", {"start": v(-482.06, 667.07) * mm, "end": v(-481.71, 667.1) * mm});
            skLineSegment(sketch, "E1668", {"start": v(-481.71, 667.1) * mm, "end": v(-481.36, 667.12) * mm});
            skLineSegment(sketch, "E1669", {"start": v(-481.36, 667.12) * mm, "end": v(-481.01, 667.13) * mm});
            skLineSegment(sketch, "E1670", {"start": v(-481.01, 667.13) * mm, "end": v(-480.66, 667.13) * mm});
            skLineSegment(sketch, "E1671", {"start": v(-480.66, 667.13) * mm, "end": v(-480.3, 667.12) * mm});
            skLineSegment(sketch, "E1672", {"start": v(-480.3, 667.12) * mm, "end": v(-479.96, 667.1) * mm});
            skLineSegment(sketch, "E1673", {"start": v(-479.96, 667.1) * mm, "end": v(-479.6, 667.11) * mm});
            skLineSegment(sketch, "E1674", {"start": v(-479.6, 667.11) * mm, "end": v(-479.26, 667.12) * mm});
            skLineSegment(sketch, "E1675", {"start": v(-479.26, 667.12) * mm, "end": v(-478.9, 667.11) * mm});
            skLineSegment(sketch, "E1676", {"start": v(-478.9, 667.11) * mm, "end": v(-478.56, 667.1) * mm});
            skLineSegment(sketch, "E1677", {"start": v(-478.56, 667.1) * mm, "end": v(-478.21, 667.07) * mm});
            skLineSegment(sketch, "E1678", {"start": v(-478.21, 667.07) * mm, "end": v(-477.87, 667.04) * mm});
            skLineSegment(sketch, "E1679", {"start": v(-477.87, 667.04) * mm, "end": v(-477.52, 667) * mm});
            skLineSegment(sketch, "E1680", {"start": v(-477.52, 667) * mm, "end": v(-477.18, 666.95) * mm});
            skLineSegment(sketch, "E1681", {"start": v(-477.18, 666.95) * mm, "end": v(-476.84, 666.9) * mm});
            skLineSegment(sketch, "E1682", {"start": v(-476.84, 666.9) * mm, "end": v(-476.5, 666.82) * mm});
            skLineSegment(sketch, "E1683", {"start": v(-476.5, 666.82) * mm, "end": v(-476.17, 666.75) * mm});
            skLineSegment(sketch, "E1684", {"start": v(-476.17, 666.75) * mm, "end": v(-475.83, 666.67) * mm});
            skLineSegment(sketch, "E1685", {"start": v(-475.83, 666.67) * mm, "end": v(-475.5, 666.57) * mm});
            skLineSegment(sketch, "E1686", {"start": v(-475.5, 666.57) * mm, "end": v(-475.17, 666.47) * mm});
            skLineSegment(sketch, "E1687", {"start": v(-475.17, 666.47) * mm, "end": v(-474.84, 666.37) * mm});
            skLineSegment(sketch, "E1688", {"start": v(-474.84, 666.37) * mm, "end": v(-474.52, 666.25) * mm});
            skLineSegment(sketch, "E1689", {"start": v(-474.52, 666.25) * mm, "end": v(-474.2, 666.13) * mm});
            skLineSegment(sketch, "E1690", {"start": v(-474.2, 666.13) * mm, "end": v(-473.88, 666) * mm});
            skLineSegment(sketch, "E1691", {"start": v(-473.88, 666) * mm, "end": v(-473.56, 665.85) * mm});
            skLineSegment(sketch, "E1692", {"start": v(-473.56, 665.85) * mm, "end": v(-473.25, 665.7) * mm});
            skLineSegment(sketch, "E1693", {"start": v(-473.25, 665.7) * mm, "end": v(-472.94, 665.55) * mm});
            skLineSegment(sketch, "E1694", {"start": v(-472.94, 665.55) * mm, "end": v(-472.64, 665.39) * mm});
            skLineSegment(sketch, "E1695", {"start": v(-472.64, 665.39) * mm, "end": v(-472.34, 665.22) * mm});
            skLineSegment(sketch, "E1696", {"start": v(-472.34, 665.22) * mm, "end": v(-472.04, 665.04) * mm});
            skLineSegment(sketch, "E1697", {"start": v(-472.04, 665.04) * mm, "end": v(-471.75, 664.85) * mm});
            skLineSegment(sketch, "E1698", {"start": v(-471.75, 664.85) * mm, "end": v(-471.47, 664.66) * mm});
            skLineSegment(sketch, "E1699", {"start": v(-471.47, 664.66) * mm, "end": v(-471.18, 664.46) * mm});
            skLineSegment(sketch, "E1700", {"start": v(-471.18, 664.46) * mm, "end": v(-470.9, 664.25) * mm});
            skLineSegment(sketch, "E1701", {"start": v(-470.9, 664.25) * mm, "end": v(-470.63, 664.03) * mm});
            skLineSegment(sketch, "E1702", {"start": v(-470.63, 664.03) * mm, "end": v(-470.36, 663.8) * mm});
            skLineSegment(sketch, "E1703", {"start": v(-470.36, 663.8) * mm, "end": v(-470.1, 663.58) * mm});
            skLineSegment(sketch, "E1704", {"start": v(-470.1, 663.58) * mm, "end": v(-469.85, 663.34) * mm});
            skLineSegment(sketch, "E1705", {"start": v(-469.85, 663.34) * mm, "end": v(-469.48, 662.98) * mm});
            skLineSegment(sketch, "E1706", {"start": v(-469.48, 662.98) * mm, "end": v(-469.13, 662.6) * mm});
            skLineSegment(sketch, "E1707", {"start": v(-469.13, 662.6) * mm, "end": v(-468.8, 662.2) * mm});
            skLineSegment(sketch, "E1708", {"start": v(-468.8, 662.2) * mm, "end": v(-468.5, 661.8) * mm});
            skLineSegment(sketch, "E1709", {"start": v(-468.5, 661.8) * mm, "end": v(-468.21, 661.38) * mm});
            skLineSegment(sketch, "E1710", {"start": v(-468.21, 661.38) * mm, "end": v(-467.95, 660.94) * mm});
            skLineSegment(sketch, "E1711", {"start": v(-467.95, 660.94) * mm, "end": v(-467.71, 660.5) * mm});
            skLineSegment(sketch, "E1712", {"start": v(-467.71, 660.5) * mm, "end": v(-467.5, 660.03) * mm});
            skLineSegment(sketch, "E1713", {"start": v(-467.5, 660.03) * mm, "end": v(-467.3, 659.56) * mm});
            skLineSegment(sketch, "E1714", {"start": v(-467.3, 659.56) * mm, "end": v(-467.13, 659.09) * mm});
            skLineSegment(sketch, "E1715", {"start": v(-467.13, 659.09) * mm, "end": v(-466.99, 658.6) * mm});
            skLineSegment(sketch, "E1716", {"start": v(-466.99, 658.6) * mm, "end": v(-466.87, 658.1) * mm});
            skLineSegment(sketch, "E1717", {"start": v(-466.87, 658.1) * mm, "end": v(-466.77, 657.6) * mm});
            skLineSegment(sketch, "E1718", {"start": v(-466.77, 657.6) * mm, "end": v(-466.7, 657.1) * mm});
            skLineSegment(sketch, "E1719", {"start": v(-466.7, 657.1) * mm, "end": v(-466.66, 656.58) * mm});
            skLineSegment(sketch, "E1720", {"start": v(-466.66, 656.58) * mm, "end": v(-466.64, 656.07) * mm});
            skLineSegment(sketch, "E1721", {"start": v(-467.06, 694) * mm, "end": v(-493.2, 694) * mm});
            skLineSegment(sketch, "E1722", {"start": v(-476.5, 694) * mm, "end": v(-476.02, 693.99) * mm});
            skLineSegment(sketch, "E1723", {"start": v(-476.02, 693.99) * mm, "end": v(-475.54, 693.94) * mm});
            skLineSegment(sketch, "E1724", {"start": v(-475.54, 693.94) * mm, "end": v(-475.07, 693.88) * mm});
            skLineSegment(sketch, "E1725", {"start": v(-475.07, 693.88) * mm, "end": v(-474.61, 693.78) * mm});
            skLineSegment(sketch, "E1726", {"start": v(-474.61, 693.78) * mm, "end": v(-474.15, 693.67) * mm});
            skLineSegment(sketch, "E1727", {"start": v(-474.15, 693.67) * mm, "end": v(-473.7, 693.54) * mm});
            skLineSegment(sketch, "E1728", {"start": v(-473.7, 693.54) * mm, "end": v(-473.26, 693.38) * mm});
            skLineSegment(sketch, "E1729", {"start": v(-473.26, 693.38) * mm, "end": v(-472.82, 693.2) * mm});
            skLineSegment(sketch, "E1730", {"start": v(-472.82, 693.2) * mm, "end": v(-472.4, 693) * mm});
            skLineSegment(sketch, "E1731", {"start": v(-472.4, 693) * mm, "end": v(-471.98, 692.78) * mm});
            skLineSegment(sketch, "E1732", {"start": v(-471.98, 692.78) * mm, "end": v(-471.57, 692.54) * mm});
            skLineSegment(sketch, "E1733", {"start": v(-471.57, 692.54) * mm, "end": v(-471.18, 692.27) * mm});
            skLineSegment(sketch, "E1734", {"start": v(-471.18, 692.27) * mm, "end": v(-470.8, 692) * mm});
            skLineSegment(sketch, "E1735", {"start": v(-470.8, 692) * mm, "end": v(-470.44, 691.7) * mm});
            skLineSegment(sketch, "E1736", {"start": v(-470.44, 691.7) * mm, "end": v(-470.08, 691.37) * mm});
            skLineSegment(sketch, "E1737", {"start": v(-470.08, 691.37) * mm, "end": v(-469.75, 691.03) * mm});
            skLineSegment(sketch, "E1738", {"start": v(-469.75, 691.03) * mm, "end": v(-469.4, 690.69) * mm});
            skLineSegment(sketch, "E1739", {"start": v(-469.4, 690.69) * mm, "end": v(-469.1, 690.33) * mm});
            skLineSegment(sketch, "E1740", {"start": v(-469.1, 690.33) * mm, "end": v(-468.8, 689.96) * mm});
            skLineSegment(sketch, "E1741", {"start": v(-468.8, 689.96) * mm, "end": v(-468.51, 689.57) * mm});
            skLineSegment(sketch, "E1742", {"start": v(-468.51, 689.57) * mm, "end": v(-468.25, 689.17) * mm});
            skLineSegment(sketch, "E1743", {"start": v(-468.25, 689.17) * mm, "end": v(-468.01, 688.76) * mm});
            skLineSegment(sketch, "E1744", {"start": v(-468.01, 688.76) * mm, "end": v(-467.8, 688.34) * mm});
            skLineSegment(sketch, "E1745", {"start": v(-467.8, 688.34) * mm, "end": v(-467.6, 687.9) * mm});
            skLineSegment(sketch, "E1746", {"start": v(-467.6, 687.9) * mm, "end": v(-467.42, 687.46) * mm});
            skLineSegment(sketch, "E1747", {"start": v(-467.42, 687.46) * mm, "end": v(-467.27, 687.01) * mm});
            skLineSegment(sketch, "E1748", {"start": v(-467.27, 687.01) * mm, "end": v(-467.13, 686.55) * mm});
            skLineSegment(sketch, "E1749", {"start": v(-467.13, 686.55) * mm, "end": v(-467.03, 686.1) * mm});
            skLineSegment(sketch, "E1750", {"start": v(-467.03, 686.1) * mm, "end": v(-466.94, 685.62) * mm});
            skLineSegment(sketch, "E1751", {"start": v(-466.94, 685.62) * mm, "end": v(-466.88, 685.15) * mm});
            skLineSegment(sketch, "E1752", {"start": v(-466.88, 685.15) * mm, "end": v(-466.84, 684.67) * mm});
            skLineSegment(sketch, "E1753", {"start": v(-466.84, 684.67) * mm, "end": v(-466.82, 684.19) * mm});
            skLineSegment(sketch, "E1754", {"start": v(-466.82, 684.19) * mm, "end": v(-466.79, 683.72) * mm});
            skLineSegment(sketch, "E1755", {"start": v(-466.79, 683.72) * mm, "end": v(-466.77, 683.25) * mm});
            skLineSegment(sketch, "E1756", {"start": v(-466.77, 683.25) * mm, "end": v(-466.78, 682.78) * mm});
            skLineSegment(sketch, "E1757", {"start": v(-466.78, 682.78) * mm, "end": v(-466.82, 682.3) * mm});
            skLineSegment(sketch, "E1758", {"start": v(-466.82, 682.3) * mm, "end": v(-466.87, 681.85) * mm});
            skLineSegment(sketch, "E1759", {"start": v(-466.87, 681.85) * mm, "end": v(-466.95, 681.39) * mm});
            skLineSegment(sketch, "E1760", {"start": v(-466.95, 681.39) * mm, "end": v(-467.06, 680.93) * mm});
            skLineSegment(sketch, "E1761", {"start": v(-467.06, 680.93) * mm, "end": v(-467.18, 680.48) * mm});
            skLineSegment(sketch, "E1762", {"start": v(-467.18, 680.48) * mm, "end": v(-467.33, 680.04) * mm});
            skLineSegment(sketch, "E1763", {"start": v(-467.33, 680.04) * mm, "end": v(-467.5, 679.6) * mm});
            skLineSegment(sketch, "E1764", {"start": v(-467.5, 679.6) * mm, "end": v(-467.68, 679.18) * mm});
            skLineSegment(sketch, "E1765", {"start": v(-467.68, 679.18) * mm, "end": v(-467.9, 678.76) * mm});
            skLineSegment(sketch, "E1766", {"start": v(-467.9, 678.76) * mm, "end": v(-468.13, 678.36) * mm});
            skLineSegment(sketch, "E1767", {"start": v(-468.13, 678.36) * mm, "end": v(-468.38, 677.96) * mm});
            skLineSegment(sketch, "E1768", {"start": v(-468.38, 677.96) * mm, "end": v(-468.65, 677.58) * mm});
            skLineSegment(sketch, "E1769", {"start": v(-468.65, 677.58) * mm, "end": v(-468.94, 677.2) * mm});
            skLineSegment(sketch, "E1770", {"start": v(-468.94, 677.2) * mm, "end": v(-469.26, 676.93) * mm});
            skLineSegment(sketch, "E1771", {"start": v(-469.26, 676.93) * mm, "end": v(-469.59, 676.66) * mm});
            skLineSegment(sketch, "E1772", {"start": v(-469.59, 676.66) * mm, "end": v(-469.93, 676.42) * mm});
            skLineSegment(sketch, "E1773", {"start": v(-469.93, 676.42) * mm, "end": v(-470.28, 676.19) * mm});
            skLineSegment(sketch, "E1774", {"start": v(-470.28, 676.19) * mm, "end": v(-470.64, 675.98) * mm});
            skLineSegment(sketch, "E1775", {"start": v(-470.64, 675.98) * mm, "end": v(-471.02, 675.8) * mm});
            skLineSegment(sketch, "E1776", {"start": v(-471.02, 675.8) * mm, "end": v(-471.4, 675.62) * mm});
            skLineSegment(sketch, "E1777", {"start": v(-471.4, 675.62) * mm, "end": v(-471.79, 675.47) * mm});
            skLineSegment(sketch, "E1778", {"start": v(-471.79, 675.47) * mm, "end": v(-472.18, 675.34) * mm});
            skLineSegment(sketch, "E1779", {"start": v(-472.18, 675.34) * mm, "end": v(-472.59, 675.23) * mm});
            skLineSegment(sketch, "E1780", {"start": v(-472.59, 675.23) * mm, "end": v(-473, 675.14) * mm});
            skLineSegment(sketch, "E1781", {"start": v(-473, 675.14) * mm, "end": v(-473.4, 675.07) * mm});
            skLineSegment(sketch, "E1782", {"start": v(-473.4, 675.07) * mm, "end": v(-473.83, 675.02) * mm});
            skLineSegment(sketch, "E1783", {"start": v(-473.83, 675.02) * mm, "end": v(-474.25, 675) * mm});
            skLineSegment(sketch, "E1784", {"start": v(-474.25, 675) * mm, "end": v(-474.67, 674.99) * mm});
            skLineSegment(sketch, "E1785", {"start": v(-474.67, 674.99) * mm, "end": v(-475.1, 675) * mm});
            skLineSegment(sketch, "E1786", {"start": v(-475.1, 675) * mm, "end": v(-493.2, 675) * mm});
            skLineSegment(sketch, "E1787", {"start": v(-467.2, 710.34) * mm, "end": v(-467.08, 710.11) * mm});
            skLineSegment(sketch, "E1788", {"start": v(-467.08, 710.11) * mm, "end": v(-466.97, 709.87) * mm});
            skLineSegment(sketch, "E1789", {"start": v(-466.97, 709.87) * mm, "end": v(-466.88, 709.63) * mm});
            skLineSegment(sketch, "E1790", {"start": v(-466.88, 709.63) * mm, "end": v(-466.8, 709.38) * mm});
            skLineSegment(sketch, "E1791", {"start": v(-466.8, 709.38) * mm, "end": v(-466.75, 709.12) * mm});
            skLineSegment(sketch, "E1792", {"start": v(-466.75, 709.12) * mm, "end": v(-466.71, 708.86) * mm});
            skLineSegment(sketch, "E1793", {"start": v(-466.71, 708.86) * mm, "end": v(-466.7, 708.6) * mm});
            skLineSegment(sketch, "E1794", {"start": v(-466.7, 708.6) * mm, "end": v(-466.7, 708.34) * mm});
            skLineSegment(sketch, "E1795", {"start": v(-466.7, 708.34) * mm, "end": v(-466.7, 708.15) * mm});
            skLineSegment(sketch, "E1796", {"start": v(-466.7, 708.15) * mm, "end": v(-466.7, 707.96) * mm});
            skLineSegment(sketch, "E1797", {"start": v(-466.7, 707.96) * mm, "end": v(-466.73, 707.77) * mm});
            skLineSegment(sketch, "E1798", {"start": v(-466.73, 707.77) * mm, "end": v(-466.76, 707.59) * mm});
            skLineSegment(sketch, "E1799", {"start": v(-466.76, 707.59) * mm, "end": v(-466.8, 707.4) * mm});
            skLineSegment(sketch, "E1800", {"start": v(-466.8, 707.4) * mm, "end": v(-466.84, 707.22) * mm});
            skLineSegment(sketch, "E1801", {"start": v(-466.84, 707.22) * mm, "end": v(-466.89, 707.04) * mm});
            skLineSegment(sketch, "E1802", {"start": v(-466.89, 707.04) * mm, "end": v(-466.95, 706.86) * mm});
            skLineSegment(sketch, "E1803", {"start": v(-466.95, 706.86) * mm, "end": v(-467.02, 706.69) * mm});
            skLineSegment(sketch, "E1804", {"start": v(-467.02, 706.69) * mm, "end": v(-467.1, 706.51) * mm});
            skLineSegment(sketch, "E1805", {"start": v(-467.1, 706.51) * mm, "end": v(-467.18, 706.35) * mm});
            skLineSegment(sketch, "E1806", {"start": v(-467.18, 706.35) * mm, "end": v(-467.27, 706.18) * mm});
            skLineSegment(sketch, "E1807", {"start": v(-467.27, 706.18) * mm, "end": v(-467.37, 706.02) * mm});
            skLineSegment(sketch, "E1808", {"start": v(-467.37, 706.02) * mm, "end": v(-467.47, 705.86) * mm});
            skLineSegment(sketch, "E1809", {"start": v(-467.47, 705.86) * mm, "end": v(-467.58, 705.71) * mm});
            skLineSegment(sketch, "E1810", {"start": v(-467.58, 705.71) * mm, "end": v(-467.7, 705.56) * mm});
            skLineSegment(sketch, "E1811", {"start": v(-467.7, 705.56) * mm, "end": v(-467.83, 705.44) * mm});
            skLineSegment(sketch, "E1812", {"start": v(-467.83, 705.44) * mm, "end": v(-467.95, 705.33) * mm});
            skLineSegment(sketch, "E1813", {"start": v(-467.95, 705.33) * mm, "end": v(-468.09, 705.23) * mm});
            skLineSegment(sketch, "E1814", {"start": v(-468.09, 705.23) * mm, "end": v(-468.22, 705.13) * mm});
            skLineSegment(sketch, "E1815", {"start": v(-468.22, 705.13) * mm, "end": v(-468.36, 705.04) * mm});
            skLineSegment(sketch, "E1816", {"start": v(-468.36, 705.04) * mm, "end": v(-468.5, 704.95) * mm});
            skLineSegment(sketch, "E1817", {"start": v(-468.5, 704.95) * mm, "end": v(-468.66, 704.87) * mm});
            skLineSegment(sketch, "E1818", {"start": v(-468.66, 704.87) * mm, "end": v(-468.81, 704.8) * mm});
            skLineSegment(sketch, "E1819", {"start": v(-468.81, 704.8) * mm, "end": v(-468.97, 704.74) * mm});
            skLineSegment(sketch, "E1820", {"start": v(-468.97, 704.74) * mm, "end": v(-469.13, 704.69) * mm});
            skLineSegment(sketch, "E1821", {"start": v(-469.13, 704.69) * mm, "end": v(-469.29, 704.64) * mm});
            skLineSegment(sketch, "E1822", {"start": v(-469.29, 704.64) * mm, "end": v(-469.45, 704.6) * mm});
            skLineSegment(sketch, "E1823", {"start": v(-469.45, 704.6) * mm, "end": v(-469.62, 704.58) * mm});
            skLineSegment(sketch, "E1824", {"start": v(-469.62, 704.58) * mm, "end": v(-469.79, 704.55) * mm});
            skLineSegment(sketch, "E1825", {"start": v(-469.79, 704.55) * mm, "end": v(-469.96, 704.54) * mm});
            skLineSegment(sketch, "E1826", {"start": v(-469.96, 704.54) * mm, "end": v(-470.13, 704.54) * mm});
            skLineSegment(sketch, "E1827", {"start": v(-470.13, 704.54) * mm, "end": v(-500.49, 704.54) * mm});
            skLineSegment(sketch, "E1828", {"start": v(-493.36, 701.9) * mm, "end": v(-493.36, 709.97) * mm});
            skLineSegment(sketch, "E1829", {"start": v(-257.88, 154.18) * mm, "end": v(-217.88, 154.18) * mm});
            skLineSegment(sketch, "E1830", {"start": v(-217.88, 154.18) * mm, "end": v(-217.88, 129.31) * mm});
            skLineSegment(sketch, "E1831", {"start": v(-237, 154.18) * mm, "end": v(-237, 131.1) * mm});
            skLineSegment(sketch, "E1832", {"start": v(-257.86, 67.88) * mm, "end": v(-217.88, 45.41) * mm});
            skLineSegment(sketch, "E1833", {"start": v(-249.86, 12.59) * mm, "end": v(-250.2, 12.7) * mm});
            skLineSegment(sketch, "E1834", {"start": v(-250.2, 12.7) * mm, "end": v(-250.55, 12.82) * mm});
            skLineSegment(sketch, "E1835", {"start": v(-250.55, 12.82) * mm, "end": v(-250.89, 12.95) * mm});
            skLineSegment(sketch, "E1836", {"start": v(-250.89, 12.95) * mm, "end": v(-251.22, 13.1) * mm});
            skLineSegment(sketch, "E1837", {"start": v(-251.22, 13.1) * mm, "end": v(-251.55, 13.25) * mm});
            skLineSegment(sketch, "E1838", {"start": v(-251.55, 13.25) * mm, "end": v(-251.87, 13.41) * mm});
            skLineSegment(sketch, "E1839", {"start": v(-251.87, 13.41) * mm, "end": v(-252.2, 13.59) * mm});
            skLineSegment(sketch, "E1840", {"start": v(-252.2, 13.59) * mm, "end": v(-252.5, 13.77) * mm});
            skLineSegment(sketch, "E1841", {"start": v(-252.5, 13.77) * mm, "end": v(-252.81, 13.96) * mm});
            skLineSegment(sketch, "E1842", {"start": v(-252.81, 13.96) * mm, "end": v(-253.11, 14.16) * mm});
            skLineSegment(sketch, "E1843", {"start": v(-253.11, 14.16) * mm, "end": v(-253.4, 14.37) * mm});
            skLineSegment(sketch, "E1844", {"start": v(-253.4, 14.37) * mm, "end": v(-253.7, 14.6) * mm});
            skLineSegment(sketch, "E1845", {"start": v(-253.7, 14.6) * mm, "end": v(-253.98, 14.82) * mm});
            skLineSegment(sketch, "E1846", {"start": v(-253.98, 14.82) * mm, "end": v(-254.25, 15.06) * mm});
            skLineSegment(sketch, "E1847", {"start": v(-254.25, 15.06) * mm, "end": v(-254.52, 15.3) * mm});
            skLineSegment(sketch, "E1848", {"start": v(-254.52, 15.3) * mm, "end": v(-254.78, 15.56) * mm});
            skLineSegment(sketch, "E1849", {"start": v(-254.78, 15.56) * mm, "end": v(-255.18, 15.96) * mm});
            skLineSegment(sketch, "E1850", {"start": v(-255.18, 15.96) * mm, "end": v(-255.56, 16.37) * mm});
            skLineSegment(sketch, "E1851", {"start": v(-255.56, 16.37) * mm, "end": v(-255.91, 16.8) * mm});
            skLineSegment(sketch, "E1852", {"start": v(-255.91, 16.8) * mm, "end": v(-256.24, 17.24) * mm});
            skLineSegment(sketch, "E1853", {"start": v(-256.24, 17.24) * mm, "end": v(-256.55, 17.7) * mm});
            skLineSegment(sketch, "E1854", {"start": v(-256.55, 17.7) * mm, "end": v(-256.84, 18.18) * mm});
            skLineSegment(sketch, "E1855", {"start": v(-256.84, 18.18) * mm, "end": v(-257.1, 18.66) * mm});
            skLineSegment(sketch, "E1856", {"start": v(-257.1, 18.66) * mm, "end": v(-257.33, 19.16) * mm});
            skLineSegment(sketch, "E1857", {"start": v(-257.33, 19.16) * mm, "end": v(-257.54, 19.67) * mm});
            skLineSegment(sketch, "E1858", {"start": v(-257.54, 19.67) * mm, "end": v(-257.73, 20.2) * mm});
            skLineSegment(sketch, "E1859", {"start": v(-257.73, 20.2) * mm, "end": v(-257.9, 20.72) * mm});
            skLineSegment(sketch, "E1860", {"start": v(-257.9, 20.72) * mm, "end": v(-258.02, 21.26) * mm});
            skLineSegment(sketch, "E1861", {"start": v(-258.02, 21.26) * mm, "end": v(-258.13, 21.8) * mm});
            skLineSegment(sketch, "E1862", {"start": v(-258.13, 21.8) * mm, "end": v(-258.21, 22.35) * mm});
            skLineSegment(sketch, "E1863", {"start": v(-258.21, 22.35) * mm, "end": v(-258.27, 22.9) * mm});
            skLineSegment(sketch, "E1864", {"start": v(-258.27, 22.9) * mm, "end": v(-258.3, 23.47) * mm});
            skLineSegment(sketch, "E1865", {"start": v(-258.3, 23.47) * mm, "end": v(-258.3, 23.77) * mm});
            skLineSegment(sketch, "E1866", {"start": v(-258.3, 23.77) * mm, "end": v(-258.29, 24.07) * mm});
            skLineSegment(sketch, "E1867", {"start": v(-258.29, 24.07) * mm, "end": v(-258.27, 24.37) * mm});
            skLineSegment(sketch, "E1868", {"start": v(-258.27, 24.37) * mm, "end": v(-258.25, 24.67) * mm});
            skLineSegment(sketch, "E1869", {"start": v(-258.25, 24.67) * mm, "end": v(-258.22, 24.97) * mm});
            skLineSegment(sketch, "E1870", {"start": v(-258.22, 24.97) * mm, "end": v(-258.19, 25.26) * mm});
            skLineSegment(sketch, "E1871", {"start": v(-258.19, 25.26) * mm, "end": v(-258.1, 25.85) * mm});
            skLineSegment(sketch, "E1872", {"start": v(-258.1, 25.85) * mm, "end": v(-257.97, 26.43) * mm});
            skLineSegment(sketch, "E1873", {"start": v(-257.97, 26.43) * mm, "end": v(-257.81, 27) * mm});
            skLineSegment(sketch, "E1874", {"start": v(-257.81, 27) * mm, "end": v(-257.63, 27.57) * mm});
            skLineSegment(sketch, "E1875", {"start": v(-257.63, 27.57) * mm, "end": v(-257.43, 28.13) * mm});
            skLineSegment(sketch, "E1876", {"start": v(-257.43, 28.13) * mm, "end": v(-257.19, 28.68) * mm});
            skLineSegment(sketch, "E1877", {"start": v(-257.19, 28.68) * mm, "end": v(-256.93, 29.2) * mm});
            skLineSegment(sketch, "E1878", {"start": v(-256.93, 29.2) * mm, "end": v(-256.64, 29.73) * mm});
            skLineSegment(sketch, "E1879", {"start": v(-256.64, 29.73) * mm, "end": v(-256.32, 30.23) * mm});
            skLineSegment(sketch, "E1880", {"start": v(-256.32, 30.23) * mm, "end": v(-255.98, 30.72) * mm});
            skLineSegment(sketch, "E1881", {"start": v(-255.98, 30.72) * mm, "end": v(-255.8, 30.96) * mm});
            skLineSegment(sketch, "E1882", {"start": v(-255.8, 30.96) * mm, "end": v(-255.62, 31.2) * mm});
            skLineSegment(sketch, "E1883", {"start": v(-255.62, 31.2) * mm, "end": v(-255.43, 31.43) * mm});
            skLineSegment(sketch, "E1884", {"start": v(-255.43, 31.43) * mm, "end": v(-255.23, 31.65) * mm});
            skLineSegment(sketch, "E1885", {"start": v(-255.23, 31.65) * mm, "end": v(-255.02, 31.87) * mm});
            skLineSegment(sketch, "E1886", {"start": v(-255.02, 31.87) * mm, "end": v(-254.81, 32.1) * mm});
            skLineSegment(sketch, "E1887", {"start": v(-254.81, 32.1) * mm, "end": v(-254.51, 32.37) * mm});
            skLineSegment(sketch, "E1888", {"start": v(-254.51, 32.37) * mm, "end": v(-254.2, 32.65) * mm});
            skLineSegment(sketch, "E1889", {"start": v(-254.2, 32.65) * mm, "end": v(-253.9, 32.92) * mm});
            skLineSegment(sketch, "E1890", {"start": v(-253.9, 32.92) * mm, "end": v(-253.57, 33.18) * mm});
            skLineSegment(sketch, "E1891", {"start": v(-253.57, 33.18) * mm, "end": v(-253.25, 33.43) * mm});
            skLineSegment(sketch, "E1892", {"start": v(-253.25, 33.43) * mm, "end": v(-252.91, 33.67) * mm});
            skLineSegment(sketch, "E1893", {"start": v(-252.91, 33.67) * mm, "end": v(-252.58, 33.9) * mm});
            skLineSegment(sketch, "E1894", {"start": v(-252.58, 33.9) * mm, "end": v(-252.23, 34.12) * mm});
            skLineSegment(sketch, "E1895", {"start": v(-252.23, 34.12) * mm, "end": v(-251.89, 34.34) * mm});
            skLineSegment(sketch, "E1896", {"start": v(-251.89, 34.34) * mm, "end": v(-251.53, 34.54) * mm});
            skLineSegment(sketch, "E1897", {"start": v(-251.53, 34.54) * mm, "end": v(-251.17, 34.74) * mm});
            skLineSegment(sketch, "E1898", {"start": v(-251.17, 34.74) * mm, "end": v(-250.81, 34.92) * mm});
            skLineSegment(sketch, "E1899", {"start": v(-250.81, 34.92) * mm, "end": v(-250.44, 35.1) * mm});
            skLineSegment(sketch, "E1900", {"start": v(-250.44, 35.1) * mm, "end": v(-250.07, 35.27) * mm});
            skLineSegment(sketch, "E1901", {"start": v(-250.07, 35.27) * mm, "end": v(-249.7, 35.43) * mm});
            skLineSegment(sketch, "E1902", {"start": v(-249.7, 35.43) * mm, "end": v(-249.32, 35.58) * mm});
            skLineSegment(sketch, "E1903", {"start": v(-249.32, 35.58) * mm, "end": v(-248.94, 35.72) * mm});
            skLineSegment(sketch, "E1904", {"start": v(-248.94, 35.72) * mm, "end": v(-248.55, 35.85) * mm});
            skLineSegment(sketch, "E1905", {"start": v(-248.55, 35.85) * mm, "end": v(-248.16, 35.97) * mm});
            skLineSegment(sketch, "E1906", {"start": v(-248.16, 35.97) * mm, "end": v(-247.77, 36.08) * mm});
            skLineSegment(sketch, "E1907", {"start": v(-247.77, 36.08) * mm, "end": v(-247.37, 36.18) * mm});
            skLineSegment(sketch, "E1908", {"start": v(-247.37, 36.18) * mm, "end": v(-246.97, 36.27) * mm});
            skLineSegment(sketch, "E1909", {"start": v(-246.97, 36.27) * mm, "end": v(-246.57, 36.35) * mm});
            skLineSegment(sketch, "E1910", {"start": v(-246.57, 36.35) * mm, "end": v(-246.17, 36.42) * mm});
            skLineSegment(sketch, "E1911", {"start": v(-246.17, 36.42) * mm, "end": v(-245.77, 36.48) * mm});
            skLineSegment(sketch, "E1912", {"start": v(-245.77, 36.48) * mm, "end": v(-245.36, 36.53) * mm});
            skLineSegment(sketch, "E1913", {"start": v(-245.36, 36.53) * mm, "end": v(-244.95, 36.57) * mm});
            skLineSegment(sketch, "E1914", {"start": v(-244.95, 36.57) * mm, "end": v(-244.54, 36.6) * mm});
            skLineSegment(sketch, "E1915", {"start": v(-244.54, 36.6) * mm, "end": v(-244.13, 36.61) * mm});
            skLineSegment(sketch, "E1916", {"start": v(-244.13, 36.61) * mm, "end": v(-243.72, 36.62) * mm});
            skLineSegment(sketch, "E1917", {"start": v(-243.72, 36.62) * mm, "end": v(-243.3, 36.62) * mm});
            skLineSegment(sketch, "E1918", {"start": v(-243.3, 36.62) * mm, "end": v(-242.9, 36.6) * mm});
            skLineSegment(sketch, "E1919", {"start": v(-242.9, 36.6) * mm, "end": v(-242.47, 36.62) * mm});
            skLineSegment(sketch, "E1920", {"start": v(-242.47, 36.62) * mm, "end": v(-242.04, 36.62) * mm});
            skLineSegment(sketch, "E1921", {"start": v(-242.04, 36.62) * mm, "end": v(-241.62, 36.61) * mm});
            skLineSegment(sketch, "E1922", {"start": v(-241.62, 36.61) * mm, "end": v(-241.2, 36.6) * mm});
            skLineSegment(sketch, "E1923", {"start": v(-241.2, 36.6) * mm, "end": v(-240.78, 36.56) * mm});
            skLineSegment(sketch, "E1924", {"start": v(-240.78, 36.56) * mm, "end": v(-240.36, 36.52) * mm});
            skLineSegment(sketch, "E1925", {"start": v(-240.36, 36.52) * mm, "end": v(-239.94, 36.47) * mm});
            skLineSegment(sketch, "E1926", {"start": v(-239.94, 36.47) * mm, "end": v(-239.52, 36.4) * mm});
            skLineSegment(sketch, "E1927", {"start": v(-239.52, 36.4) * mm, "end": v(-239.11, 36.33) * mm});
            skLineSegment(sketch, "E1928", {"start": v(-239.11, 36.33) * mm, "end": v(-238.7, 36.25) * mm});
            skLineSegment(sketch, "E1929", {"start": v(-238.7, 36.25) * mm, "end": v(-238.3, 36.16) * mm});
            skLineSegment(sketch, "E1930", {"start": v(-238.3, 36.16) * mm, "end": v(-237.89, 36.05) * mm});
            skLineSegment(sketch, "E1931", {"start": v(-237.89, 36.05) * mm, "end": v(-237.48, 35.94) * mm});
            skLineSegment(sketch, "E1932", {"start": v(-237.48, 35.94) * mm, "end": v(-237.08, 35.82) * mm});
            skLineSegment(sketch, "E1933", {"start": v(-237.08, 35.82) * mm, "end": v(-236.69, 35.68) * mm});
            skLineSegment(sketch, "E1934", {"start": v(-236.69, 35.68) * mm, "end": v(-236.3, 35.54) * mm});
            skLineSegment(sketch, "E1935", {"start": v(-236.3, 35.54) * mm, "end": v(-235.9, 35.39) * mm});
            skLineSegment(sketch, "E1936", {"start": v(-235.9, 35.39) * mm, "end": v(-235.52, 35.22) * mm});
            skLineSegment(sketch, "E1937", {"start": v(-235.52, 35.22) * mm, "end": v(-235.14, 35.05) * mm});
            skLineSegment(sketch, "E1938", {"start": v(-235.14, 35.05) * mm, "end": v(-234.76, 34.87) * mm});
            skLineSegment(sketch, "E1939", {"start": v(-234.76, 34.87) * mm, "end": v(-234.39, 34.68) * mm});
            skLineSegment(sketch, "E1940", {"start": v(-234.39, 34.68) * mm, "end": v(-234.02, 34.47) * mm});
            skLineSegment(sketch, "E1941", {"start": v(-234.02, 34.47) * mm, "end": v(-233.66, 34.26) * mm});
            skLineSegment(sketch, "E1942", {"start": v(-233.66, 34.26) * mm, "end": v(-233.3, 34.04) * mm});
            skLineSegment(sketch, "E1943", {"start": v(-233.3, 34.04) * mm, "end": v(-232.95, 33.82) * mm});
            skLineSegment(sketch, "E1944", {"start": v(-232.95, 33.82) * mm, "end": v(-232.6, 33.58) * mm});
            skLineSegment(sketch, "E1945", {"start": v(-232.6, 33.58) * mm, "end": v(-232.26, 33.33) * mm});
            skLineSegment(sketch, "E1946", {"start": v(-232.26, 33.33) * mm, "end": v(-231.92, 33.07) * mm});
            skLineSegment(sketch, "E1947", {"start": v(-231.92, 33.07) * mm, "end": v(-231.6, 32.8) * mm});
            skLineSegment(sketch, "E1948", {"start": v(-231.6, 32.8) * mm, "end": v(-231.27, 32.54) * mm});
            skLineSegment(sketch, "E1949", {"start": v(-231.27, 32.54) * mm, "end": v(-230.96, 32.25) * mm});
            skLineSegment(sketch, "E1950", {"start": v(-230.96, 32.25) * mm, "end": v(-230.65, 31.96) * mm});
            skLineSegment(sketch, "E1951", {"start": v(-230.65, 31.96) * mm, "end": v(-230.27, 31.58) * mm});
            skLineSegment(sketch, "E1952", {"start": v(-230.27, 31.58) * mm, "end": v(-229.9, 31.18) * mm});
            skLineSegment(sketch, "E1953", {"start": v(-229.9, 31.18) * mm, "end": v(-229.57, 30.76) * mm});
            skLineSegment(sketch, "E1954", {"start": v(-229.57, 30.76) * mm, "end": v(-229.26, 30.33) * mm});
            skLineSegment(sketch, "E1955", {"start": v(-229.26, 30.33) * mm, "end": v(-228.97, 29.89) * mm});
            skLineSegment(sketch, "E1956", {"start": v(-228.97, 29.89) * mm, "end": v(-228.7, 29.43) * mm});
            skLineSegment(sketch, "E1957", {"start": v(-228.7, 29.43) * mm, "end": v(-228.46, 28.95) * mm});
            skLineSegment(sketch, "E1958", {"start": v(-228.46, 28.95) * mm, "end": v(-228.25, 28.47) * mm});
            skLineSegment(sketch, "E1959", {"start": v(-228.25, 28.47) * mm, "end": v(-228.05, 27.97) * mm});
            skLineSegment(sketch, "E1960", {"start": v(-228.05, 27.97) * mm, "end": v(-227.89, 27.47) * mm});
            skLineSegment(sketch, "E1961", {"start": v(-227.89, 27.47) * mm, "end": v(-227.75, 26.96) * mm});
            skLineSegment(sketch, "E1962", {"start": v(-227.75, 26.96) * mm, "end": v(-227.63, 26.44) * mm});
            skLineSegment(sketch, "E1963", {"start": v(-227.63, 26.44) * mm, "end": v(-227.55, 25.91) * mm});
            skLineSegment(sketch, "E1964", {"start": v(-227.55, 25.91) * mm, "end": v(-227.49, 25.38) * mm});
            skLineSegment(sketch, "E1965", {"start": v(-227.49, 25.38) * mm, "end": v(-227.45, 24.85) * mm});
            skLineSegment(sketch, "E1966", {"start": v(-227.45, 24.85) * mm, "end": v(-227.45, 24.3) * mm});
            skLineSegment(sketch, "E1967", {"start": v(-227.45, 24.3) * mm, "end": v(-227.45, 24) * mm});
            skLineSegment(sketch, "E1968", {"start": v(-227.45, 24) * mm, "end": v(-227.47, 23.69) * mm});
            skLineSegment(sketch, "E1969", {"start": v(-227.47, 23.69) * mm, "end": v(-227.49, 23.38) * mm});
            skLineSegment(sketch, "E1970", {"start": v(-227.49, 23.38) * mm, "end": v(-227.51, 23.07) * mm});
            skLineSegment(sketch, "E1971", {"start": v(-227.51, 23.07) * mm, "end": v(-227.55, 22.77) * mm});
            skLineSegment(sketch, "E1972", {"start": v(-227.55, 22.77) * mm, "end": v(-227.6, 22.46) * mm});
            skLineSegment(sketch, "E1973", {"start": v(-227.6, 22.46) * mm, "end": v(-227.64, 22.16) * mm});
            skLineSegment(sketch, "E1974", {"start": v(-227.64, 22.16) * mm, "end": v(-227.7, 21.86) * mm});
            skLineSegment(sketch, "E1975", {"start": v(-227.7, 21.86) * mm, "end": v(-227.77, 21.56) * mm});
            skLineSegment(sketch, "E1976", {"start": v(-227.77, 21.56) * mm, "end": v(-227.84, 21.27) * mm});
            skLineSegment(sketch, "E1977", {"start": v(-227.84, 21.27) * mm, "end": v(-227.92, 20.97) * mm});
            skLineSegment(sketch, "E1978", {"start": v(-227.92, 20.97) * mm, "end": v(-228.01, 20.68) * mm});
            skLineSegment(sketch, "E1979", {"start": v(-228.01, 20.68) * mm, "end": v(-228.1, 20.39) * mm});
            skLineSegment(sketch, "E1980", {"start": v(-228.1, 20.39) * mm, "end": v(-228.2, 20.1) * mm});
            skLineSegment(sketch, "E1981", {"start": v(-228.2, 20.1) * mm, "end": v(-228.32, 19.82) * mm});
            skLineSegment(sketch, "E1982", {"start": v(-228.32, 19.82) * mm, "end": v(-228.44, 19.54) * mm});
            skLineSegment(sketch, "E1983", {"start": v(-228.44, 19.54) * mm, "end": v(-228.56, 19.26) * mm});
            skLineSegment(sketch, "E1984", {"start": v(-228.56, 19.26) * mm, "end": v(-228.69, 18.98) * mm});
            skLineSegment(sketch, "E1985", {"start": v(-228.69, 18.98) * mm, "end": v(-228.83, 18.7) * mm});
            skLineSegment(sketch, "E1986", {"start": v(-228.83, 18.7) * mm, "end": v(-228.97, 18.44) * mm});
            skLineSegment(sketch, "E1987", {"start": v(-228.97, 18.44) * mm, "end": v(-229.12, 18.18) * mm});
            skLineSegment(sketch, "E1988", {"start": v(-229.12, 18.18) * mm, "end": v(-229.28, 17.91) * mm});
            skLineSegment(sketch, "E1989", {"start": v(-229.28, 17.91) * mm, "end": v(-229.44, 17.66) * mm});
            skLineSegment(sketch, "E1990", {"start": v(-229.44, 17.66) * mm, "end": v(-229.61, 17.4) * mm});
            skLineSegment(sketch, "E1991", {"start": v(-229.61, 17.4) * mm, "end": v(-229.8, 17.15) * mm});
            skLineSegment(sketch, "E1992", {"start": v(-229.8, 17.15) * mm, "end": v(-229.97, 16.9) * mm});
            skLineSegment(sketch, "E1993", {"start": v(-229.97, 16.9) * mm, "end": v(-230.16, 16.67) * mm});
            skLineSegment(sketch, "E1994", {"start": v(-230.16, 16.67) * mm, "end": v(-230.36, 16.43) * mm});
            skLineSegment(sketch, "E1995", {"start": v(-230.36, 16.43) * mm, "end": v(-230.56, 16.2) * mm});
            skLineSegment(sketch, "E1996", {"start": v(-230.56, 16.2) * mm, "end": v(-230.77, 15.97) * mm});
            skLineSegment(sketch, "E1997", {"start": v(-230.77, 15.97) * mm, "end": v(-230.99, 15.75) * mm});
            skLineSegment(sketch, "E1998", {"start": v(-230.99, 15.75) * mm, "end": v(-231.2, 15.53) * mm});
            skLineSegment(sketch, "E1999", {"start": v(-231.2, 15.53) * mm, "end": v(-231.47, 15.28) * mm});
            skLineSegment(sketch, "E2000", {"start": v(-231.47, 15.28) * mm, "end": v(-231.74, 15.03) * mm});
            skLineSegment(sketch, "E2001", {"start": v(-231.74, 15.03) * mm, "end": v(-232.01, 14.8) * mm});
            skLineSegment(sketch, "E2002", {"start": v(-232.01, 14.8) * mm, "end": v(-232.3, 14.56) * mm});
            skLineSegment(sketch, "E2003", {"start": v(-232.3, 14.56) * mm, "end": v(-232.58, 14.34) * mm});
            skLineSegment(sketch, "E2004", {"start": v(-232.58, 14.34) * mm, "end": v(-232.87, 14.12) * mm});
            skLineSegment(sketch, "E2005", {"start": v(-232.87, 14.12) * mm, "end": v(-233.17, 13.91) * mm});
            skLineSegment(sketch, "E2006", {"start": v(-233.17, 13.91) * mm, "end": v(-233.47, 13.71) * mm});
            skLineSegment(sketch, "E2007", {"start": v(-233.47, 13.71) * mm, "end": v(-233.77, 13.52) * mm});
            skLineSegment(sketch, "E2008", {"start": v(-233.77, 13.52) * mm, "end": v(-234.08, 13.33) * mm});
            skLineSegment(sketch, "E2009", {"start": v(-234.08, 13.33) * mm, "end": v(-234.4, 13.15) * mm});
            skLineSegment(sketch, "E2010", {"start": v(-234.4, 13.15) * mm, "end": v(-234.71, 12.98) * mm});
            skLineSegment(sketch, "E2011", {"start": v(-234.71, 12.98) * mm, "end": v(-235.03, 12.82) * mm});
            skLineSegment(sketch, "E2012", {"start": v(-235.03, 12.82) * mm, "end": v(-235.36, 12.66) * mm});
            skLineSegment(sketch, "E2013", {"start": v(-235.36, 12.66) * mm, "end": v(-235.69, 12.51) * mm});
            skLineSegment(sketch, "E2014", {"start": v(-235.69, 12.51) * mm, "end": v(-236.02, 12.38) * mm});
            skLineSegment(sketch, "E2015", {"start": v(-236.02, 12.38) * mm, "end": v(-236.36, 12.24) * mm});
            skLineSegment(sketch, "E2016", {"start": v(-236.36, 12.24) * mm, "end": v(-236.7, 12.12) * mm});
            skLineSegment(sketch, "E2017", {"start": v(-236.7, 12.12) * mm, "end": v(-237.04, 12) * mm});
            skLineSegment(sketch, "E2018", {"start": v(-237.04, 12) * mm, "end": v(-237.38, 11.9) * mm});
            skLineSegment(sketch, "E2019", {"start": v(-237.38, 11.9) * mm, "end": v(-237.73, 11.8) * mm});
            skLineSegment(sketch, "E2020", {"start": v(-237.73, 11.8) * mm, "end": v(-238.08, 11.71) * mm});
            skLineSegment(sketch, "E2021", {"start": v(-238.08, 11.71) * mm, "end": v(-238.43, 11.63) * mm});
            skLineSegment(sketch, "E2022", {"start": v(-238.43, 11.63) * mm, "end": v(-238.78, 11.56) * mm});
            skLineSegment(sketch, "E2023", {"start": v(-238.78, 11.56) * mm, "end": v(-239.14, 11.5) * mm});
            skLineSegment(sketch, "E2024", {"start": v(-239.14, 11.5) * mm, "end": v(-239.5, 11.44) * mm});
            skLineSegment(sketch, "E2025", {"start": v(-239.5, 11.44) * mm, "end": v(-239.86, 11.4) * mm});
            skLineSegment(sketch, "E2026", {"start": v(-239.86, 11.4) * mm, "end": v(-240.22, 11.36) * mm});
            skLineSegment(sketch, "E2027", {"start": v(-240.22, 11.36) * mm, "end": v(-240.58, 11.33) * mm});
            skLineSegment(sketch, "E2028", {"start": v(-240.58, 11.33) * mm, "end": v(-240.94, 11.3) * mm});
            skLineSegment(sketch, "E2029", {"start": v(-240.94, 11.3) * mm, "end": v(-241.3, 11.3) * mm});
            skLineSegment(sketch, "E2030", {"start": v(-241.3, 11.3) * mm, "end": v(-241.68, 11.3) * mm});
            skLineSegment(sketch, "E2031", {"start": v(-241.68, 11.3) * mm, "end": v(-241.68, 36.52) * mm});
            skArc(sketch, "E2032", {"start": v(-531.3, -475.42) * mm, "mid": v(-533.43, -476.3) * mm, "end": v(-534.3, -478.42) * mm});
            skArc(sketch, "E2033", {"start": v(-534.3, -478.42) * mm, "mid": v(-533.43, -480.55) * mm, "end": v(-531.3, -481.42) * mm});
            skArc(sketch, "E2034", {"start": v(-531.3, -481.42) * mm, "mid": v(-529.19, -480.55) * mm, "end": v(-528.3, -478.42) * mm});
            skArc(sketch, "E2035", {"start": v(-528.3, -478.42) * mm, "mid": v(-529.19, -476.3) * mm, "end": v(-531.3, -475.42) * mm});
            skArc(sketch, "E2036", {"start": v(-235.64, -729.85) * mm, "mid": v(-237.76, -730.73) * mm, "end": v(-238.64, -732.85) * mm});
            skArc(sketch, "E2037", {"start": v(-238.64, -732.85) * mm, "mid": v(-237.76, -734.98) * mm, "end": v(-235.64, -735.85) * mm});
            skArc(sketch, "E2038", {"start": v(-235.64, -735.85) * mm, "mid": v(-233.51, -734.98) * mm, "end": v(-232.64, -732.85) * mm});
            skArc(sketch, "E2039", {"start": v(-232.64, -732.85) * mm, "mid": v(-233.51, -730.73) * mm, "end": v(-235.64, -729.85) * mm});
            skArc(sketch, "E2040", {"start": v(19.04, -922.52) * mm, "mid": v(16.92, -923.4) * mm, "end": v(16.04, -925.52) * mm});
            skArc(sketch, "E2041", {"start": v(16.04, -925.52) * mm, "mid": v(16.92, -927.64) * mm, "end": v(19.04, -928.52) * mm});
            skArc(sketch, "E2042", {"start": v(19.04, -928.52) * mm, "mid": v(21.16, -927.64) * mm, "end": v(22.04, -925.52) * mm});
            skArc(sketch, "E2043", {"start": v(22.04, -925.52) * mm, "mid": v(21.16, -923.4) * mm, "end": v(19.04, -922.52) * mm});
            skArc(sketch, "E2044", {"start": v(576.65, -602.85) * mm, "mid": v(574.53, -603.73) * mm, "end": v(573.65, -605.85) * mm});
            skArc(sketch, "E2045", {"start": v(573.65, -605.85) * mm, "mid": v(574.53, -607.97) * mm, "end": v(576.65, -608.85) * mm});
            skArc(sketch, "E2046", {"start": v(576.65, -608.85) * mm, "mid": v(578.78, -607.97) * mm, "end": v(579.65, -605.85) * mm});
            skArc(sketch, "E2047", {"start": v(579.65, -605.85) * mm, "mid": v(578.78, -603.73) * mm, "end": v(576.65, -602.85) * mm});
            skArc(sketch, "E2048", {"start": v(-33.84, -201.47) * mm, "mid": v(-35.96, -202.34) * mm, "end": v(-36.84, -204.47) * mm});
            skArc(sketch, "E2049", {"start": v(-36.84, -204.47) * mm, "mid": v(-35.96, -206.59) * mm, "end": v(-33.84, -207.47) * mm});
            skArc(sketch, "E2050", {"start": v(-33.84, -207.47) * mm, "mid": v(-31.72, -206.59) * mm, "end": v(-30.84, -204.47) * mm});
            skArc(sketch, "E2051", {"start": v(-30.84, -204.47) * mm, "mid": v(-31.72, -202.34) * mm, "end": v(-33.84, -201.47) * mm});
            skArc(sketch, "E2052", {"start": v(-565.01, 267.22) * mm, "mid": v(-567.13, 266.34) * mm, "end": v(-568.01, 264.22) * mm});
            skArc(sketch, "E2053", {"start": v(-568.01, 264.22) * mm, "mid": v(-567.13, 262.1) * mm, "end": v(-565.01, 261.22) * mm});
            skArc(sketch, "E2054", {"start": v(-565.01, 261.22) * mm, "mid": v(-562.9, 262.1) * mm, "end": v(-562.01, 264.22) * mm});
            skArc(sketch, "E2055", {"start": v(-562.01, 264.22) * mm, "mid": v(-562.9, 266.34) * mm, "end": v(-565.01, 267.22) * mm});
            skArc(sketch, "E2056", {"start": v(595.88, 14.85) * mm, "mid": v(593.76, 13.97) * mm, "end": v(592.88, 11.85) * mm});
            skArc(sketch, "E2057", {"start": v(592.88, 11.85) * mm, "mid": v(593.76, 9.73) * mm, "end": v(595.88, 8.85) * mm});
            skArc(sketch, "E2058", {"start": v(595.88, 8.85) * mm, "mid": v(598, 9.73) * mm, "end": v(598.88, 11.85) * mm});
            skArc(sketch, "E2059", {"start": v(598.88, 11.85) * mm, "mid": v(598, 13.97) * mm, "end": v(595.88, 14.85) * mm});
            skArc(sketch, "E2060", {"start": v(595.88, 637.36) * mm, "mid": v(593.76, 636.48) * mm, "end": v(592.88, 634.36) * mm});
            skArc(sketch, "E2061", {"start": v(592.88, 634.36) * mm, "mid": v(593.76, 632.24) * mm, "end": v(595.88, 631.36) * mm});
            skArc(sketch, "E2062", {"start": v(595.88, 631.36) * mm, "mid": v(598, 632.24) * mm, "end": v(598.88, 634.36) * mm});
            skArc(sketch, "E2063", {"start": v(598.88, 634.36) * mm, "mid": v(598, 636.48) * mm, "end": v(595.88, 637.36) * mm});
            skArc(sketch, "E2064", {"start": v(-567.42, 954.62) * mm, "mid": v(-569.54, 953.74) * mm, "end": v(-570.42, 951.62) * mm});
            skArc(sketch, "E2065", {"start": v(-570.42, 951.62) * mm, "mid": v(-569.54, 949.5) * mm, "end": v(-567.42, 948.62) * mm});
            skArc(sketch, "E2066", {"start": v(-567.42, 948.62) * mm, "mid": v(-565.3, 949.5) * mm, "end": v(-564.42, 951.62) * mm});
            skArc(sketch, "E2067", {"start": v(-564.42, 951.62) * mm, "mid": v(-565.3, 953.74) * mm, "end": v(-567.42, 954.62) * mm});
            skArc(sketch, "E2068", {"start": v(-286.2, 1125.27) * mm, "mid": v(-288.33, 1124.4) * mm, "end": v(-289.2, 1122.27) * mm});
            skArc(sketch, "E2069", {"start": v(-289.2, 1122.27) * mm, "mid": v(-288.33, 1120.15) * mm, "end": v(-286.2, 1119.27) * mm});
            skArc(sketch, "E2070", {"start": v(-286.2, 1119.27) * mm, "mid": v(-284.08, 1120.15) * mm, "end": v(-283.2, 1122.27) * mm});
            skArc(sketch, "E2071", {"start": v(-283.2, 1122.27) * mm, "mid": v(-284.08, 1124.4) * mm, "end": v(-286.2, 1125.27) * mm});
            skArc(sketch, "E2072", {"start": v(574.09, 1170.3) * mm, "mid": v(571.97, 1169.42) * mm, "end": v(571.09, 1167.3) * mm});
            skArc(sketch, "E2073", {"start": v(571.09, 1167.3) * mm, "mid": v(571.97, 1165.17) * mm, "end": v(574.09, 1164.3) * mm});
            skArc(sketch, "E2074", {"start": v(574.09, 1164.3) * mm, "mid": v(576.21, 1165.17) * mm, "end": v(577.09, 1167.3) * mm});
            skArc(sketch, "E2075", {"start": v(577.09, 1167.3) * mm, "mid": v(576.21, 1169.42) * mm, "end": v(574.09, 1170.3) * mm});
            skArc(sketch, "E2076", {"start": v(-44.81, 214.9) * mm, "mid": v(-46.94, 214.02) * mm, "end": v(-47.81, 211.9) * mm});
            skArc(sketch, "E2077", {"start": v(-47.81, 211.9) * mm, "mid": v(-46.94, 209.78) * mm, "end": v(-44.81, 208.9) * mm});
            skArc(sketch, "E2078", {"start": v(-44.81, 208.9) * mm, "mid": v(-42.7, 209.78) * mm, "end": v(-41.81, 211.9) * mm});
            skArc(sketch, "E2079", {"start": v(-41.81, 211.9) * mm, "mid": v(-42.7, 214.02) * mm, "end": v(-44.81, 214.9) * mm});
            skArc(sketch, "E2080", {"start": v(95.55, 1111.41) * mm, "mid": v(93.43, 1110.53) * mm, "end": v(92.55, 1108.41) * mm});
            skArc(sketch, "E2081", {"start": v(92.55, 1108.41) * mm, "mid": v(93.43, 1106.29) * mm, "end": v(95.55, 1105.41) * mm});
            skArc(sketch, "E2082", {"start": v(95.55, 1105.41) * mm, "mid": v(97.67, 1106.29) * mm, "end": v(98.55, 1108.41) * mm});
            skArc(sketch, "E2083", {"start": v(98.55, 1108.41) * mm, "mid": v(97.67, 1110.53) * mm, "end": v(95.55, 1111.41) * mm});
            skArc(sketch, "E2084", {"start": v(-48.66, 792.22) * mm, "mid": v(-50.78, 791.35) * mm, "end": v(-51.66, 789.22) * mm});
            skArc(sketch, "E2085", {"start": v(-51.66, 789.22) * mm, "mid": v(-50.78, 787.1) * mm, "end": v(-48.66, 786.22) * mm});
            skArc(sketch, "E2086", {"start": v(-48.66, 786.22) * mm, "mid": v(-46.54, 787.1) * mm, "end": v(-45.66, 789.22) * mm});
            skArc(sketch, "E2087", {"start": v(-45.66, 789.22) * mm, "mid": v(-46.54, 791.35) * mm, "end": v(-48.66, 792.22) * mm});
            skArc(sketch, "E2088", {"start": v(283.19, -384.2) * mm, "mid": v(281.06, -385.08) * mm, "end": v(280.19, -387.2) * mm});
            skArc(sketch, "E2089", {"start": v(280.19, -387.2) * mm, "mid": v(281.06, -389.33) * mm, "end": v(283.19, -390.2) * mm});
            skArc(sketch, "E2090", {"start": v(283.19, -390.2) * mm, "mid": v(285.3, -389.33) * mm, "end": v(286.19, -387.2) * mm});
            skArc(sketch, "E2091", {"start": v(286.19, -387.2) * mm, "mid": v(285.3, -385.08) * mm, "end": v(283.19, -384.2) * mm});
            skSolve(sketch);
        }
        {
            var Q0;
            Q0=makeQuery(id+"F0.imprint","IMPRINT",FACE,{"disambiguationData":[TD([[makeQuery(id+"F0.imprint","IMPRINT",EDGE,{"derivedFrom":sQuery(id+"F0.wireOp",EDGE,"E234")}),1.0]])]});
            extrude(context, id + "F1", {"entities" : qUnion([Q0]), "depth" : 25 * mm});
        }
        {
            var Q0;
            Q0=makeQuery(id+"F0.imprint","IMPRINT",FACE,{"disambiguationData":[TD([[makeQuery(id+"F0.imprint","IMPRINT",EDGE,{"derivedFrom":sQuery(id+"F0.wireOp",EDGE,"E346")}),1.0]])]});
            extrude(context, id + "F2", {"entities" : qUnion([Q0]), "depth" : 18 * mm});
        }
        {
            var Q0;
            Q0=makeQuery(id+"F0.imprint","IMPRINT",FACE,{"disambiguationData":[TD([[makeQuery(id+"F0.imprint","IMPRINT",EDGE,{"derivedFrom":sQuery(id+"F0.wireOp",EDGE,"E119")}),1.0]])]});
            extrude(context, id + "F3", {"entities" : qUnion([Q0]), "depth" : 18 * mm});
        }
        {
            var Q0;
            Q0=makeQuery(id+"F0.imprint","IMPRINT",FACE,{"disambiguationData":[TD([[makeQuery(id+"F0.imprint","IMPRINT",EDGE,{"derivedFrom":sQuery(id+"F0.wireOp",EDGE,"E4")}),1.0]])]});
            extrude(context, id + "F4", {"entities" : qUnion([Q0]), "depth" : 18 * mm});
        }
    });
